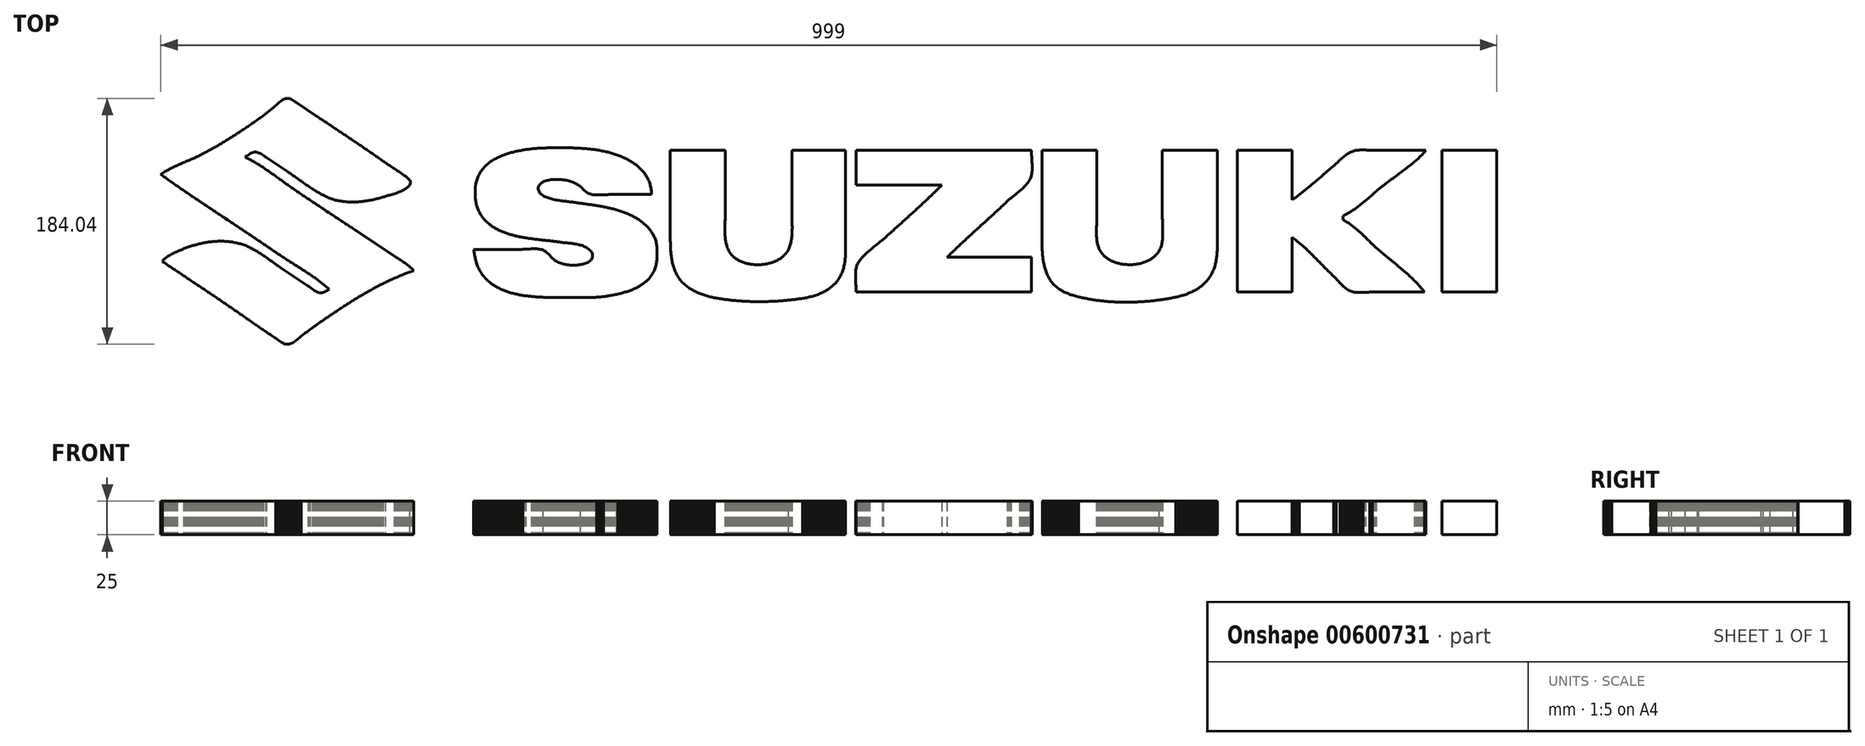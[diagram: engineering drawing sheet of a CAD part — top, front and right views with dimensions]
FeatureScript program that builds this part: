
annotation { "Feature Type Name" : "Feature", "Feature Type Description" : "" }
export const myFeature = defineFeature(function(context is Context, id is Id, definition is map)
    precondition{}
    {
        {
            var Q0;
            Q0=qCreatedBy(makeId("Top.planeOp"),FACE);
            var sketch = newSketch(context, id + "F0", { "sketchPlane" : qUnion([Q0])});
            skLineSegment(sketch, "E0", {"start": v(-499.5, 35.04) * mm, "end": v(-498.69, 34.46) * mm});
            skLineSegment(sketch, "E1", {"start": v(-498.69, 34.46) * mm, "end": v(-497.87, 33.88) * mm});
            skLineSegment(sketch, "E2", {"start": v(-497.87, 33.88) * mm, "end": v(-497.06, 33.3) * mm});
            skLineSegment(sketch, "E3", {"start": v(-497.06, 33.3) * mm, "end": v(-496.24, 32.72) * mm});
            skLineSegment(sketch, "E4", {"start": v(-496.24, 32.72) * mm, "end": v(-495.43, 32.14) * mm});
            skLineSegment(sketch, "E5", {"start": v(-495.43, 32.14) * mm, "end": v(-494.6, 31.56) * mm});
            skLineSegment(sketch, "E6", {"start": v(-494.6, 31.56) * mm, "end": v(-493.8, 30.99) * mm});
            skLineSegment(sketch, "E7", {"start": v(-493.8, 30.99) * mm, "end": v(-492.97, 30.41) * mm});
            skLineSegment(sketch, "E8", {"start": v(-492.97, 30.41) * mm, "end": v(-492.15, 29.84) * mm});
            skLineSegment(sketch, "E9", {"start": v(-492.15, 29.84) * mm, "end": v(-491.33, 29.26) * mm});
            skLineSegment(sketch, "E10", {"start": v(-491.33, 29.26) * mm, "end": v(-490.52, 28.69) * mm});
            skLineSegment(sketch, "E11", {"start": v(-490.52, 28.69) * mm, "end": v(-489.7, 28.11) * mm});
            skLineSegment(sketch, "E12", {"start": v(-489.7, 28.11) * mm, "end": v(-488.87, 27.54) * mm});
            skLineSegment(sketch, "E13", {"start": v(-488.87, 27.54) * mm, "end": v(-488.05, 26.97) * mm});
            skLineSegment(sketch, "E14", {"start": v(-488.05, 26.97) * mm, "end": v(-487.23, 26.4) * mm});
            skLineSegment(sketch, "E15", {"start": v(-487.23, 26.4) * mm, "end": v(-486.4, 25.83) * mm});
            skLineSegment(sketch, "E16", {"start": v(-486.4, 25.83) * mm, "end": v(-485.59, 25.26) * mm});
            skLineSegment(sketch, "E17", {"start": v(-485.59, 25.26) * mm, "end": v(-484.76, 24.7) * mm});
            skLineSegment(sketch, "E18", {"start": v(-484.76, 24.7) * mm, "end": v(-483.94, 24.12) * mm});
            skLineSegment(sketch, "E19", {"start": v(-483.94, 24.12) * mm, "end": v(-483.11, 23.56) * mm});
            skLineSegment(sketch, "E20", {"start": v(-483.11, 23.56) * mm, "end": v(-482.29, 22.99) * mm});
            skLineSegment(sketch, "E21", {"start": v(-482.29, 22.99) * mm, "end": v(-481.46, 22.42) * mm});
            skLineSegment(sketch, "E22", {"start": v(-481.46, 22.42) * mm, "end": v(-480.64, 21.86) * mm});
            skLineSegment(sketch, "E23", {"start": v(-480.64, 21.86) * mm, "end": v(-479.81, 21.3) * mm});
            skLineSegment(sketch, "E24", {"start": v(-479.81, 21.3) * mm, "end": v(-478.99, 20.73) * mm});
            skLineSegment(sketch, "E25", {"start": v(-478.99, 20.73) * mm, "end": v(-478.16, 20.16) * mm});
            skLineSegment(sketch, "E26", {"start": v(-478.16, 20.16) * mm, "end": v(-477.33, 19.6) * mm});
            skLineSegment(sketch, "E27", {"start": v(-477.33, 19.6) * mm, "end": v(-476.5, 19.04) * mm});
            skLineSegment(sketch, "E28", {"start": v(-476.5, 19.04) * mm, "end": v(-475.68, 18.47) * mm});
            skLineSegment(sketch, "E29", {"start": v(-475.68, 18.47) * mm, "end": v(-474.85, 17.91) * mm});
            skLineSegment(sketch, "E30", {"start": v(-474.85, 17.91) * mm, "end": v(-474.02, 17.35) * mm});
            skLineSegment(sketch, "E31", {"start": v(-474.02, 17.35) * mm, "end": v(-473.19, 16.79) * mm});
            skLineSegment(sketch, "E32", {"start": v(-473.19, 16.79) * mm, "end": v(-472.36, 16.23) * mm});
            skLineSegment(sketch, "E33", {"start": v(-472.36, 16.23) * mm, "end": v(-471.53, 15.67) * mm});
            skLineSegment(sketch, "E34", {"start": v(-471.53, 15.67) * mm, "end": v(-470.7, 15.1) * mm});
            skLineSegment(sketch, "E35", {"start": v(-470.7, 15.1) * mm, "end": v(-469.87, 14.55) * mm});
            skLineSegment(sketch, "E36", {"start": v(-469.87, 14.55) * mm, "end": v(-469.04, 13.99) * mm});
            skLineSegment(sketch, "E37", {"start": v(-469.04, 13.99) * mm, "end": v(-468.2, 13.43) * mm});
            skLineSegment(sketch, "E38", {"start": v(-468.2, 13.43) * mm, "end": v(-467.38, 12.87) * mm});
            skLineSegment(sketch, "E39", {"start": v(-467.38, 12.87) * mm, "end": v(-466.55, 12.31) * mm});
            skLineSegment(sketch, "E40", {"start": v(-466.55, 12.31) * mm, "end": v(-465.71, 11.76) * mm});
            skLineSegment(sketch, "E41", {"start": v(-465.71, 11.76) * mm, "end": v(-464.88, 11.2) * mm});
            skLineSegment(sketch, "E42", {"start": v(-464.88, 11.2) * mm, "end": v(-464.05, 10.64) * mm});
            skLineSegment(sketch, "E43", {"start": v(-464.05, 10.64) * mm, "end": v(-463.22, 10.09) * mm});
            skLineSegment(sketch, "E44", {"start": v(-463.22, 10.09) * mm, "end": v(-462.39, 9.53) * mm});
            skLineSegment(sketch, "E45", {"start": v(-462.39, 9.53) * mm, "end": v(-461.55, 8.97) * mm});
            skLineSegment(sketch, "E46", {"start": v(-461.55, 8.97) * mm, "end": v(-460.72, 8.42) * mm});
            skLineSegment(sketch, "E47", {"start": v(-460.72, 8.42) * mm, "end": v(-459.89, 7.86) * mm});
            skLineSegment(sketch, "E48", {"start": v(-459.89, 7.86) * mm, "end": v(-459.05, 7.3) * mm});
            skLineSegment(sketch, "E49", {"start": v(-459.05, 7.3) * mm, "end": v(-458.22, 6.75) * mm});
            skLineSegment(sketch, "E50", {"start": v(-458.22, 6.75) * mm, "end": v(-457.39, 6.2) * mm});
            skLineSegment(sketch, "E51", {"start": v(-457.39, 6.2) * mm, "end": v(-456.55, 5.64) * mm});
            skLineSegment(sketch, "E52", {"start": v(-456.55, 5.64) * mm, "end": v(-455.72, 5.08) * mm});
            skLineSegment(sketch, "E53", {"start": v(-455.72, 5.08) * mm, "end": v(-454.89, 4.53) * mm});
            skLineSegment(sketch, "E54", {"start": v(-454.89, 4.53) * mm, "end": v(-454.05, 3.98) * mm});
            skLineSegment(sketch, "E55", {"start": v(-454.05, 3.98) * mm, "end": v(-453.22, 3.42) * mm});
            skLineSegment(sketch, "E56", {"start": v(-453.22, 3.42) * mm, "end": v(-452.38, 2.87) * mm});
            skLineSegment(sketch, "E57", {"start": v(-452.38, 2.87) * mm, "end": v(-451.55, 2.31) * mm});
            skLineSegment(sketch, "E58", {"start": v(-451.55, 2.31) * mm, "end": v(-450.72, 1.76) * mm});
            skLineSegment(sketch, "E59", {"start": v(-450.72, 1.76) * mm, "end": v(-449.88, 1.2) * mm});
            skLineSegment(sketch, "E60", {"start": v(-449.88, 1.2) * mm, "end": v(-449.05, 0.65) * mm});
            skLineSegment(sketch, "E61", {"start": v(-449.05, 0.65) * mm, "end": v(-448.21, 0.1) * mm});
            skLineSegment(sketch, "E62", {"start": v(-448.21, 0.1) * mm, "end": v(-447.38, -0.46) * mm});
            skLineSegment(sketch, "E63", {"start": v(-447.38, -0.46) * mm, "end": v(-446.55, -1.01) * mm});
            skLineSegment(sketch, "E64", {"start": v(-446.55, -1.01) * mm, "end": v(-445.71, -1.57) * mm});
            skLineSegment(sketch, "E65", {"start": v(-445.71, -1.57) * mm, "end": v(-444.88, -2.12) * mm});
            skLineSegment(sketch, "E66", {"start": v(-444.88, -2.12) * mm, "end": v(-444.04, -2.68) * mm});
            skLineSegment(sketch, "E67", {"start": v(-444.04, -2.68) * mm, "end": v(-443.21, -3.23) * mm});
            skLineSegment(sketch, "E68", {"start": v(-443.21, -3.23) * mm, "end": v(-442.38, -3.79) * mm});
            skLineSegment(sketch, "E69", {"start": v(-442.38, -3.79) * mm, "end": v(-441.54, -4.34) * mm});
            skLineSegment(sketch, "E70", {"start": v(-441.54, -4.34) * mm, "end": v(-440.7, -4.9) * mm});
            skLineSegment(sketch, "E71", {"start": v(-440.7, -4.9) * mm, "end": v(-439.88, -5.45) * mm});
            skLineSegment(sketch, "E72", {"start": v(-439.88, -5.45) * mm, "end": v(-439.04, -6) * mm});
            skLineSegment(sketch, "E73", {"start": v(-439.04, -6) * mm, "end": v(-438.2, -6.56) * mm});
            skLineSegment(sketch, "E74", {"start": v(-438.2, -6.56) * mm, "end": v(-437.38, -7.12) * mm});
            skLineSegment(sketch, "E75", {"start": v(-437.38, -7.12) * mm, "end": v(-436.54, -7.67) * mm});
            skLineSegment(sketch, "E76", {"start": v(-436.54, -7.67) * mm, "end": v(-435.71, -8.23) * mm});
            skLineSegment(sketch, "E77", {"start": v(-435.71, -8.23) * mm, "end": v(-434.88, -8.78) * mm});
            skLineSegment(sketch, "E78", {"start": v(-434.88, -8.78) * mm, "end": v(-434.05, -9.34) * mm});
            skLineSegment(sketch, "E79", {"start": v(-434.05, -9.34) * mm, "end": v(-433.21, -9.9) * mm});
            skLineSegment(sketch, "E80", {"start": v(-433.21, -9.9) * mm, "end": v(-432.38, -10.45) * mm});
            skLineSegment(sketch, "E81", {"start": v(-432.38, -10.45) * mm, "end": v(-431.55, -11) * mm});
            skLineSegment(sketch, "E82", {"start": v(-431.55, -11) * mm, "end": v(-430.72, -11.57) * mm});
            skLineSegment(sketch, "E83", {"start": v(-430.72, -11.57) * mm, "end": v(-429.89, -12.12) * mm});
            skLineSegment(sketch, "E84", {"start": v(-429.89, -12.12) * mm, "end": v(-429.06, -12.68) * mm});
            skLineSegment(sketch, "E85", {"start": v(-429.06, -12.68) * mm, "end": v(-428.22, -13.24) * mm});
            skLineSegment(sketch, "E86", {"start": v(-428.22, -13.24) * mm, "end": v(-427.4, -13.8) * mm});
            skLineSegment(sketch, "E87", {"start": v(-427.4, -13.8) * mm, "end": v(-426.56, -14.36) * mm});
            skLineSegment(sketch, "E88", {"start": v(-426.56, -14.36) * mm, "end": v(-425.73, -14.92) * mm});
            skLineSegment(sketch, "E89", {"start": v(-425.73, -14.92) * mm, "end": v(-424.9, -15.48) * mm});
            skLineSegment(sketch, "E90", {"start": v(-424.9, -15.48) * mm, "end": v(-424.07, -16.04) * mm});
            skLineSegment(sketch, "E91", {"start": v(-424.07, -16.04) * mm, "end": v(-423.24, -16.6) * mm});
            skLineSegment(sketch, "E92", {"start": v(-423.24, -16.6) * mm, "end": v(-422.42, -17.16) * mm});
            skLineSegment(sketch, "E93", {"start": v(-422.42, -17.16) * mm, "end": v(-421.59, -17.72) * mm});
            skLineSegment(sketch, "E94", {"start": v(-421.59, -17.72) * mm, "end": v(-420.76, -18.28) * mm});
            skLineSegment(sketch, "E95", {"start": v(-420.76, -18.28) * mm, "end": v(-419.93, -18.84) * mm});
            skLineSegment(sketch, "E96", {"start": v(-419.93, -18.84) * mm, "end": v(-419.1, -19.4) * mm});
            skLineSegment(sketch, "E97", {"start": v(-419.1, -19.4) * mm, "end": v(-418.28, -19.97) * mm});
            skLineSegment(sketch, "E98", {"start": v(-418.28, -19.97) * mm, "end": v(-417.45, -20.54) * mm});
            skLineSegment(sketch, "E99", {"start": v(-417.45, -20.54) * mm, "end": v(-416.62, -21.1) * mm});
            skLineSegment(sketch, "E100", {"start": v(-416.62, -21.1) * mm, "end": v(-415.8, -21.66) * mm});
            skLineSegment(sketch, "E101", {"start": v(-415.8, -21.66) * mm, "end": v(-414.97, -22.23) * mm});
            skLineSegment(sketch, "E102", {"start": v(-414.97, -22.23) * mm, "end": v(-414.15, -22.8) * mm});
            skLineSegment(sketch, "E103", {"start": v(-414.15, -22.8) * mm, "end": v(-413.32, -23.36) * mm});
            skLineSegment(sketch, "E104", {"start": v(-413.32, -23.36) * mm, "end": v(-412.5, -23.93) * mm});
            skLineSegment(sketch, "E105", {"start": v(-412.5, -23.93) * mm, "end": v(-411.68, -24.5) * mm});
            skLineSegment(sketch, "E106", {"start": v(-411.68, -24.5) * mm, "end": v(-410.85, -25.06) * mm});
            skLineSegment(sketch, "E107", {"start": v(-410.85, -25.06) * mm, "end": v(-410.02, -25.61) * mm});
            skLineSegment(sketch, "E108", {"start": v(-410.02, -25.61) * mm, "end": v(-409.18, -26.17) * mm});
            skLineSegment(sketch, "E109", {"start": v(-409.18, -26.17) * mm, "end": v(-408.34, -26.72) * mm});
            skLineSegment(sketch, "E110", {"start": v(-408.34, -26.72) * mm, "end": v(-407.5, -27.27) * mm});
            skLineSegment(sketch, "E111", {"start": v(-407.5, -27.27) * mm, "end": v(-406.65, -27.82) * mm});
            skLineSegment(sketch, "E112", {"start": v(-406.65, -27.82) * mm, "end": v(-405.8, -28.37) * mm});
            skLineSegment(sketch, "E113", {"start": v(-405.8, -28.37) * mm, "end": v(-404.95, -28.92) * mm});
            skLineSegment(sketch, "E114", {"start": v(-404.95, -28.92) * mm, "end": v(-404.1, -29.46) * mm});
            skLineSegment(sketch, "E115", {"start": v(-404.1, -29.46) * mm, "end": v(-403.25, -30) * mm});
            skLineSegment(sketch, "E116", {"start": v(-403.25, -30) * mm, "end": v(-402.39, -30.55) * mm});
            skLineSegment(sketch, "E117", {"start": v(-402.39, -30.55) * mm, "end": v(-401.53, -31.09) * mm});
            skLineSegment(sketch, "E118", {"start": v(-401.53, -31.09) * mm, "end": v(-400.67, -31.63) * mm});
            skLineSegment(sketch, "E119", {"start": v(-400.67, -31.63) * mm, "end": v(-399.81, -32.17) * mm});
            skLineSegment(sketch, "E120", {"start": v(-399.81, -32.17) * mm, "end": v(-398.95, -32.72) * mm});
            skLineSegment(sketch, "E121", {"start": v(-398.95, -32.72) * mm, "end": v(-398.1, -33.26) * mm});
            skLineSegment(sketch, "E122", {"start": v(-398.1, -33.26) * mm, "end": v(-397.23, -33.8) * mm});
            skLineSegment(sketch, "E123", {"start": v(-397.23, -33.8) * mm, "end": v(-396.37, -34.35) * mm});
            skLineSegment(sketch, "E124", {"start": v(-396.37, -34.35) * mm, "end": v(-395.51, -34.9) * mm});
            skLineSegment(sketch, "E125", {"start": v(-395.51, -34.9) * mm, "end": v(-394.65, -35.44) * mm});
            skLineSegment(sketch, "E126", {"start": v(-394.65, -35.44) * mm, "end": v(-393.8, -35.99) * mm});
            skLineSegment(sketch, "E127", {"start": v(-393.8, -35.99) * mm, "end": v(-392.94, -36.54) * mm});
            skLineSegment(sketch, "E128", {"start": v(-392.94, -36.54) * mm, "end": v(-392.08, -37.09) * mm});
            skLineSegment(sketch, "E129", {"start": v(-392.08, -37.09) * mm, "end": v(-391.23, -37.64) * mm});
            skLineSegment(sketch, "E130", {"start": v(-391.23, -37.64) * mm, "end": v(-390.38, -38.2) * mm});
            skLineSegment(sketch, "E131", {"start": v(-390.38, -38.2) * mm, "end": v(-389.53, -38.76) * mm});
            skLineSegment(sketch, "E132", {"start": v(-389.53, -38.76) * mm, "end": v(-388.68, -39.33) * mm});
            skLineSegment(sketch, "E133", {"start": v(-388.68, -39.33) * mm, "end": v(-387.84, -39.9) * mm});
            skLineSegment(sketch, "E134", {"start": v(-387.84, -39.9) * mm, "end": v(-387, -40.46) * mm});
            skLineSegment(sketch, "E135", {"start": v(-387, -40.46) * mm, "end": v(-386.17, -41.04) * mm});
            skLineSegment(sketch, "E136", {"start": v(-386.17, -41.04) * mm, "end": v(-385.34, -41.62) * mm});
            skLineSegment(sketch, "E137", {"start": v(-385.34, -41.62) * mm, "end": v(-384.5, -42.2) * mm});
            skLineSegment(sketch, "E138", {"start": v(-384.5, -42.2) * mm, "end": v(-383.68, -42.79) * mm});
            skLineSegment(sketch, "E139", {"start": v(-383.68, -42.79) * mm, "end": v(-382.86, -43.38) * mm});
            skLineSegment(sketch, "E140", {"start": v(-382.86, -43.38) * mm, "end": v(-382.05, -43.98) * mm});
            skLineSegment(sketch, "E141", {"start": v(-382.05, -43.98) * mm, "end": v(-381.24, -44.58) * mm});
            skLineSegment(sketch, "E142", {"start": v(-381.24, -44.58) * mm, "end": v(-380.44, -45.2) * mm});
            skLineSegment(sketch, "E143", {"start": v(-380.44, -45.2) * mm, "end": v(-379.64, -45.8) * mm});
            skLineSegment(sketch, "E144", {"start": v(-379.64, -45.8) * mm, "end": v(-378.85, -46.42) * mm});
            skLineSegment(sketch, "E145", {"start": v(-378.85, -46.42) * mm, "end": v(-378.06, -47.05) * mm});
            skLineSegment(sketch, "E146", {"start": v(-378.06, -47.05) * mm, "end": v(-377.29, -47.68) * mm});
            skLineSegment(sketch, "E147", {"start": v(-377.29, -47.68) * mm, "end": v(-376.51, -48.32) * mm});
            skLineSegment(sketch, "E148", {"start": v(-376.51, -48.32) * mm, "end": v(-375.75, -48.97) * mm});
            skLineSegment(sketch, "E149", {"start": v(-375.75, -48.97) * mm, "end": v(-375, -49.63) * mm});
            skLineSegment(sketch, "E150", {"start": v(-375, -49.63) * mm, "end": v(-374.24, -50.29) * mm});
            skLineSegment(sketch, "E151", {"start": v(-374.24, -50.29) * mm, "end": v(-373.5, -50.96) * mm});
            skLineSegment(sketch, "E152", {"start": v(-373.5, -50.96) * mm, "end": v(-374.36, -51.38) * mm});
            skLineSegment(sketch, "E153", {"start": v(-374.36, -51.38) * mm, "end": v(-375.27, -51.87) * mm});
            skLineSegment(sketch, "E154", {"start": v(-375.27, -51.87) * mm, "end": v(-376.2, -52.36) * mm});
            skLineSegment(sketch, "E155", {"start": v(-376.2, -52.36) * mm, "end": v(-377.18, -52.83) * mm});
            skLineSegment(sketch, "E156", {"start": v(-377.18, -52.83) * mm, "end": v(-378.15, -53.21) * mm});
            skLineSegment(sketch, "E157", {"start": v(-378.15, -53.21) * mm, "end": v(-379.12, -53.47) * mm});
            skLineSegment(sketch, "E158", {"start": v(-379.12, -53.47) * mm, "end": v(-380.08, -53.56) * mm});
            skLineSegment(sketch, "E159", {"start": v(-380.08, -53.56) * mm, "end": v(-380.97, -53.46) * mm});
            skLineSegment(sketch, "E160", {"start": v(-380.97, -53.46) * mm, "end": v(-381.88, -53.22) * mm});
            skLineSegment(sketch, "E161", {"start": v(-381.88, -53.22) * mm, "end": v(-382.79, -52.85) * mm});
            skLineSegment(sketch, "E162", {"start": v(-382.79, -52.85) * mm, "end": v(-383.7, -52.38) * mm});
            skLineSegment(sketch, "E163", {"start": v(-383.7, -52.38) * mm, "end": v(-384.6, -51.84) * mm});
            skLineSegment(sketch, "E164", {"start": v(-384.6, -51.84) * mm, "end": v(-385.49, -51.24) * mm});
            skLineSegment(sketch, "E165", {"start": v(-385.49, -51.24) * mm, "end": v(-386.35, -50.62) * mm});
            skLineSegment(sketch, "E166", {"start": v(-386.35, -50.62) * mm, "end": v(-387.2, -49.98) * mm});
            skLineSegment(sketch, "E167", {"start": v(-387.2, -49.98) * mm, "end": v(-388, -49.37) * mm});
            skLineSegment(sketch, "E168", {"start": v(-388, -49.37) * mm, "end": v(-388.77, -48.8) * mm});
            skLineSegment(sketch, "E169", {"start": v(-388.77, -48.8) * mm, "end": v(-389.5, -48.29) * mm});
            skLineSegment(sketch, "E170", {"start": v(-389.5, -48.29) * mm, "end": v(-409.5, -34.96) * mm});
            skLineSegment(sketch, "E171", {"start": v(-409.5, -34.96) * mm, "end": v(-410.3, -34.42) * mm});
            skLineSegment(sketch, "E172", {"start": v(-410.3, -34.42) * mm, "end": v(-411.11, -33.86) * mm});
            skLineSegment(sketch, "E173", {"start": v(-411.11, -33.86) * mm, "end": v(-411.92, -33.3) * mm});
            skLineSegment(sketch, "E174", {"start": v(-411.92, -33.3) * mm, "end": v(-412.73, -32.74) * mm});
            skLineSegment(sketch, "E175", {"start": v(-412.73, -32.74) * mm, "end": v(-413.54, -32.17) * mm});
            skLineSegment(sketch, "E176", {"start": v(-413.54, -32.17) * mm, "end": v(-414.35, -31.59) * mm});
            skLineSegment(sketch, "E177", {"start": v(-414.35, -31.59) * mm, "end": v(-415.16, -31) * mm});
            skLineSegment(sketch, "E178", {"start": v(-415.16, -31) * mm, "end": v(-415.98, -30.42) * mm});
            skLineSegment(sketch, "E179", {"start": v(-415.98, -30.42) * mm, "end": v(-416.8, -29.84) * mm});
            skLineSegment(sketch, "E180", {"start": v(-416.8, -29.84) * mm, "end": v(-417.62, -29.25) * mm});
            skLineSegment(sketch, "E181", {"start": v(-417.62, -29.25) * mm, "end": v(-418.44, -28.66) * mm});
            skLineSegment(sketch, "E182", {"start": v(-418.44, -28.66) * mm, "end": v(-419.27, -28.07) * mm});
            skLineSegment(sketch, "E183", {"start": v(-419.27, -28.07) * mm, "end": v(-420.1, -27.48) * mm});
            skLineSegment(sketch, "E184", {"start": v(-420.1, -27.48) * mm, "end": v(-420.92, -26.9) * mm});
            skLineSegment(sketch, "E185", {"start": v(-420.92, -26.9) * mm, "end": v(-421.76, -26.32) * mm});
            skLineSegment(sketch, "E186", {"start": v(-421.76, -26.32) * mm, "end": v(-422.6, -25.75) * mm});
            skLineSegment(sketch, "E187", {"start": v(-422.6, -25.75) * mm, "end": v(-423.43, -25.18) * mm});
            skLineSegment(sketch, "E188", {"start": v(-423.43, -25.18) * mm, "end": v(-424.28, -24.62) * mm});
            skLineSegment(sketch, "E189", {"start": v(-424.28, -24.62) * mm, "end": v(-425.12, -24.06) * mm});
            skLineSegment(sketch, "E190", {"start": v(-425.12, -24.06) * mm, "end": v(-425.97, -23.52) * mm});
            skLineSegment(sketch, "E191", {"start": v(-425.97, -23.52) * mm, "end": v(-426.83, -22.98) * mm});
            skLineSegment(sketch, "E192", {"start": v(-426.83, -22.98) * mm, "end": v(-427.68, -22.46) * mm});
            skLineSegment(sketch, "E193", {"start": v(-427.68, -22.46) * mm, "end": v(-428.54, -21.94) * mm});
            skLineSegment(sketch, "E194", {"start": v(-428.54, -21.94) * mm, "end": v(-429.41, -21.44) * mm});
            skLineSegment(sketch, "E195", {"start": v(-429.41, -21.44) * mm, "end": v(-430.28, -20.96) * mm});
            skLineSegment(sketch, "E196", {"start": v(-430.28, -20.96) * mm, "end": v(-431.15, -20.49) * mm});
            skLineSegment(sketch, "E197", {"start": v(-431.15, -20.49) * mm, "end": v(-432.03, -20.03) * mm});
            skLineSegment(sketch, "E198", {"start": v(-432.03, -20.03) * mm, "end": v(-432.92, -19.6) * mm});
            skLineSegment(sketch, "E199", {"start": v(-432.92, -19.6) * mm, "end": v(-433.8, -19.17) * mm});
            skLineSegment(sketch, "E200", {"start": v(-433.8, -19.17) * mm, "end": v(-434.7, -18.77) * mm});
            skLineSegment(sketch, "E201", {"start": v(-434.7, -18.77) * mm, "end": v(-435.6, -18.39) * mm});
            skLineSegment(sketch, "E202", {"start": v(-435.6, -18.39) * mm, "end": v(-436.5, -18.03) * mm});
            skLineSegment(sketch, "E203", {"start": v(-436.5, -18.03) * mm, "end": v(-437.41, -17.69) * mm});
            skLineSegment(sketch, "E204", {"start": v(-437.41, -17.69) * mm, "end": v(-438.33, -17.37) * mm});
            skLineSegment(sketch, "E205", {"start": v(-438.33, -17.37) * mm, "end": v(-439.25, -17.07) * mm});
            skLineSegment(sketch, "E206", {"start": v(-439.25, -17.07) * mm, "end": v(-440.18, -16.79) * mm});
            skLineSegment(sketch, "E207", {"start": v(-440.18, -16.79) * mm, "end": v(-441.12, -16.53) * mm});
            skLineSegment(sketch, "E208", {"start": v(-441.12, -16.53) * mm, "end": v(-442.06, -16.3) * mm});
            skLineSegment(sketch, "E209", {"start": v(-442.06, -16.3) * mm, "end": v(-443.01, -16.07) * mm});
            skLineSegment(sketch, "E210", {"start": v(-443.01, -16.07) * mm, "end": v(-443.97, -15.88) * mm});
            skLineSegment(sketch, "E211", {"start": v(-443.97, -15.88) * mm, "end": v(-444.93, -15.7) * mm});
            skLineSegment(sketch, "E212", {"start": v(-444.93, -15.7) * mm, "end": v(-445.9, -15.53) * mm});
            skLineSegment(sketch, "E213", {"start": v(-445.9, -15.53) * mm, "end": v(-446.86, -15.39) * mm});
            skLineSegment(sketch, "E214", {"start": v(-446.86, -15.39) * mm, "end": v(-447.83, -15.26) * mm});
            skLineSegment(sketch, "E215", {"start": v(-447.83, -15.26) * mm, "end": v(-448.8, -15.16) * mm});
            skLineSegment(sketch, "E216", {"start": v(-448.8, -15.16) * mm, "end": v(-449.79, -15.07) * mm});
            skLineSegment(sketch, "E217", {"start": v(-449.79, -15.07) * mm, "end": v(-450.77, -15) * mm});
            skLineSegment(sketch, "E218", {"start": v(-450.77, -15) * mm, "end": v(-451.76, -14.94) * mm});
            skLineSegment(sketch, "E219", {"start": v(-451.76, -14.94) * mm, "end": v(-452.74, -14.9) * mm});
            skLineSegment(sketch, "E220", {"start": v(-452.74, -14.9) * mm, "end": v(-453.73, -14.88) * mm});
            skLineSegment(sketch, "E221", {"start": v(-453.73, -14.88) * mm, "end": v(-454.72, -14.88) * mm});
            skLineSegment(sketch, "E222", {"start": v(-454.72, -14.88) * mm, "end": v(-455.72, -14.89) * mm});
            skLineSegment(sketch, "E223", {"start": v(-455.72, -14.89) * mm, "end": v(-456.71, -14.91) * mm});
            skLineSegment(sketch, "E224", {"start": v(-456.71, -14.91) * mm, "end": v(-457.7, -14.96) * mm});
            skLineSegment(sketch, "E225", {"start": v(-457.7, -14.96) * mm, "end": v(-458.7, -15.01) * mm});
            skLineSegment(sketch, "E226", {"start": v(-458.7, -15.01) * mm, "end": v(-459.7, -15.09) * mm});
            skLineSegment(sketch, "E227", {"start": v(-459.7, -15.09) * mm, "end": v(-460.68, -15.17) * mm});
            skLineSegment(sketch, "E228", {"start": v(-460.68, -15.17) * mm, "end": v(-461.68, -15.27) * mm});
            skLineSegment(sketch, "E229", {"start": v(-461.68, -15.27) * mm, "end": v(-462.67, -15.39) * mm});
            skLineSegment(sketch, "E230", {"start": v(-462.67, -15.39) * mm, "end": v(-463.66, -15.52) * mm});
            skLineSegment(sketch, "E231", {"start": v(-463.66, -15.52) * mm, "end": v(-464.65, -15.66) * mm});
            skLineSegment(sketch, "E232", {"start": v(-464.65, -15.66) * mm, "end": v(-465.63, -15.82) * mm});
            skLineSegment(sketch, "E233", {"start": v(-465.63, -15.82) * mm, "end": v(-466.62, -15.99) * mm});
            skLineSegment(sketch, "E234", {"start": v(-466.62, -15.99) * mm, "end": v(-467.6, -16.17) * mm});
            skLineSegment(sketch, "E235", {"start": v(-467.6, -16.17) * mm, "end": v(-468.57, -16.36) * mm});
            skLineSegment(sketch, "E236", {"start": v(-468.57, -16.36) * mm, "end": v(-469.55, -16.57) * mm});
            skLineSegment(sketch, "E237", {"start": v(-469.55, -16.57) * mm, "end": v(-470.52, -16.8) * mm});
            skLineSegment(sketch, "E238", {"start": v(-470.52, -16.8) * mm, "end": v(-471.48, -17.02) * mm});
            skLineSegment(sketch, "E239", {"start": v(-471.48, -17.02) * mm, "end": v(-472.44, -17.26) * mm});
            skLineSegment(sketch, "E240", {"start": v(-472.44, -17.26) * mm, "end": v(-473.4, -17.52) * mm});
            skLineSegment(sketch, "E241", {"start": v(-473.4, -17.52) * mm, "end": v(-474.35, -17.78) * mm});
            skLineSegment(sketch, "E242", {"start": v(-474.35, -17.78) * mm, "end": v(-475.3, -18.06) * mm});
            skLineSegment(sketch, "E243", {"start": v(-475.3, -18.06) * mm, "end": v(-476.24, -18.34) * mm});
            skLineSegment(sketch, "E244", {"start": v(-476.24, -18.34) * mm, "end": v(-477.17, -18.64) * mm});
            skLineSegment(sketch, "E245", {"start": v(-477.17, -18.64) * mm, "end": v(-478.1, -18.94) * mm});
            skLineSegment(sketch, "E246", {"start": v(-478.1, -18.94) * mm, "end": v(-479.02, -19.26) * mm});
            skLineSegment(sketch, "E247", {"start": v(-479.02, -19.26) * mm, "end": v(-479.93, -19.58) * mm});
            skLineSegment(sketch, "E248", {"start": v(-479.93, -19.58) * mm, "end": v(-480.83, -19.92) * mm});
            skLineSegment(sketch, "E249", {"start": v(-480.83, -19.92) * mm, "end": v(-481.73, -20.26) * mm});
            skLineSegment(sketch, "E250", {"start": v(-481.73, -20.26) * mm, "end": v(-482.62, -20.6) * mm});
            skLineSegment(sketch, "E251", {"start": v(-482.62, -20.6) * mm, "end": v(-483.5, -20.97) * mm});
            skLineSegment(sketch, "E252", {"start": v(-483.5, -20.97) * mm, "end": v(-484.45, -21.36) * mm});
            skLineSegment(sketch, "E253", {"start": v(-484.45, -21.36) * mm, "end": v(-485.4, -21.76) * mm});
            skLineSegment(sketch, "E254", {"start": v(-485.4, -21.76) * mm, "end": v(-486.37, -22.16) * mm});
            skLineSegment(sketch, "E255", {"start": v(-486.37, -22.16) * mm, "end": v(-487.33, -22.58) * mm});
            skLineSegment(sketch, "E256", {"start": v(-487.33, -22.58) * mm, "end": v(-488.28, -23) * mm});
            skLineSegment(sketch, "E257", {"start": v(-488.28, -23) * mm, "end": v(-489.24, -23.45) * mm});
            skLineSegment(sketch, "E258", {"start": v(-489.24, -23.45) * mm, "end": v(-490.18, -23.9) * mm});
            skLineSegment(sketch, "E259", {"start": v(-490.18, -23.9) * mm, "end": v(-491.12, -24.38) * mm});
            skLineSegment(sketch, "E260", {"start": v(-491.12, -24.38) * mm, "end": v(-492.04, -24.88) * mm});
            skLineSegment(sketch, "E261", {"start": v(-492.04, -24.88) * mm, "end": v(-492.94, -25.4) * mm});
            skLineSegment(sketch, "E262", {"start": v(-492.94, -25.4) * mm, "end": v(-493.82, -25.95) * mm});
            skLineSegment(sketch, "E263", {"start": v(-493.82, -25.95) * mm, "end": v(-494.68, -26.53) * mm});
            skLineSegment(sketch, "E264", {"start": v(-494.68, -26.53) * mm, "end": v(-495.5, -27.15) * mm});
            skLineSegment(sketch, "E265", {"start": v(-495.5, -27.15) * mm, "end": v(-496.3, -27.8) * mm});
            skLineSegment(sketch, "E266", {"start": v(-496.3, -27.8) * mm, "end": v(-497.08, -28.47) * mm});
            skLineSegment(sketch, "E267", {"start": v(-497.08, -28.47) * mm, "end": v(-497.8, -29.2) * mm});
            skLineSegment(sketch, "E268", {"start": v(-497.8, -29.2) * mm, "end": v(-498.5, -29.96) * mm});
            skLineSegment(sketch, "E269", {"start": v(-498.5, -29.96) * mm, "end": v(-497.66, -30.52) * mm});
            skLineSegment(sketch, "E270", {"start": v(-497.66, -30.52) * mm, "end": v(-496.82, -31.09) * mm});
            skLineSegment(sketch, "E271", {"start": v(-496.82, -31.09) * mm, "end": v(-495.98, -31.65) * mm});
            skLineSegment(sketch, "E272", {"start": v(-495.98, -31.65) * mm, "end": v(-495.14, -32.22) * mm});
            skLineSegment(sketch, "E273", {"start": v(-495.14, -32.22) * mm, "end": v(-494.3, -32.78) * mm});
            skLineSegment(sketch, "E274", {"start": v(-494.3, -32.78) * mm, "end": v(-493.47, -33.34) * mm});
            skLineSegment(sketch, "E275", {"start": v(-493.47, -33.34) * mm, "end": v(-492.63, -33.9) * mm});
            skLineSegment(sketch, "E276", {"start": v(-492.63, -33.9) * mm, "end": v(-491.79, -34.47) * mm});
            skLineSegment(sketch, "E277", {"start": v(-491.79, -34.47) * mm, "end": v(-490.95, -35.04) * mm});
            skLineSegment(sketch, "E278", {"start": v(-490.95, -35.04) * mm, "end": v(-490.1, -35.6) * mm});
            skLineSegment(sketch, "E279", {"start": v(-490.1, -35.6) * mm, "end": v(-489.27, -36.16) * mm});
            skLineSegment(sketch, "E280", {"start": v(-489.27, -36.16) * mm, "end": v(-488.43, -36.73) * mm});
            skLineSegment(sketch, "E281", {"start": v(-488.43, -36.73) * mm, "end": v(-487.58, -37.29) * mm});
            skLineSegment(sketch, "E282", {"start": v(-487.58, -37.29) * mm, "end": v(-486.74, -37.85) * mm});
            skLineSegment(sketch, "E283", {"start": v(-486.74, -37.85) * mm, "end": v(-485.9, -38.41) * mm});
            skLineSegment(sketch, "E284", {"start": v(-485.9, -38.41) * mm, "end": v(-485.06, -38.98) * mm});
            skLineSegment(sketch, "E285", {"start": v(-485.06, -38.98) * mm, "end": v(-484.22, -39.54) * mm});
            skLineSegment(sketch, "E286", {"start": v(-484.22, -39.54) * mm, "end": v(-483.38, -40.1) * mm});
            skLineSegment(sketch, "E287", {"start": v(-483.38, -40.1) * mm, "end": v(-482.54, -40.66) * mm});
            skLineSegment(sketch, "E288", {"start": v(-482.54, -40.66) * mm, "end": v(-481.7, -41.23) * mm});
            skLineSegment(sketch, "E289", {"start": v(-481.7, -41.23) * mm, "end": v(-480.86, -41.79) * mm});
            skLineSegment(sketch, "E290", {"start": v(-480.86, -41.79) * mm, "end": v(-480.01, -42.35) * mm});
            skLineSegment(sketch, "E291", {"start": v(-480.01, -42.35) * mm, "end": v(-479.17, -42.91) * mm});
            skLineSegment(sketch, "E292", {"start": v(-479.17, -42.91) * mm, "end": v(-478.33, -43.48) * mm});
            skLineSegment(sketch, "E293", {"start": v(-478.33, -43.48) * mm, "end": v(-477.49, -44.04) * mm});
            skLineSegment(sketch, "E294", {"start": v(-477.49, -44.04) * mm, "end": v(-476.65, -44.6) * mm});
            skLineSegment(sketch, "E295", {"start": v(-476.65, -44.6) * mm, "end": v(-475.8, -45.16) * mm});
            skLineSegment(sketch, "E296", {"start": v(-475.8, -45.16) * mm, "end": v(-474.97, -45.73) * mm});
            skLineSegment(sketch, "E297", {"start": v(-474.97, -45.73) * mm, "end": v(-474.12, -46.29) * mm});
            skLineSegment(sketch, "E298", {"start": v(-474.12, -46.29) * mm, "end": v(-473.28, -46.85) * mm});
            skLineSegment(sketch, "E299", {"start": v(-473.28, -46.85) * mm, "end": v(-472.44, -47.41) * mm});
            skLineSegment(sketch, "E300", {"start": v(-472.44, -47.41) * mm, "end": v(-471.6, -47.98) * mm});
            skLineSegment(sketch, "E301", {"start": v(-471.6, -47.98) * mm, "end": v(-470.76, -48.54) * mm});
            skLineSegment(sketch, "E302", {"start": v(-470.76, -48.54) * mm, "end": v(-469.92, -49.1) * mm});
            skLineSegment(sketch, "E303", {"start": v(-469.92, -49.1) * mm, "end": v(-469.08, -49.67) * mm});
            skLineSegment(sketch, "E304", {"start": v(-469.08, -49.67) * mm, "end": v(-468.24, -50.23) * mm});
            skLineSegment(sketch, "E305", {"start": v(-468.24, -50.23) * mm, "end": v(-467.4, -50.8) * mm});
            skLineSegment(sketch, "E306", {"start": v(-467.4, -50.8) * mm, "end": v(-466.55, -51.36) * mm});
            skLineSegment(sketch, "E307", {"start": v(-466.55, -51.36) * mm, "end": v(-465.71, -51.92) * mm});
            skLineSegment(sketch, "E308", {"start": v(-465.71, -51.92) * mm, "end": v(-464.87, -52.49) * mm});
            skLineSegment(sketch, "E309", {"start": v(-464.87, -52.49) * mm, "end": v(-464.03, -53.05) * mm});
            skLineSegment(sketch, "E310", {"start": v(-464.03, -53.05) * mm, "end": v(-463.2, -53.61) * mm});
            skLineSegment(sketch, "E311", {"start": v(-463.2, -53.61) * mm, "end": v(-462.35, -54.18) * mm});
            skLineSegment(sketch, "E312", {"start": v(-462.35, -54.18) * mm, "end": v(-461.51, -54.74) * mm});
            skLineSegment(sketch, "E313", {"start": v(-461.51, -54.74) * mm, "end": v(-460.67, -55.31) * mm});
            skLineSegment(sketch, "E314", {"start": v(-460.67, -55.31) * mm, "end": v(-459.83, -55.88) * mm});
            skLineSegment(sketch, "E315", {"start": v(-459.83, -55.88) * mm, "end": v(-459, -56.44) * mm});
            skLineSegment(sketch, "E316", {"start": v(-459, -56.44) * mm, "end": v(-458.16, -57) * mm});
            skLineSegment(sketch, "E317", {"start": v(-458.16, -57) * mm, "end": v(-457.32, -57.58) * mm});
            skLineSegment(sketch, "E318", {"start": v(-457.32, -57.58) * mm, "end": v(-456.48, -58.14) * mm});
            skLineSegment(sketch, "E319", {"start": v(-456.48, -58.14) * mm, "end": v(-455.64, -58.7) * mm});
            skLineSegment(sketch, "E320", {"start": v(-455.64, -58.7) * mm, "end": v(-454.8, -59.28) * mm});
            skLineSegment(sketch, "E321", {"start": v(-454.8, -59.28) * mm, "end": v(-453.97, -59.85) * mm});
            skLineSegment(sketch, "E322", {"start": v(-453.97, -59.85) * mm, "end": v(-453.13, -60.41) * mm});
            skLineSegment(sketch, "E323", {"start": v(-453.13, -60.41) * mm, "end": v(-452.3, -60.98) * mm});
            skLineSegment(sketch, "E324", {"start": v(-452.3, -60.98) * mm, "end": v(-451.46, -61.55) * mm});
            skLineSegment(sketch, "E325", {"start": v(-451.46, -61.55) * mm, "end": v(-450.62, -62.12) * mm});
            skLineSegment(sketch, "E326", {"start": v(-450.62, -62.12) * mm, "end": v(-449.78, -62.7) * mm});
            skLineSegment(sketch, "E327", {"start": v(-449.78, -62.7) * mm, "end": v(-448.95, -63.26) * mm});
            skLineSegment(sketch, "E328", {"start": v(-448.95, -63.26) * mm, "end": v(-448.11, -63.84) * mm});
            skLineSegment(sketch, "E329", {"start": v(-448.11, -63.84) * mm, "end": v(-447.28, -64.4) * mm});
            skLineSegment(sketch, "E330", {"start": v(-447.28, -64.4) * mm, "end": v(-446.44, -64.98) * mm});
            skLineSegment(sketch, "E331", {"start": v(-446.44, -64.98) * mm, "end": v(-445.6, -65.55) * mm});
            skLineSegment(sketch, "E332", {"start": v(-445.6, -65.55) * mm, "end": v(-444.78, -66.13) * mm});
            skLineSegment(sketch, "E333", {"start": v(-444.78, -66.13) * mm, "end": v(-443.94, -66.7) * mm});
            skLineSegment(sketch, "E334", {"start": v(-443.94, -66.7) * mm, "end": v(-443.11, -67.27) * mm});
            skLineSegment(sketch, "E335", {"start": v(-443.11, -67.27) * mm, "end": v(-442.28, -67.85) * mm});
            skLineSegment(sketch, "E336", {"start": v(-442.28, -67.85) * mm, "end": v(-441.45, -68.42) * mm});
            skLineSegment(sketch, "E337", {"start": v(-441.45, -68.42) * mm, "end": v(-440.61, -69) * mm});
            skLineSegment(sketch, "E338", {"start": v(-440.61, -69) * mm, "end": v(-439.78, -69.58) * mm});
            skLineSegment(sketch, "E339", {"start": v(-439.78, -69.58) * mm, "end": v(-438.95, -70.15) * mm});
            skLineSegment(sketch, "E340", {"start": v(-438.95, -70.15) * mm, "end": v(-438.12, -70.73) * mm});
            skLineSegment(sketch, "E341", {"start": v(-438.12, -70.73) * mm, "end": v(-437.3, -71.31) * mm});
            skLineSegment(sketch, "E342", {"start": v(-437.3, -71.31) * mm, "end": v(-436.46, -71.9) * mm});
            skLineSegment(sketch, "E343", {"start": v(-436.46, -71.9) * mm, "end": v(-435.64, -72.47) * mm});
            skLineSegment(sketch, "E344", {"start": v(-435.64, -72.47) * mm, "end": v(-434.8, -73.05) * mm});
            skLineSegment(sketch, "E345", {"start": v(-434.8, -73.05) * mm, "end": v(-433.98, -73.63) * mm});
            skLineSegment(sketch, "E346", {"start": v(-433.98, -73.63) * mm, "end": v(-433.15, -74.21) * mm});
            skLineSegment(sketch, "E347", {"start": v(-433.15, -74.21) * mm, "end": v(-432.33, -74.8) * mm});
            skLineSegment(sketch, "E348", {"start": v(-432.33, -74.8) * mm, "end": v(-431.5, -75.38) * mm});
            skLineSegment(sketch, "E349", {"start": v(-431.5, -75.38) * mm, "end": v(-430.65, -75.98) * mm});
            skLineSegment(sketch, "E350", {"start": v(-430.65, -75.98) * mm, "end": v(-429.8, -76.57) * mm});
            skLineSegment(sketch, "E351", {"start": v(-429.8, -76.57) * mm, "end": v(-428.95, -77.17) * mm});
            skLineSegment(sketch, "E352", {"start": v(-428.95, -77.17) * mm, "end": v(-428.1, -77.76) * mm});
            skLineSegment(sketch, "E353", {"start": v(-428.1, -77.76) * mm, "end": v(-427.25, -78.35) * mm});
            skLineSegment(sketch, "E354", {"start": v(-427.25, -78.35) * mm, "end": v(-426.4, -78.94) * mm});
            skLineSegment(sketch, "E355", {"start": v(-426.4, -78.94) * mm, "end": v(-425.54, -79.52) * mm});
            skLineSegment(sketch, "E356", {"start": v(-425.54, -79.52) * mm, "end": v(-424.69, -80.1) * mm});
            skLineSegment(sketch, "E357", {"start": v(-424.69, -80.1) * mm, "end": v(-423.83, -80.7) * mm});
            skLineSegment(sketch, "E358", {"start": v(-423.83, -80.7) * mm, "end": v(-422.97, -81.28) * mm});
            skLineSegment(sketch, "E359", {"start": v(-422.97, -81.28) * mm, "end": v(-422.12, -81.86) * mm});
            skLineSegment(sketch, "E360", {"start": v(-422.12, -81.86) * mm, "end": v(-421.26, -82.44) * mm});
            skLineSegment(sketch, "E361", {"start": v(-421.26, -82.44) * mm, "end": v(-420.4, -83.02) * mm});
            skLineSegment(sketch, "E362", {"start": v(-420.4, -83.02) * mm, "end": v(-419.54, -83.6) * mm});
            skLineSegment(sketch, "E363", {"start": v(-419.54, -83.6) * mm, "end": v(-418.68, -84.17) * mm});
            skLineSegment(sketch, "E364", {"start": v(-418.68, -84.17) * mm, "end": v(-417.81, -84.75) * mm});
            skLineSegment(sketch, "E365", {"start": v(-417.81, -84.75) * mm, "end": v(-416.95, -85.32) * mm});
            skLineSegment(sketch, "E366", {"start": v(-416.95, -85.32) * mm, "end": v(-416.09, -85.9) * mm});
            skLineSegment(sketch, "E367", {"start": v(-416.09, -85.9) * mm, "end": v(-415.23, -86.47) * mm});
            skLineSegment(sketch, "E368", {"start": v(-415.23, -86.47) * mm, "end": v(-414.36, -87.05) * mm});
            skLineSegment(sketch, "E369", {"start": v(-414.36, -87.05) * mm, "end": v(-413.5, -87.62) * mm});
            skLineSegment(sketch, "E370", {"start": v(-413.5, -87.62) * mm, "end": v(-412.72, -88.16) * mm});
            skLineSegment(sketch, "E371", {"start": v(-412.72, -88.16) * mm, "end": v(-411.9, -88.75) * mm});
            skLineSegment(sketch, "E372", {"start": v(-411.9, -88.75) * mm, "end": v(-411.05, -89.35) * mm});
            skLineSegment(sketch, "E373", {"start": v(-411.05, -89.35) * mm, "end": v(-410.17, -89.95) * mm});
            skLineSegment(sketch, "E374", {"start": v(-410.17, -89.95) * mm, "end": v(-409.27, -90.52) * mm});
            skLineSegment(sketch, "E375", {"start": v(-409.27, -90.52) * mm, "end": v(-408.34, -91.03) * mm});
            skLineSegment(sketch, "E376", {"start": v(-408.34, -91.03) * mm, "end": v(-407.4, -91.46) * mm});
            skLineSegment(sketch, "E377", {"start": v(-407.4, -91.46) * mm, "end": v(-406.45, -91.79) * mm});
            skLineSegment(sketch, "E378", {"start": v(-406.45, -91.79) * mm, "end": v(-405.48, -91.98) * mm});
            skLineSegment(sketch, "E379", {"start": v(-405.48, -91.98) * mm, "end": v(-404.5, -92.02) * mm});
            skLineSegment(sketch, "E380", {"start": v(-404.5, -92.02) * mm, "end": v(-403.58, -91.9) * mm});
            skLineSegment(sketch, "E381", {"start": v(-403.58, -91.9) * mm, "end": v(-402.66, -91.66) * mm});
            skLineSegment(sketch, "E382", {"start": v(-402.66, -91.66) * mm, "end": v(-401.76, -91.3) * mm});
            skLineSegment(sketch, "E383", {"start": v(-401.76, -91.3) * mm, "end": v(-400.87, -90.85) * mm});
            skLineSegment(sketch, "E384", {"start": v(-400.87, -90.85) * mm, "end": v(-400, -90.32) * mm});
            skLineSegment(sketch, "E385", {"start": v(-400, -90.32) * mm, "end": v(-399.14, -89.73) * mm});
            skLineSegment(sketch, "E386", {"start": v(-399.14, -89.73) * mm, "end": v(-398.3, -89.1) * mm});
            skLineSegment(sketch, "E387", {"start": v(-398.3, -89.1) * mm, "end": v(-397.49, -88.45) * mm});
            skLineSegment(sketch, "E388", {"start": v(-397.49, -88.45) * mm, "end": v(-396.7, -87.8) * mm});
            skLineSegment(sketch, "E389", {"start": v(-396.7, -87.8) * mm, "end": v(-395.94, -87.14) * mm});
            skLineSegment(sketch, "E390", {"start": v(-395.94, -87.14) * mm, "end": v(-395.2, -86.53) * mm});
            skLineSegment(sketch, "E391", {"start": v(-395.2, -86.53) * mm, "end": v(-394.5, -85.96) * mm});
            skLineSegment(sketch, "E392", {"start": v(-394.5, -85.96) * mm, "end": v(-393.7, -85.33) * mm});
            skLineSegment(sketch, "E393", {"start": v(-393.7, -85.33) * mm, "end": v(-392.9, -84.72) * mm});
            skLineSegment(sketch, "E394", {"start": v(-392.9, -84.72) * mm, "end": v(-392.1, -84.1) * mm});
            skLineSegment(sketch, "E395", {"start": v(-392.1, -84.1) * mm, "end": v(-391.3, -83.5) * mm});
            skLineSegment(sketch, "E396", {"start": v(-391.3, -83.5) * mm, "end": v(-390.5, -82.88) * mm});
            skLineSegment(sketch, "E397", {"start": v(-390.5, -82.88) * mm, "end": v(-389.68, -82.28) * mm});
            skLineSegment(sketch, "E398", {"start": v(-389.68, -82.28) * mm, "end": v(-388.87, -81.68) * mm});
            skLineSegment(sketch, "E399", {"start": v(-388.87, -81.68) * mm, "end": v(-388.06, -81.08) * mm});
            skLineSegment(sketch, "E400", {"start": v(-388.06, -81.08) * mm, "end": v(-387.24, -80.49) * mm});
            skLineSegment(sketch, "E401", {"start": v(-387.24, -80.49) * mm, "end": v(-386.42, -79.9) * mm});
            skLineSegment(sketch, "E402", {"start": v(-386.42, -79.9) * mm, "end": v(-385.6, -79.3) * mm});
            skLineSegment(sketch, "E403", {"start": v(-385.6, -79.3) * mm, "end": v(-384.78, -78.72) * mm});
            skLineSegment(sketch, "E404", {"start": v(-384.78, -78.72) * mm, "end": v(-383.96, -78.13) * mm});
            skLineSegment(sketch, "E405", {"start": v(-383.96, -78.13) * mm, "end": v(-383.13, -77.55) * mm});
            skLineSegment(sketch, "E406", {"start": v(-383.13, -77.55) * mm, "end": v(-382.3, -76.97) * mm});
            skLineSegment(sketch, "E407", {"start": v(-382.3, -76.97) * mm, "end": v(-381.48, -76.39) * mm});
            skLineSegment(sketch, "E408", {"start": v(-381.48, -76.39) * mm, "end": v(-380.65, -75.8) * mm});
            skLineSegment(sketch, "E409", {"start": v(-380.65, -75.8) * mm, "end": v(-379.82, -75.23) * mm});
            skLineSegment(sketch, "E410", {"start": v(-379.82, -75.23) * mm, "end": v(-379, -74.66) * mm});
            skLineSegment(sketch, "E411", {"start": v(-379, -74.66) * mm, "end": v(-378.16, -74.08) * mm});
            skLineSegment(sketch, "E412", {"start": v(-378.16, -74.08) * mm, "end": v(-377.33, -73.5) * mm});
            skLineSegment(sketch, "E413", {"start": v(-377.33, -73.5) * mm, "end": v(-376.5, -72.93) * mm});
            skLineSegment(sketch, "E414", {"start": v(-376.5, -72.93) * mm, "end": v(-375.69, -72.37) * mm});
            skLineSegment(sketch, "E415", {"start": v(-375.69, -72.37) * mm, "end": v(-374.87, -71.81) * mm});
            skLineSegment(sketch, "E416", {"start": v(-374.87, -71.81) * mm, "end": v(-374.05, -71.25) * mm});
            skLineSegment(sketch, "E417", {"start": v(-374.05, -71.25) * mm, "end": v(-373.24, -70.7) * mm});
            skLineSegment(sketch, "E418", {"start": v(-373.24, -70.7) * mm, "end": v(-372.41, -70.13) * mm});
            skLineSegment(sketch, "E419", {"start": v(-372.41, -70.13) * mm, "end": v(-371.6, -69.58) * mm});
            skLineSegment(sketch, "E420", {"start": v(-371.6, -69.58) * mm, "end": v(-370.77, -69.02) * mm});
            skLineSegment(sketch, "E421", {"start": v(-370.77, -69.02) * mm, "end": v(-369.94, -68.46) * mm});
            skLineSegment(sketch, "E422", {"start": v(-369.94, -68.46) * mm, "end": v(-369.1, -67.9) * mm});
            skLineSegment(sketch, "E423", {"start": v(-369.1, -67.9) * mm, "end": v(-368.28, -67.35) * mm});
            skLineSegment(sketch, "E424", {"start": v(-368.28, -67.35) * mm, "end": v(-367.45, -66.8) * mm});
            skLineSegment(sketch, "E425", {"start": v(-367.45, -66.8) * mm, "end": v(-366.61, -66.24) * mm});
            skLineSegment(sketch, "E426", {"start": v(-366.61, -66.24) * mm, "end": v(-365.77, -65.68) * mm});
            skLineSegment(sketch, "E427", {"start": v(-365.77, -65.68) * mm, "end": v(-364.94, -65.13) * mm});
            skLineSegment(sketch, "E428", {"start": v(-364.94, -65.13) * mm, "end": v(-364.1, -64.58) * mm});
            skLineSegment(sketch, "E429", {"start": v(-364.1, -64.58) * mm, "end": v(-363.25, -64.03) * mm});
            skLineSegment(sketch, "E430", {"start": v(-363.25, -64.03) * mm, "end": v(-362.4, -63.48) * mm});
            skLineSegment(sketch, "E431", {"start": v(-362.4, -63.48) * mm, "end": v(-361.56, -62.93) * mm});
            skLineSegment(sketch, "E432", {"start": v(-361.56, -62.93) * mm, "end": v(-360.71, -62.39) * mm});
            skLineSegment(sketch, "E433", {"start": v(-360.71, -62.39) * mm, "end": v(-359.86, -61.84) * mm});
            skLineSegment(sketch, "E434", {"start": v(-359.86, -61.84) * mm, "end": v(-359.01, -61.3) * mm});
            skLineSegment(sketch, "E435", {"start": v(-359.01, -61.3) * mm, "end": v(-358.16, -60.76) * mm});
            skLineSegment(sketch, "E436", {"start": v(-358.16, -60.76) * mm, "end": v(-357.3, -60.22) * mm});
            skLineSegment(sketch, "E437", {"start": v(-357.3, -60.22) * mm, "end": v(-356.44, -59.69) * mm});
            skLineSegment(sketch, "E438", {"start": v(-356.44, -59.69) * mm, "end": v(-355.59, -59.15) * mm});
            skLineSegment(sketch, "E439", {"start": v(-355.59, -59.15) * mm, "end": v(-354.72, -58.62) * mm});
            skLineSegment(sketch, "E440", {"start": v(-354.72, -58.62) * mm, "end": v(-353.86, -58.09) * mm});
            skLineSegment(sketch, "E441", {"start": v(-353.86, -58.09) * mm, "end": v(-353, -57.56) * mm});
            skLineSegment(sketch, "E442", {"start": v(-353, -57.56) * mm, "end": v(-352.13, -57.04) * mm});
            skLineSegment(sketch, "E443", {"start": v(-352.13, -57.04) * mm, "end": v(-351.26, -56.51) * mm});
            skLineSegment(sketch, "E444", {"start": v(-351.26, -56.51) * mm, "end": v(-350.4, -56) * mm});
            skLineSegment(sketch, "E445", {"start": v(-350.4, -56) * mm, "end": v(-349.52, -55.47) * mm});
            skLineSegment(sketch, "E446", {"start": v(-349.52, -55.47) * mm, "end": v(-348.65, -54.96) * mm});
            skLineSegment(sketch, "E447", {"start": v(-348.65, -54.96) * mm, "end": v(-347.77, -54.45) * mm});
            skLineSegment(sketch, "E448", {"start": v(-347.77, -54.45) * mm, "end": v(-346.9, -53.94) * mm});
            skLineSegment(sketch, "E449", {"start": v(-346.9, -53.94) * mm, "end": v(-346.02, -53.43) * mm});
            skLineSegment(sketch, "E450", {"start": v(-346.02, -53.43) * mm, "end": v(-345.14, -52.93) * mm});
            skLineSegment(sketch, "E451", {"start": v(-345.14, -52.93) * mm, "end": v(-344.25, -52.43) * mm});
            skLineSegment(sketch, "E452", {"start": v(-344.25, -52.43) * mm, "end": v(-343.37, -51.93) * mm});
            skLineSegment(sketch, "E453", {"start": v(-343.37, -51.93) * mm, "end": v(-342.48, -51.44) * mm});
            skLineSegment(sketch, "E454", {"start": v(-342.48, -51.44) * mm, "end": v(-341.6, -50.95) * mm});
            skLineSegment(sketch, "E455", {"start": v(-341.6, -50.95) * mm, "end": v(-340.7, -50.46) * mm});
            skLineSegment(sketch, "E456", {"start": v(-340.7, -50.46) * mm, "end": v(-339.82, -49.98) * mm});
            skLineSegment(sketch, "E457", {"start": v(-339.82, -49.98) * mm, "end": v(-338.93, -49.5) * mm});
            skLineSegment(sketch, "E458", {"start": v(-338.93, -49.5) * mm, "end": v(-338.03, -49.02) * mm});
            skLineSegment(sketch, "E459", {"start": v(-338.03, -49.02) * mm, "end": v(-337.14, -48.55) * mm});
            skLineSegment(sketch, "E460", {"start": v(-337.14, -48.55) * mm, "end": v(-336.24, -48.08) * mm});
            skLineSegment(sketch, "E461", {"start": v(-336.24, -48.08) * mm, "end": v(-335.34, -47.62) * mm});
            skLineSegment(sketch, "E462", {"start": v(-335.34, -47.62) * mm, "end": v(-334.44, -47.16) * mm});
            skLineSegment(sketch, "E463", {"start": v(-334.44, -47.16) * mm, "end": v(-333.54, -46.7) * mm});
            skLineSegment(sketch, "E464", {"start": v(-333.54, -46.7) * mm, "end": v(-332.64, -46.25) * mm});
            skLineSegment(sketch, "E465", {"start": v(-332.64, -46.25) * mm, "end": v(-331.73, -45.8) * mm});
            skLineSegment(sketch, "E466", {"start": v(-331.73, -45.8) * mm, "end": v(-330.82, -45.37) * mm});
            skLineSegment(sketch, "E467", {"start": v(-330.82, -45.37) * mm, "end": v(-329.92, -44.93) * mm});
            skLineSegment(sketch, "E468", {"start": v(-329.92, -44.93) * mm, "end": v(-329, -44.5) * mm});
            skLineSegment(sketch, "E469", {"start": v(-329, -44.5) * mm, "end": v(-328.1, -44.07) * mm});
            skLineSegment(sketch, "E470", {"start": v(-328.1, -44.07) * mm, "end": v(-327.18, -43.65) * mm});
            skLineSegment(sketch, "E471", {"start": v(-327.18, -43.65) * mm, "end": v(-326.27, -43.23) * mm});
            skLineSegment(sketch, "E472", {"start": v(-326.27, -43.23) * mm, "end": v(-325.35, -42.81) * mm});
            skLineSegment(sketch, "E473", {"start": v(-325.35, -42.81) * mm, "end": v(-324.44, -42.4) * mm});
            skLineSegment(sketch, "E474", {"start": v(-324.44, -42.4) * mm, "end": v(-323.52, -42) * mm});
            skLineSegment(sketch, "E475", {"start": v(-323.52, -42) * mm, "end": v(-322.6, -41.6) * mm});
            skLineSegment(sketch, "E476", {"start": v(-322.6, -41.6) * mm, "end": v(-321.67, -41.21) * mm});
            skLineSegment(sketch, "E477", {"start": v(-321.67, -41.21) * mm, "end": v(-320.75, -40.83) * mm});
            skLineSegment(sketch, "E478", {"start": v(-320.75, -40.83) * mm, "end": v(-319.83, -40.45) * mm});
            skLineSegment(sketch, "E479", {"start": v(-319.83, -40.45) * mm, "end": v(-318.9, -40.07) * mm});
            skLineSegment(sketch, "E480", {"start": v(-318.9, -40.07) * mm, "end": v(-317.97, -39.7) * mm});
            skLineSegment(sketch, "E481", {"start": v(-317.97, -39.7) * mm, "end": v(-317.04, -39.34) * mm});
            skLineSegment(sketch, "E482", {"start": v(-317.04, -39.34) * mm, "end": v(-316.11, -38.98) * mm});
            skLineSegment(sketch, "E483", {"start": v(-316.11, -38.98) * mm, "end": v(-315.18, -38.63) * mm});
            skLineSegment(sketch, "E484", {"start": v(-315.18, -38.63) * mm, "end": v(-314.25, -38.28) * mm});
            skLineSegment(sketch, "E485", {"start": v(-314.25, -38.28) * mm, "end": v(-313.31, -37.94) * mm});
            skLineSegment(sketch, "E486", {"start": v(-313.31, -37.94) * mm, "end": v(-312.38, -37.6) * mm});
            skLineSegment(sketch, "E487", {"start": v(-312.38, -37.6) * mm, "end": v(-311.44, -37.28) * mm});
            skLineSegment(sketch, "E488", {"start": v(-311.44, -37.28) * mm, "end": v(-310.5, -36.96) * mm});
            skLineSegment(sketch, "E489", {"start": v(-310.5, -36.96) * mm, "end": v(-311.14, -36.21) * mm});
            skLineSegment(sketch, "E490", {"start": v(-311.14, -36.21) * mm, "end": v(-311.82, -35.5) * mm});
            skLineSegment(sketch, "E491", {"start": v(-311.82, -35.5) * mm, "end": v(-312.52, -34.8) * mm});
            skLineSegment(sketch, "E492", {"start": v(-312.52, -34.8) * mm, "end": v(-313.24, -34.13) * mm});
            skLineSegment(sketch, "E493", {"start": v(-313.24, -34.13) * mm, "end": v(-313.98, -33.48) * mm});
            skLineSegment(sketch, "E494", {"start": v(-313.98, -33.48) * mm, "end": v(-314.75, -32.85) * mm});
            skLineSegment(sketch, "E495", {"start": v(-314.75, -32.85) * mm, "end": v(-315.53, -32.24) * mm});
            skLineSegment(sketch, "E496", {"start": v(-315.53, -32.24) * mm, "end": v(-316.33, -31.64) * mm});
            skLineSegment(sketch, "E497", {"start": v(-316.33, -31.64) * mm, "end": v(-317.14, -31.06) * mm});
            skLineSegment(sketch, "E498", {"start": v(-317.14, -31.06) * mm, "end": v(-317.97, -30.5) * mm});
            skLineSegment(sketch, "E499", {"start": v(-317.97, -30.5) * mm, "end": v(-318.8, -29.94) * mm});
            skLineSegment(sketch, "E500", {"start": v(-318.8, -29.94) * mm, "end": v(-319.64, -29.39) * mm});
            skLineSegment(sketch, "E501", {"start": v(-319.64, -29.39) * mm, "end": v(-320.48, -28.84) * mm});
            skLineSegment(sketch, "E502", {"start": v(-320.48, -28.84) * mm, "end": v(-321.32, -28.3) * mm});
            skLineSegment(sketch, "E503", {"start": v(-321.32, -28.3) * mm, "end": v(-322.17, -27.77) * mm});
            skLineSegment(sketch, "E504", {"start": v(-322.17, -27.77) * mm, "end": v(-323.01, -27.24) * mm});
            skLineSegment(sketch, "E505", {"start": v(-323.01, -27.24) * mm, "end": v(-323.85, -26.7) * mm});
            skLineSegment(sketch, "E506", {"start": v(-323.85, -26.7) * mm, "end": v(-324.68, -26.16) * mm});
            skLineSegment(sketch, "E507", {"start": v(-324.68, -26.16) * mm, "end": v(-325.5, -25.62) * mm});
            skLineSegment(sketch, "E508", {"start": v(-325.5, -25.62) * mm, "end": v(-353.5, -6.96) * mm});
            skLineSegment(sketch, "E509", {"start": v(-353.5, -6.96) * mm, "end": v(-354.34, -6.4) * mm});
            skLineSegment(sketch, "E510", {"start": v(-354.34, -6.4) * mm, "end": v(-355.18, -5.83) * mm});
            skLineSegment(sketch, "E511", {"start": v(-355.18, -5.83) * mm, "end": v(-356.03, -5.27) * mm});
            skLineSegment(sketch, "E512", {"start": v(-356.03, -5.27) * mm, "end": v(-356.87, -4.71) * mm});
            skLineSegment(sketch, "E513", {"start": v(-356.87, -4.71) * mm, "end": v(-357.71, -4.15) * mm});
            skLineSegment(sketch, "E514", {"start": v(-357.71, -4.15) * mm, "end": v(-358.56, -3.6) * mm});
            skLineSegment(sketch, "E515", {"start": v(-358.56, -3.6) * mm, "end": v(-359.4, -3.04) * mm});
            skLineSegment(sketch, "E516", {"start": v(-359.4, -3.04) * mm, "end": v(-360.24, -2.48) * mm});
            skLineSegment(sketch, "E517", {"start": v(-360.24, -2.48) * mm, "end": v(-361.09, -1.92) * mm});
            skLineSegment(sketch, "E518", {"start": v(-361.09, -1.92) * mm, "end": v(-361.93, -1.36) * mm});
            skLineSegment(sketch, "E519", {"start": v(-361.93, -1.36) * mm, "end": v(-362.78, -0.8) * mm});
            skLineSegment(sketch, "E520", {"start": v(-362.78, -0.8) * mm, "end": v(-363.62, -0.24) * mm});
            skLineSegment(sketch, "E521", {"start": v(-363.62, -0.24) * mm, "end": v(-364.47, 0.32) * mm});
            skLineSegment(sketch, "E522", {"start": v(-364.47, 0.32) * mm, "end": v(-365.31, 0.87) * mm});
            skLineSegment(sketch, "E523", {"start": v(-365.31, 0.87) * mm, "end": v(-366.16, 1.43) * mm});
            skLineSegment(sketch, "E524", {"start": v(-366.16, 1.43) * mm, "end": v(-367, 1.99) * mm});
            skLineSegment(sketch, "E525", {"start": v(-367, 1.99) * mm, "end": v(-367.85, 2.55) * mm});
            skLineSegment(sketch, "E526", {"start": v(-367.85, 2.55) * mm, "end": v(-368.7, 3.1) * mm});
            skLineSegment(sketch, "E527", {"start": v(-368.7, 3.1) * mm, "end": v(-369.54, 3.66) * mm});
            skLineSegment(sketch, "E528", {"start": v(-369.54, 3.66) * mm, "end": v(-370.38, 4.22) * mm});
            skLineSegment(sketch, "E529", {"start": v(-370.38, 4.22) * mm, "end": v(-371.23, 4.78) * mm});
            skLineSegment(sketch, "E530", {"start": v(-371.23, 4.78) * mm, "end": v(-372.07, 5.34) * mm});
            skLineSegment(sketch, "E531", {"start": v(-372.07, 5.34) * mm, "end": v(-372.92, 5.9) * mm});
            skLineSegment(sketch, "E532", {"start": v(-372.92, 5.9) * mm, "end": v(-373.76, 6.45) * mm});
            skLineSegment(sketch, "E533", {"start": v(-373.76, 6.45) * mm, "end": v(-374.6, 7) * mm});
            skLineSegment(sketch, "E534", {"start": v(-374.6, 7) * mm, "end": v(-375.45, 7.57) * mm});
            skLineSegment(sketch, "E535", {"start": v(-375.45, 7.57) * mm, "end": v(-376.3, 8.13) * mm});
            skLineSegment(sketch, "E536", {"start": v(-376.3, 8.13) * mm, "end": v(-377.14, 8.68) * mm});
            skLineSegment(sketch, "E537", {"start": v(-377.14, 8.68) * mm, "end": v(-377.98, 9.24) * mm});
            skLineSegment(sketch, "E538", {"start": v(-377.98, 9.24) * mm, "end": v(-378.83, 9.8) * mm});
            skLineSegment(sketch, "E539", {"start": v(-378.83, 9.8) * mm, "end": v(-379.67, 10.36) * mm});
            skLineSegment(sketch, "E540", {"start": v(-379.67, 10.36) * mm, "end": v(-380.52, 10.92) * mm});
            skLineSegment(sketch, "E541", {"start": v(-380.52, 10.92) * mm, "end": v(-381.36, 11.48) * mm});
            skLineSegment(sketch, "E542", {"start": v(-381.36, 11.48) * mm, "end": v(-382.2, 12.04) * mm});
            skLineSegment(sketch, "E543", {"start": v(-382.2, 12.04) * mm, "end": v(-383.05, 12.6) * mm});
            skLineSegment(sketch, "E544", {"start": v(-383.05, 12.6) * mm, "end": v(-383.89, 13.16) * mm});
            skLineSegment(sketch, "E545", {"start": v(-383.89, 13.16) * mm, "end": v(-384.73, 13.72) * mm});
            skLineSegment(sketch, "E546", {"start": v(-384.73, 13.72) * mm, "end": v(-385.57, 14.29) * mm});
            skLineSegment(sketch, "E547", {"start": v(-385.57, 14.29) * mm, "end": v(-386.42, 14.85) * mm});
            skLineSegment(sketch, "E548", {"start": v(-386.42, 14.85) * mm, "end": v(-387.26, 15.41) * mm});
            skLineSegment(sketch, "E549", {"start": v(-387.26, 15.41) * mm, "end": v(-388.1, 15.97) * mm});
            skLineSegment(sketch, "E550", {"start": v(-388.1, 15.97) * mm, "end": v(-388.94, 16.54) * mm});
            skLineSegment(sketch, "E551", {"start": v(-388.94, 16.54) * mm, "end": v(-389.78, 17.1) * mm});
            skLineSegment(sketch, "E552", {"start": v(-389.78, 17.1) * mm, "end": v(-390.62, 17.67) * mm});
            skLineSegment(sketch, "E553", {"start": v(-390.62, 17.67) * mm, "end": v(-391.46, 18.23) * mm});
            skLineSegment(sketch, "E554", {"start": v(-391.46, 18.23) * mm, "end": v(-392.3, 18.8) * mm});
            skLineSegment(sketch, "E555", {"start": v(-392.3, 18.8) * mm, "end": v(-393.14, 19.37) * mm});
            skLineSegment(sketch, "E556", {"start": v(-393.14, 19.37) * mm, "end": v(-393.98, 19.93) * mm});
            skLineSegment(sketch, "E557", {"start": v(-393.98, 19.93) * mm, "end": v(-394.82, 20.5) * mm});
            skLineSegment(sketch, "E558", {"start": v(-394.82, 20.5) * mm, "end": v(-395.65, 21.07) * mm});
            skLineSegment(sketch, "E559", {"start": v(-395.65, 21.07) * mm, "end": v(-396.5, 21.64) * mm});
            skLineSegment(sketch, "E560", {"start": v(-396.5, 21.64) * mm, "end": v(-397.33, 22.2) * mm});
            skLineSegment(sketch, "E561", {"start": v(-397.33, 22.2) * mm, "end": v(-398.16, 22.78) * mm});
            skLineSegment(sketch, "E562", {"start": v(-398.16, 22.78) * mm, "end": v(-399, 23.35) * mm});
            skLineSegment(sketch, "E563", {"start": v(-399, 23.35) * mm, "end": v(-399.83, 23.92) * mm});
            skLineSegment(sketch, "E564", {"start": v(-399.83, 23.92) * mm, "end": v(-400.67, 24.5) * mm});
            skLineSegment(sketch, "E565", {"start": v(-400.67, 24.5) * mm, "end": v(-401.5, 25.07) * mm});
            skLineSegment(sketch, "E566", {"start": v(-401.5, 25.07) * mm, "end": v(-402.3, 25.63) * mm});
            skLineSegment(sketch, "E567", {"start": v(-402.3, 25.63) * mm, "end": v(-403.11, 26.19) * mm});
            skLineSegment(sketch, "E568", {"start": v(-403.11, 26.19) * mm, "end": v(-403.92, 26.76) * mm});
            skLineSegment(sketch, "E569", {"start": v(-403.92, 26.76) * mm, "end": v(-404.72, 27.33) * mm});
            skLineSegment(sketch, "E570", {"start": v(-404.72, 27.33) * mm, "end": v(-405.53, 27.9) * mm});
            skLineSegment(sketch, "E571", {"start": v(-405.53, 27.9) * mm, "end": v(-406.34, 28.48) * mm});
            skLineSegment(sketch, "E572", {"start": v(-406.34, 28.48) * mm, "end": v(-407.15, 29.06) * mm});
            skLineSegment(sketch, "E573", {"start": v(-407.15, 29.06) * mm, "end": v(-407.95, 29.64) * mm});
            skLineSegment(sketch, "E574", {"start": v(-407.95, 29.64) * mm, "end": v(-408.76, 30.23) * mm});
            skLineSegment(sketch, "E575", {"start": v(-408.76, 30.23) * mm, "end": v(-409.58, 30.82) * mm});
            skLineSegment(sketch, "E576", {"start": v(-409.58, 30.82) * mm, "end": v(-410.39, 31.4) * mm});
            skLineSegment(sketch, "E577", {"start": v(-410.39, 31.4) * mm, "end": v(-411.2, 32) * mm});
            skLineSegment(sketch, "E578", {"start": v(-411.2, 32) * mm, "end": v(-412.01, 32.59) * mm});
            skLineSegment(sketch, "E579", {"start": v(-412.01, 32.59) * mm, "end": v(-412.83, 33.18) * mm});
            skLineSegment(sketch, "E580", {"start": v(-412.83, 33.18) * mm, "end": v(-413.65, 33.76) * mm});
            skLineSegment(sketch, "E581", {"start": v(-413.65, 33.76) * mm, "end": v(-414.46, 34.35) * mm});
            skLineSegment(sketch, "E582", {"start": v(-414.46, 34.35) * mm, "end": v(-415.28, 34.94) * mm});
            skLineSegment(sketch, "E583", {"start": v(-415.28, 34.94) * mm, "end": v(-416.1, 35.53) * mm});
            skLineSegment(sketch, "E584", {"start": v(-416.1, 35.53) * mm, "end": v(-416.93, 36.11) * mm});
            skLineSegment(sketch, "E585", {"start": v(-416.93, 36.11) * mm, "end": v(-417.75, 36.7) * mm});
            skLineSegment(sketch, "E586", {"start": v(-417.75, 36.7) * mm, "end": v(-418.58, 37.27) * mm});
            skLineSegment(sketch, "E587", {"start": v(-418.58, 37.27) * mm, "end": v(-419.4, 37.85) * mm});
            skLineSegment(sketch, "E588", {"start": v(-419.4, 37.85) * mm, "end": v(-420.24, 38.42) * mm});
            skLineSegment(sketch, "E589", {"start": v(-420.24, 38.42) * mm, "end": v(-421.07, 38.99) * mm});
            skLineSegment(sketch, "E590", {"start": v(-421.07, 38.99) * mm, "end": v(-421.9, 39.55) * mm});
            skLineSegment(sketch, "E591", {"start": v(-421.9, 39.55) * mm, "end": v(-422.74, 40.1) * mm});
            skLineSegment(sketch, "E592", {"start": v(-422.74, 40.1) * mm, "end": v(-423.58, 40.66) * mm});
            skLineSegment(sketch, "E593", {"start": v(-423.58, 40.66) * mm, "end": v(-424.42, 41.2) * mm});
            skLineSegment(sketch, "E594", {"start": v(-424.42, 41.2) * mm, "end": v(-425.27, 41.75) * mm});
            skLineSegment(sketch, "E595", {"start": v(-425.27, 41.75) * mm, "end": v(-426.11, 42.28) * mm});
            skLineSegment(sketch, "E596", {"start": v(-426.11, 42.28) * mm, "end": v(-426.96, 42.81) * mm});
            skLineSegment(sketch, "E597", {"start": v(-426.96, 42.81) * mm, "end": v(-427.81, 43.33) * mm});
            skLineSegment(sketch, "E598", {"start": v(-427.81, 43.33) * mm, "end": v(-428.67, 43.84) * mm});
            skLineSegment(sketch, "E599", {"start": v(-428.67, 43.84) * mm, "end": v(-429.53, 44.35) * mm});
            skLineSegment(sketch, "E600", {"start": v(-429.53, 44.35) * mm, "end": v(-430.39, 44.85) * mm});
            skLineSegment(sketch, "E601", {"start": v(-430.39, 44.85) * mm, "end": v(-431.25, 45.33) * mm});
            skLineSegment(sketch, "E602", {"start": v(-431.25, 45.33) * mm, "end": v(-432.12, 45.8) * mm});
            skLineSegment(sketch, "E603", {"start": v(-432.12, 45.8) * mm, "end": v(-432.99, 46.28) * mm});
            skLineSegment(sketch, "E604", {"start": v(-432.99, 46.28) * mm, "end": v(-433.86, 46.74) * mm});
            skLineSegment(sketch, "E605", {"start": v(-433.86, 46.74) * mm, "end": v(-434.74, 47.18) * mm});
            skLineSegment(sketch, "E606", {"start": v(-434.74, 47.18) * mm, "end": v(-435.62, 47.62) * mm});
            skLineSegment(sketch, "E607", {"start": v(-435.62, 47.62) * mm, "end": v(-436.5, 48.04) * mm});
            skLineSegment(sketch, "E608", {"start": v(-436.5, 48.04) * mm, "end": v(-435.72, 48.58) * mm});
            skLineSegment(sketch, "E609", {"start": v(-435.72, 48.58) * mm, "end": v(-434.9, 49.16) * mm});
            skLineSegment(sketch, "E610", {"start": v(-434.9, 49.16) * mm, "end": v(-434.06, 49.74) * mm});
            skLineSegment(sketch, "E611", {"start": v(-434.06, 49.74) * mm, "end": v(-433.19, 50.3) * mm});
            skLineSegment(sketch, "E612", {"start": v(-433.19, 50.3) * mm, "end": v(-432.3, 50.82) * mm});
            skLineSegment(sketch, "E613", {"start": v(-432.3, 50.82) * mm, "end": v(-431.37, 51.25) * mm});
            skLineSegment(sketch, "E614", {"start": v(-431.37, 51.25) * mm, "end": v(-430.43, 51.59) * mm});
            skLineSegment(sketch, "E615", {"start": v(-430.43, 51.59) * mm, "end": v(-429.48, 51.79) * mm});
            skLineSegment(sketch, "E616", {"start": v(-429.48, 51.79) * mm, "end": v(-428.5, 51.83) * mm});
            skLineSegment(sketch, "E617", {"start": v(-428.5, 51.83) * mm, "end": v(-427.53, 51.7) * mm});
            skLineSegment(sketch, "E618", {"start": v(-427.53, 51.7) * mm, "end": v(-426.58, 51.43) * mm});
            skLineSegment(sketch, "E619", {"start": v(-426.58, 51.43) * mm, "end": v(-425.64, 51.04) * mm});
            skLineSegment(sketch, "E620", {"start": v(-425.64, 51.04) * mm, "end": v(-424.73, 50.56) * mm});
            skLineSegment(sketch, "E621", {"start": v(-424.73, 50.56) * mm, "end": v(-423.83, 50.02) * mm});
            skLineSegment(sketch, "E622", {"start": v(-423.83, 50.02) * mm, "end": v(-422.96, 49.43) * mm});
            skLineSegment(sketch, "E623", {"start": v(-422.96, 49.43) * mm, "end": v(-422.11, 48.84) * mm});
            skLineSegment(sketch, "E624", {"start": v(-422.11, 48.84) * mm, "end": v(-421.3, 48.25) * mm});
            skLineSegment(sketch, "E625", {"start": v(-421.3, 48.25) * mm, "end": v(-420.5, 47.71) * mm});
            skLineSegment(sketch, "E626", {"start": v(-420.5, 47.71) * mm, "end": v(-404.5, 37.04) * mm});
            skLineSegment(sketch, "E627", {"start": v(-404.5, 37.04) * mm, "end": v(-403.7, 36.5) * mm});
            skLineSegment(sketch, "E628", {"start": v(-403.7, 36.5) * mm, "end": v(-402.9, 35.96) * mm});
            skLineSegment(sketch, "E629", {"start": v(-402.9, 35.96) * mm, "end": v(-402.1, 35.4) * mm});
            skLineSegment(sketch, "E630", {"start": v(-402.1, 35.4) * mm, "end": v(-401.28, 34.84) * mm});
            skLineSegment(sketch, "E631", {"start": v(-401.28, 34.84) * mm, "end": v(-400.48, 34.28) * mm});
            skLineSegment(sketch, "E632", {"start": v(-400.48, 34.28) * mm, "end": v(-399.67, 33.7) * mm});
            skLineSegment(sketch, "E633", {"start": v(-399.67, 33.7) * mm, "end": v(-398.86, 33.13) * mm});
            skLineSegment(sketch, "E634", {"start": v(-398.86, 33.13) * mm, "end": v(-398.04, 32.55) * mm});
            skLineSegment(sketch, "E635", {"start": v(-398.04, 32.55) * mm, "end": v(-397.23, 31.96) * mm});
            skLineSegment(sketch, "E636", {"start": v(-397.23, 31.96) * mm, "end": v(-396.41, 31.38) * mm});
            skLineSegment(sketch, "E637", {"start": v(-396.41, 31.38) * mm, "end": v(-395.6, 30.79) * mm});
            skLineSegment(sketch, "E638", {"start": v(-395.6, 30.79) * mm, "end": v(-394.77, 30.2) * mm});
            skLineSegment(sketch, "E639", {"start": v(-394.77, 30.2) * mm, "end": v(-393.95, 29.61) * mm});
            skLineSegment(sketch, "E640", {"start": v(-393.95, 29.61) * mm, "end": v(-393.13, 29.02) * mm});
            skLineSegment(sketch, "E641", {"start": v(-393.13, 29.02) * mm, "end": v(-392.3, 28.44) * mm});
            skLineSegment(sketch, "E642", {"start": v(-392.3, 28.44) * mm, "end": v(-391.47, 27.85) * mm});
            skLineSegment(sketch, "E643", {"start": v(-391.47, 27.85) * mm, "end": v(-390.63, 27.27) * mm});
            skLineSegment(sketch, "E644", {"start": v(-390.63, 27.27) * mm, "end": v(-389.8, 26.7) * mm});
            skLineSegment(sketch, "E645", {"start": v(-389.8, 26.7) * mm, "end": v(-388.96, 26.12) * mm});
            skLineSegment(sketch, "E646", {"start": v(-388.96, 26.12) * mm, "end": v(-388.12, 25.55) * mm});
            skLineSegment(sketch, "E647", {"start": v(-388.12, 25.55) * mm, "end": v(-387.27, 25) * mm});
            skLineSegment(sketch, "E648", {"start": v(-387.27, 25) * mm, "end": v(-386.42, 24.44) * mm});
            skLineSegment(sketch, "E649", {"start": v(-386.42, 24.44) * mm, "end": v(-385.57, 23.89) * mm});
            skLineSegment(sketch, "E650", {"start": v(-385.57, 23.89) * mm, "end": v(-384.72, 23.35) * mm});
            skLineSegment(sketch, "E651", {"start": v(-384.72, 23.35) * mm, "end": v(-383.86, 22.81) * mm});
            skLineSegment(sketch, "E652", {"start": v(-383.86, 22.81) * mm, "end": v(-383, 22.3) * mm});
            skLineSegment(sketch, "E653", {"start": v(-383, 22.3) * mm, "end": v(-382.13, 21.78) * mm});
            skLineSegment(sketch, "E654", {"start": v(-382.13, 21.78) * mm, "end": v(-381.26, 21.28) * mm});
            skLineSegment(sketch, "E655", {"start": v(-381.26, 21.28) * mm, "end": v(-380.39, 20.8) * mm});
            skLineSegment(sketch, "E656", {"start": v(-380.39, 20.8) * mm, "end": v(-379.51, 20.32) * mm});
            skLineSegment(sketch, "E657", {"start": v(-379.51, 20.32) * mm, "end": v(-378.63, 19.85) * mm});
            skLineSegment(sketch, "E658", {"start": v(-378.63, 19.85) * mm, "end": v(-377.74, 19.4) * mm});
            skLineSegment(sketch, "E659", {"start": v(-377.74, 19.4) * mm, "end": v(-376.86, 18.97) * mm});
            skLineSegment(sketch, "E660", {"start": v(-376.86, 18.97) * mm, "end": v(-375.96, 18.55) * mm});
            skLineSegment(sketch, "E661", {"start": v(-375.96, 18.55) * mm, "end": v(-375.06, 18.15) * mm});
            skLineSegment(sketch, "E662", {"start": v(-375.06, 18.15) * mm, "end": v(-374.16, 17.76) * mm});
            skLineSegment(sketch, "E663", {"start": v(-374.16, 17.76) * mm, "end": v(-373.25, 17.4) * mm});
            skLineSegment(sketch, "E664", {"start": v(-373.25, 17.4) * mm, "end": v(-372.34, 17.04) * mm});
            skLineSegment(sketch, "E665", {"start": v(-372.34, 17.04) * mm, "end": v(-371.42, 16.71) * mm});
            skLineSegment(sketch, "E666", {"start": v(-371.42, 16.71) * mm, "end": v(-370.5, 16.4) * mm});
            skLineSegment(sketch, "E667", {"start": v(-370.5, 16.4) * mm, "end": v(-369.6, 16.13) * mm});
            skLineSegment(sketch, "E668", {"start": v(-369.6, 16.13) * mm, "end": v(-368.7, 15.87) * mm});
            skLineSegment(sketch, "E669", {"start": v(-368.7, 15.87) * mm, "end": v(-367.78, 15.64) * mm});
            skLineSegment(sketch, "E670", {"start": v(-367.78, 15.64) * mm, "end": v(-366.85, 15.43) * mm});
            skLineSegment(sketch, "E671", {"start": v(-366.85, 15.43) * mm, "end": v(-365.9, 15.24) * mm});
            skLineSegment(sketch, "E672", {"start": v(-365.9, 15.24) * mm, "end": v(-364.95, 15.08) * mm});
            skLineSegment(sketch, "E673", {"start": v(-364.95, 15.08) * mm, "end": v(-363.99, 14.93) * mm});
            skLineSegment(sketch, "E674", {"start": v(-363.99, 14.93) * mm, "end": v(-363.01, 14.8) * mm});
            skLineSegment(sketch, "E675", {"start": v(-363.01, 14.8) * mm, "end": v(-362.03, 14.7) * mm});
            skLineSegment(sketch, "E676", {"start": v(-362.03, 14.7) * mm, "end": v(-361.04, 14.6) * mm});
            skLineSegment(sketch, "E677", {"start": v(-361.04, 14.6) * mm, "end": v(-360.05, 14.54) * mm});
            skLineSegment(sketch, "E678", {"start": v(-360.05, 14.54) * mm, "end": v(-359.04, 14.49) * mm});
            skLineSegment(sketch, "E679", {"start": v(-359.04, 14.49) * mm, "end": v(-358.04, 14.45) * mm});
            skLineSegment(sketch, "E680", {"start": v(-358.04, 14.45) * mm, "end": v(-357.03, 14.44) * mm});
            skLineSegment(sketch, "E681", {"start": v(-357.03, 14.44) * mm, "end": v(-356.01, 14.44) * mm});
            skLineSegment(sketch, "E682", {"start": v(-356.01, 14.44) * mm, "end": v(-355, 14.46) * mm});
            skLineSegment(sketch, "E683", {"start": v(-355, 14.46) * mm, "end": v(-353.97, 14.49) * mm});
            skLineSegment(sketch, "E684", {"start": v(-353.97, 14.49) * mm, "end": v(-352.95, 14.54) * mm});
            skLineSegment(sketch, "E685", {"start": v(-352.95, 14.54) * mm, "end": v(-351.93, 14.6) * mm});
            skLineSegment(sketch, "E686", {"start": v(-351.93, 14.6) * mm, "end": v(-350.9, 14.68) * mm});
            skLineSegment(sketch, "E687", {"start": v(-350.9, 14.68) * mm, "end": v(-349.88, 14.78) * mm});
            skLineSegment(sketch, "E688", {"start": v(-349.88, 14.78) * mm, "end": v(-348.86, 14.88) * mm});
            skLineSegment(sketch, "E689", {"start": v(-348.86, 14.88) * mm, "end": v(-347.84, 15) * mm});
            skLineSegment(sketch, "E690", {"start": v(-347.84, 15) * mm, "end": v(-346.83, 15.14) * mm});
            skLineSegment(sketch, "E691", {"start": v(-346.83, 15.14) * mm, "end": v(-345.82, 15.28) * mm});
            skLineSegment(sketch, "E692", {"start": v(-345.82, 15.28) * mm, "end": v(-344.81, 15.44) * mm});
            skLineSegment(sketch, "E693", {"start": v(-344.81, 15.44) * mm, "end": v(-343.81, 15.6) * mm});
            skLineSegment(sketch, "E694", {"start": v(-343.81, 15.6) * mm, "end": v(-342.82, 15.8) * mm});
            skLineSegment(sketch, "E695", {"start": v(-342.82, 15.8) * mm, "end": v(-341.83, 15.98) * mm});
            skLineSegment(sketch, "E696", {"start": v(-341.83, 15.98) * mm, "end": v(-340.85, 16.18) * mm});
            skLineSegment(sketch, "E697", {"start": v(-340.85, 16.18) * mm, "end": v(-339.88, 16.4) * mm});
            skLineSegment(sketch, "E698", {"start": v(-339.88, 16.4) * mm, "end": v(-338.91, 16.62) * mm});
            skLineSegment(sketch, "E699", {"start": v(-338.91, 16.62) * mm, "end": v(-337.96, 16.85) * mm});
            skLineSegment(sketch, "E700", {"start": v(-337.96, 16.85) * mm, "end": v(-337.02, 17.08) * mm});
            skLineSegment(sketch, "E701", {"start": v(-337.02, 17.08) * mm, "end": v(-336.09, 17.33) * mm});
            skLineSegment(sketch, "E702", {"start": v(-336.09, 17.33) * mm, "end": v(-335.17, 17.58) * mm});
            skLineSegment(sketch, "E703", {"start": v(-335.17, 17.58) * mm, "end": v(-334.27, 17.85) * mm});
            skLineSegment(sketch, "E704", {"start": v(-334.27, 17.85) * mm, "end": v(-333.38, 18.11) * mm});
            skLineSegment(sketch, "E705", {"start": v(-333.38, 18.11) * mm, "end": v(-332.5, 18.39) * mm});
            skLineSegment(sketch, "E706", {"start": v(-332.5, 18.39) * mm, "end": v(-331.74, 18.62) * mm});
            skLineSegment(sketch, "E707", {"start": v(-331.74, 18.62) * mm, "end": v(-330.91, 18.87) * mm});
            skLineSegment(sketch, "E708", {"start": v(-330.91, 18.87) * mm, "end": v(-330.04, 19.12) * mm});
            skLineSegment(sketch, "E709", {"start": v(-330.04, 19.12) * mm, "end": v(-329.12, 19.39) * mm});
            skLineSegment(sketch, "E710", {"start": v(-329.12, 19.39) * mm, "end": v(-328.17, 19.66) * mm});
            skLineSegment(sketch, "E711", {"start": v(-328.17, 19.66) * mm, "end": v(-327.18, 19.95) * mm});
            skLineSegment(sketch, "E712", {"start": v(-327.18, 19.95) * mm, "end": v(-326.17, 20.25) * mm});
            skLineSegment(sketch, "E713", {"start": v(-326.17, 20.25) * mm, "end": v(-325.15, 20.57) * mm});
            skLineSegment(sketch, "E714", {"start": v(-325.15, 20.57) * mm, "end": v(-324.12, 20.9) * mm});
            skLineSegment(sketch, "E715", {"start": v(-324.12, 20.9) * mm, "end": v(-323.09, 21.26) * mm});
            skLineSegment(sketch, "E716", {"start": v(-323.09, 21.26) * mm, "end": v(-322.06, 21.63) * mm});
            skLineSegment(sketch, "E717", {"start": v(-322.06, 21.63) * mm, "end": v(-321.05, 22.03) * mm});
            skLineSegment(sketch, "E718", {"start": v(-321.05, 22.03) * mm, "end": v(-320.06, 22.44) * mm});
            skLineSegment(sketch, "E719", {"start": v(-320.06, 22.44) * mm, "end": v(-319.1, 22.88) * mm});
            skLineSegment(sketch, "E720", {"start": v(-319.1, 22.88) * mm, "end": v(-318.17, 23.35) * mm});
            skLineSegment(sketch, "E721", {"start": v(-318.17, 23.35) * mm, "end": v(-317.28, 23.84) * mm});
            skLineSegment(sketch, "E722", {"start": v(-317.28, 23.84) * mm, "end": v(-316.44, 24.36) * mm});
            skLineSegment(sketch, "E723", {"start": v(-316.44, 24.36) * mm, "end": v(-315.66, 24.9) * mm});
            skLineSegment(sketch, "E724", {"start": v(-315.66, 24.9) * mm, "end": v(-314.95, 25.49) * mm});
            skLineSegment(sketch, "E725", {"start": v(-314.95, 25.49) * mm, "end": v(-314.3, 26.1) * mm});
            skLineSegment(sketch, "E726", {"start": v(-314.3, 26.1) * mm, "end": v(-313.73, 26.74) * mm});
            skLineSegment(sketch, "E727", {"start": v(-313.73, 26.74) * mm, "end": v(-313.25, 27.42) * mm});
            skLineSegment(sketch, "E728", {"start": v(-313.25, 27.42) * mm, "end": v(-312.85, 28.3) * mm});
            skLineSegment(sketch, "E729", {"start": v(-312.85, 28.3) * mm, "end": v(-312.74, 29.15) * mm});
            skLineSegment(sketch, "E730", {"start": v(-312.74, 29.15) * mm, "end": v(-312.9, 29.95) * mm});
            skLineSegment(sketch, "E731", {"start": v(-312.9, 29.95) * mm, "end": v(-313.26, 30.7) * mm});
            skLineSegment(sketch, "E732", {"start": v(-313.26, 30.7) * mm, "end": v(-313.78, 31.4) * mm});
            skLineSegment(sketch, "E733", {"start": v(-313.78, 31.4) * mm, "end": v(-314.42, 32.04) * mm});
            skLineSegment(sketch, "E734", {"start": v(-314.42, 32.04) * mm, "end": v(-315.12, 32.64) * mm});
            skLineSegment(sketch, "E735", {"start": v(-315.12, 32.64) * mm, "end": v(-315.84, 33.2) * mm});
            skLineSegment(sketch, "E736", {"start": v(-315.84, 33.2) * mm, "end": v(-316.52, 33.7) * mm});
            skLineSegment(sketch, "E737", {"start": v(-316.52, 33.7) * mm, "end": v(-317.34, 34.29) * mm});
            skLineSegment(sketch, "E738", {"start": v(-317.34, 34.29) * mm, "end": v(-318.17, 34.87) * mm});
            skLineSegment(sketch, "E739", {"start": v(-318.17, 34.87) * mm, "end": v(-319, 35.45) * mm});
            skLineSegment(sketch, "E740", {"start": v(-319, 35.45) * mm, "end": v(-319.84, 36.03) * mm});
            skLineSegment(sketch, "E741", {"start": v(-319.84, 36.03) * mm, "end": v(-320.68, 36.6) * mm});
            skLineSegment(sketch, "E742", {"start": v(-320.68, 36.6) * mm, "end": v(-321.52, 37.16) * mm});
            skLineSegment(sketch, "E743", {"start": v(-321.52, 37.16) * mm, "end": v(-322.37, 37.72) * mm});
            skLineSegment(sketch, "E744", {"start": v(-322.37, 37.72) * mm, "end": v(-323.22, 38.28) * mm});
            skLineSegment(sketch, "E745", {"start": v(-323.22, 38.28) * mm, "end": v(-324.06, 38.83) * mm});
            skLineSegment(sketch, "E746", {"start": v(-324.06, 38.83) * mm, "end": v(-324.91, 39.39) * mm});
            skLineSegment(sketch, "E747", {"start": v(-324.91, 39.39) * mm, "end": v(-325.76, 39.94) * mm});
            skLineSegment(sketch, "E748", {"start": v(-325.76, 39.94) * mm, "end": v(-326.61, 40.5) * mm});
            skLineSegment(sketch, "E749", {"start": v(-326.61, 40.5) * mm, "end": v(-327.46, 41.05) * mm});
            skLineSegment(sketch, "E750", {"start": v(-327.46, 41.05) * mm, "end": v(-328.3, 41.61) * mm});
            skLineSegment(sketch, "E751", {"start": v(-328.3, 41.61) * mm, "end": v(-329.15, 42.17) * mm});
            skLineSegment(sketch, "E752", {"start": v(-329.15, 42.17) * mm, "end": v(-330, 42.74) * mm});
            skLineSegment(sketch, "E753", {"start": v(-330, 42.74) * mm, "end": v(-330.84, 43.31) * mm});
            skLineSegment(sketch, "E754", {"start": v(-330.84, 43.31) * mm, "end": v(-331.67, 43.89) * mm});
            skLineSegment(sketch, "E755", {"start": v(-331.67, 43.89) * mm, "end": v(-332.5, 44.47) * mm});
            skLineSegment(sketch, "E756", {"start": v(-332.5, 44.47) * mm, "end": v(-333.32, 45.05) * mm});
            skLineSegment(sketch, "E757", {"start": v(-333.32, 45.05) * mm, "end": v(-334.15, 45.63) * mm});
            skLineSegment(sketch, "E758", {"start": v(-334.15, 45.63) * mm, "end": v(-334.97, 46.21) * mm});
            skLineSegment(sketch, "E759", {"start": v(-334.97, 46.21) * mm, "end": v(-335.8, 46.8) * mm});
            skLineSegment(sketch, "E760", {"start": v(-335.8, 46.8) * mm, "end": v(-336.63, 47.37) * mm});
            skLineSegment(sketch, "E761", {"start": v(-336.63, 47.37) * mm, "end": v(-337.45, 47.95) * mm});
            skLineSegment(sketch, "E762", {"start": v(-337.45, 47.95) * mm, "end": v(-338.28, 48.53) * mm});
            skLineSegment(sketch, "E763", {"start": v(-338.28, 48.53) * mm, "end": v(-339.11, 49.1) * mm});
            skLineSegment(sketch, "E764", {"start": v(-339.11, 49.1) * mm, "end": v(-339.94, 49.68) * mm});
            skLineSegment(sketch, "E765", {"start": v(-339.94, 49.68) * mm, "end": v(-340.77, 50.26) * mm});
            skLineSegment(sketch, "E766", {"start": v(-340.77, 50.26) * mm, "end": v(-341.6, 50.83) * mm});
            skLineSegment(sketch, "E767", {"start": v(-341.6, 50.83) * mm, "end": v(-342.43, 51.4) * mm});
            skLineSegment(sketch, "E768", {"start": v(-342.43, 51.4) * mm, "end": v(-343.26, 51.98) * mm});
            skLineSegment(sketch, "E769", {"start": v(-343.26, 51.98) * mm, "end": v(-344.1, 52.55) * mm});
            skLineSegment(sketch, "E770", {"start": v(-344.1, 52.55) * mm, "end": v(-344.93, 53.12) * mm});
            skLineSegment(sketch, "E771", {"start": v(-344.93, 53.12) * mm, "end": v(-345.76, 53.7) * mm});
            skLineSegment(sketch, "E772", {"start": v(-345.76, 53.7) * mm, "end": v(-346.6, 54.27) * mm});
            skLineSegment(sketch, "E773", {"start": v(-346.6, 54.27) * mm, "end": v(-347.43, 54.84) * mm});
            skLineSegment(sketch, "E774", {"start": v(-347.43, 54.84) * mm, "end": v(-348.26, 55.4) * mm});
            skLineSegment(sketch, "E775", {"start": v(-348.26, 55.4) * mm, "end": v(-349.1, 55.98) * mm});
            skLineSegment(sketch, "E776", {"start": v(-349.1, 55.98) * mm, "end": v(-349.93, 56.55) * mm});
            skLineSegment(sketch, "E777", {"start": v(-349.93, 56.55) * mm, "end": v(-350.77, 57.11) * mm});
            skLineSegment(sketch, "E778", {"start": v(-350.77, 57.11) * mm, "end": v(-351.6, 57.68) * mm});
            skLineSegment(sketch, "E779", {"start": v(-351.6, 57.68) * mm, "end": v(-352.44, 58.25) * mm});
            skLineSegment(sketch, "E780", {"start": v(-352.44, 58.25) * mm, "end": v(-353.27, 58.82) * mm});
            skLineSegment(sketch, "E781", {"start": v(-353.27, 58.82) * mm, "end": v(-354.11, 59.38) * mm});
            skLineSegment(sketch, "E782", {"start": v(-354.11, 59.38) * mm, "end": v(-354.95, 59.95) * mm});
            skLineSegment(sketch, "E783", {"start": v(-354.95, 59.95) * mm, "end": v(-355.79, 60.52) * mm});
            skLineSegment(sketch, "E784", {"start": v(-355.79, 60.52) * mm, "end": v(-356.62, 61.08) * mm});
            skLineSegment(sketch, "E785", {"start": v(-356.62, 61.08) * mm, "end": v(-357.46, 61.65) * mm});
            skLineSegment(sketch, "E786", {"start": v(-357.46, 61.65) * mm, "end": v(-358.3, 62.21) * mm});
            skLineSegment(sketch, "E787", {"start": v(-358.3, 62.21) * mm, "end": v(-359.14, 62.78) * mm});
            skLineSegment(sketch, "E788", {"start": v(-359.14, 62.78) * mm, "end": v(-359.98, 63.34) * mm});
            skLineSegment(sketch, "E789", {"start": v(-359.98, 63.34) * mm, "end": v(-360.82, 63.9) * mm});
            skLineSegment(sketch, "E790", {"start": v(-360.82, 63.9) * mm, "end": v(-361.66, 64.47) * mm});
            skLineSegment(sketch, "E791", {"start": v(-361.66, 64.47) * mm, "end": v(-362.5, 65.03) * mm});
            skLineSegment(sketch, "E792", {"start": v(-362.5, 65.03) * mm, "end": v(-363.33, 65.6) * mm});
            skLineSegment(sketch, "E793", {"start": v(-363.33, 65.6) * mm, "end": v(-364.17, 66.16) * mm});
            skLineSegment(sketch, "E794", {"start": v(-364.17, 66.16) * mm, "end": v(-365.01, 66.72) * mm});
            skLineSegment(sketch, "E795", {"start": v(-365.01, 66.72) * mm, "end": v(-365.85, 67.28) * mm});
            skLineSegment(sketch, "E796", {"start": v(-365.85, 67.28) * mm, "end": v(-366.7, 67.84) * mm});
            skLineSegment(sketch, "E797", {"start": v(-366.7, 67.84) * mm, "end": v(-367.54, 68.4) * mm});
            skLineSegment(sketch, "E798", {"start": v(-367.54, 68.4) * mm, "end": v(-368.38, 68.96) * mm});
            skLineSegment(sketch, "E799", {"start": v(-368.38, 68.96) * mm, "end": v(-369.22, 69.53) * mm});
            skLineSegment(sketch, "E800", {"start": v(-369.22, 69.53) * mm, "end": v(-370.06, 70.09) * mm});
            skLineSegment(sketch, "E801", {"start": v(-370.06, 70.09) * mm, "end": v(-370.9, 70.65) * mm});
            skLineSegment(sketch, "E802", {"start": v(-370.9, 70.65) * mm, "end": v(-371.74, 71.2) * mm});
            skLineSegment(sketch, "E803", {"start": v(-371.74, 71.2) * mm, "end": v(-372.58, 71.77) * mm});
            skLineSegment(sketch, "E804", {"start": v(-372.58, 71.77) * mm, "end": v(-373.42, 72.33) * mm});
            skLineSegment(sketch, "E805", {"start": v(-373.42, 72.33) * mm, "end": v(-374.26, 72.89) * mm});
            skLineSegment(sketch, "E806", {"start": v(-374.26, 72.89) * mm, "end": v(-375.1, 73.45) * mm});
            skLineSegment(sketch, "E807", {"start": v(-375.1, 73.45) * mm, "end": v(-375.94, 74) * mm});
            skLineSegment(sketch, "E808", {"start": v(-375.94, 74) * mm, "end": v(-376.78, 74.57) * mm});
            skLineSegment(sketch, "E809", {"start": v(-376.78, 74.57) * mm, "end": v(-377.62, 75.13) * mm});
            skLineSegment(sketch, "E810", {"start": v(-377.62, 75.13) * mm, "end": v(-378.46, 75.69) * mm});
            skLineSegment(sketch, "E811", {"start": v(-378.46, 75.69) * mm, "end": v(-379.3, 76.25) * mm});
            skLineSegment(sketch, "E812", {"start": v(-379.3, 76.25) * mm, "end": v(-380.14, 76.8) * mm});
            skLineSegment(sketch, "E813", {"start": v(-380.14, 76.8) * mm, "end": v(-380.98, 77.36) * mm});
            skLineSegment(sketch, "E814", {"start": v(-380.98, 77.36) * mm, "end": v(-381.82, 77.92) * mm});
            skLineSegment(sketch, "E815", {"start": v(-381.82, 77.92) * mm, "end": v(-382.66, 78.48) * mm});
            skLineSegment(sketch, "E816", {"start": v(-382.66, 78.48) * mm, "end": v(-383.5, 79.04) * mm});
            skLineSegment(sketch, "E817", {"start": v(-383.5, 79.04) * mm, "end": v(-397.5, 88.38) * mm});
            skLineSegment(sketch, "E818", {"start": v(-397.5, 88.38) * mm, "end": v(-398.28, 88.91) * mm});
            skLineSegment(sketch, "E819", {"start": v(-398.28, 88.91) * mm, "end": v(-399.1, 89.48) * mm});
            skLineSegment(sketch, "E820", {"start": v(-399.1, 89.48) * mm, "end": v(-399.94, 90.07) * mm});
            skLineSegment(sketch, "E821", {"start": v(-399.94, 90.07) * mm, "end": v(-400.81, 90.62) * mm});
            skLineSegment(sketch, "E822", {"start": v(-400.81, 90.62) * mm, "end": v(-401.7, 91.13) * mm});
            skLineSegment(sketch, "E823", {"start": v(-401.7, 91.13) * mm, "end": v(-402.62, 91.55) * mm});
            skLineSegment(sketch, "E824", {"start": v(-402.62, 91.55) * mm, "end": v(-403.55, 91.86) * mm});
            skLineSegment(sketch, "E825", {"start": v(-403.55, 91.86) * mm, "end": v(-404.5, 92.02) * mm});
            skLineSegment(sketch, "E826", {"start": v(-404.5, 92.02) * mm, "end": v(-405.53, 92) * mm});
            skLineSegment(sketch, "E827", {"start": v(-405.53, 92) * mm, "end": v(-406.52, 91.8) * mm});
            skLineSegment(sketch, "E828", {"start": v(-406.52, 91.8) * mm, "end": v(-407.48, 91.41) * mm});
            skLineSegment(sketch, "E829", {"start": v(-407.48, 91.41) * mm, "end": v(-408.4, 90.9) * mm});
            skLineSegment(sketch, "E830", {"start": v(-408.4, 90.9) * mm, "end": v(-409.28, 90.3) * mm});
            skLineSegment(sketch, "E831", {"start": v(-409.28, 90.3) * mm, "end": v(-410.14, 89.64) * mm});
            skLineSegment(sketch, "E832", {"start": v(-410.14, 89.64) * mm, "end": v(-410.96, 88.95) * mm});
            skLineSegment(sketch, "E833", {"start": v(-410.96, 88.95) * mm, "end": v(-411.75, 88.27) * mm});
            skLineSegment(sketch, "E834", {"start": v(-411.75, 88.27) * mm, "end": v(-412.5, 87.63) * mm});
            skLineSegment(sketch, "E835", {"start": v(-412.5, 87.63) * mm, "end": v(-413.29, 86.98) * mm});
            skLineSegment(sketch, "E836", {"start": v(-413.29, 86.98) * mm, "end": v(-414.07, 86.33) * mm});
            skLineSegment(sketch, "E837", {"start": v(-414.07, 86.33) * mm, "end": v(-414.85, 85.68) * mm});
            skLineSegment(sketch, "E838", {"start": v(-414.85, 85.68) * mm, "end": v(-415.64, 85.04) * mm});
            skLineSegment(sketch, "E839", {"start": v(-415.64, 85.04) * mm, "end": v(-416.42, 84.39) * mm});
            skLineSegment(sketch, "E840", {"start": v(-416.42, 84.39) * mm, "end": v(-417.2, 83.74) * mm});
            skLineSegment(sketch, "E841", {"start": v(-417.2, 83.74) * mm, "end": v(-418, 83.1) * mm});
            skLineSegment(sketch, "E842", {"start": v(-418, 83.1) * mm, "end": v(-418.79, 82.46) * mm});
            skLineSegment(sketch, "E843", {"start": v(-418.79, 82.46) * mm, "end": v(-419.58, 81.82) * mm});
            skLineSegment(sketch, "E844", {"start": v(-419.58, 81.82) * mm, "end": v(-420.37, 81.18) * mm});
            skLineSegment(sketch, "E845", {"start": v(-420.37, 81.18) * mm, "end": v(-421.16, 80.55) * mm});
            skLineSegment(sketch, "E846", {"start": v(-421.16, 80.55) * mm, "end": v(-421.96, 79.92) * mm});
            skLineSegment(sketch, "E847", {"start": v(-421.96, 79.92) * mm, "end": v(-422.76, 79.3) * mm});
            skLineSegment(sketch, "E848", {"start": v(-422.76, 79.3) * mm, "end": v(-423.57, 78.67) * mm});
            skLineSegment(sketch, "E849", {"start": v(-423.57, 78.67) * mm, "end": v(-424.38, 78.05) * mm});
            skLineSegment(sketch, "E850", {"start": v(-424.38, 78.05) * mm, "end": v(-425.2, 77.44) * mm});
            skLineSegment(sketch, "E851", {"start": v(-425.2, 77.44) * mm, "end": v(-426.01, 76.84) * mm});
            skLineSegment(sketch, "E852", {"start": v(-426.01, 76.84) * mm, "end": v(-426.83, 76.24) * mm});
            skLineSegment(sketch, "E853", {"start": v(-426.83, 76.24) * mm, "end": v(-427.66, 75.65) * mm});
            skLineSegment(sketch, "E854", {"start": v(-427.66, 75.65) * mm, "end": v(-428.5, 75.07) * mm});
            skLineSegment(sketch, "E855", {"start": v(-428.5, 75.07) * mm, "end": v(-429.33, 74.5) * mm});
            skLineSegment(sketch, "E856", {"start": v(-429.33, 74.5) * mm, "end": v(-430.15, 73.93) * mm});
            skLineSegment(sketch, "E857", {"start": v(-430.15, 73.93) * mm, "end": v(-430.98, 73.36) * mm});
            skLineSegment(sketch, "E858", {"start": v(-430.98, 73.36) * mm, "end": v(-431.8, 72.8) * mm});
            skLineSegment(sketch, "E859", {"start": v(-431.8, 72.8) * mm, "end": v(-432.64, 72.23) * mm});
            skLineSegment(sketch, "E860", {"start": v(-432.64, 72.23) * mm, "end": v(-433.47, 71.66) * mm});
            skLineSegment(sketch, "E861", {"start": v(-433.47, 71.66) * mm, "end": v(-434.3, 71.1) * mm});
            skLineSegment(sketch, "E862", {"start": v(-434.3, 71.1) * mm, "end": v(-435.14, 70.53) * mm});
            skLineSegment(sketch, "E863", {"start": v(-435.14, 70.53) * mm, "end": v(-435.97, 69.97) * mm});
            skLineSegment(sketch, "E864", {"start": v(-435.97, 69.97) * mm, "end": v(-436.8, 69.4) * mm});
            skLineSegment(sketch, "E865", {"start": v(-436.8, 69.4) * mm, "end": v(-437.64, 68.85) * mm});
            skLineSegment(sketch, "E866", {"start": v(-437.64, 68.85) * mm, "end": v(-438.48, 68.29) * mm});
            skLineSegment(sketch, "E867", {"start": v(-438.48, 68.29) * mm, "end": v(-439.32, 67.73) * mm});
            skLineSegment(sketch, "E868", {"start": v(-439.32, 67.73) * mm, "end": v(-440.16, 67.18) * mm});
            skLineSegment(sketch, "E869", {"start": v(-440.16, 67.18) * mm, "end": v(-441, 66.62) * mm});
            skLineSegment(sketch, "E870", {"start": v(-441, 66.62) * mm, "end": v(-441.84, 66.07) * mm});
            skLineSegment(sketch, "E871", {"start": v(-441.84, 66.07) * mm, "end": v(-442.69, 65.52) * mm});
            skLineSegment(sketch, "E872", {"start": v(-442.69, 65.52) * mm, "end": v(-443.53, 64.97) * mm});
            skLineSegment(sketch, "E873", {"start": v(-443.53, 64.97) * mm, "end": v(-444.38, 64.42) * mm});
            skLineSegment(sketch, "E874", {"start": v(-444.38, 64.42) * mm, "end": v(-445.23, 63.88) * mm});
            skLineSegment(sketch, "E875", {"start": v(-445.23, 63.88) * mm, "end": v(-446.08, 63.34) * mm});
            skLineSegment(sketch, "E876", {"start": v(-446.08, 63.34) * mm, "end": v(-446.93, 62.8) * mm});
            skLineSegment(sketch, "E877", {"start": v(-446.93, 62.8) * mm, "end": v(-447.78, 62.26) * mm});
            skLineSegment(sketch, "E878", {"start": v(-447.78, 62.26) * mm, "end": v(-448.63, 61.72) * mm});
            skLineSegment(sketch, "E879", {"start": v(-448.63, 61.72) * mm, "end": v(-449.49, 61.19) * mm});
            skLineSegment(sketch, "E880", {"start": v(-449.49, 61.19) * mm, "end": v(-450.35, 60.66) * mm});
            skLineSegment(sketch, "E881", {"start": v(-450.35, 60.66) * mm, "end": v(-451.2, 60.13) * mm});
            skLineSegment(sketch, "E882", {"start": v(-451.2, 60.13) * mm, "end": v(-452.06, 59.6) * mm});
            skLineSegment(sketch, "E883", {"start": v(-452.06, 59.6) * mm, "end": v(-452.92, 59.08) * mm});
            skLineSegment(sketch, "E884", {"start": v(-452.92, 59.08) * mm, "end": v(-453.79, 58.56) * mm});
            skLineSegment(sketch, "E885", {"start": v(-453.79, 58.56) * mm, "end": v(-454.65, 58.04) * mm});
            skLineSegment(sketch, "E886", {"start": v(-454.65, 58.04) * mm, "end": v(-455.52, 57.53) * mm});
            skLineSegment(sketch, "E887", {"start": v(-455.52, 57.53) * mm, "end": v(-456.38, 57.01) * mm});
            skLineSegment(sketch, "E888", {"start": v(-456.38, 57.01) * mm, "end": v(-457.25, 56.5) * mm});
            skLineSegment(sketch, "E889", {"start": v(-457.25, 56.5) * mm, "end": v(-458.12, 56) * mm});
            skLineSegment(sketch, "E890", {"start": v(-458.12, 56) * mm, "end": v(-459, 55.5) * mm});
            skLineSegment(sketch, "E891", {"start": v(-459, 55.5) * mm, "end": v(-459.87, 55) * mm});
            skLineSegment(sketch, "E892", {"start": v(-459.87, 55) * mm, "end": v(-460.75, 54.5) * mm});
            skLineSegment(sketch, "E893", {"start": v(-460.75, 54.5) * mm, "end": v(-461.62, 54) * mm});
            skLineSegment(sketch, "E894", {"start": v(-461.62, 54) * mm, "end": v(-462.5, 53.52) * mm});
            skLineSegment(sketch, "E895", {"start": v(-462.5, 53.52) * mm, "end": v(-463.38, 53.03) * mm});
            skLineSegment(sketch, "E896", {"start": v(-463.38, 53.03) * mm, "end": v(-464.27, 52.55) * mm});
            skLineSegment(sketch, "E897", {"start": v(-464.27, 52.55) * mm, "end": v(-465.15, 52.08) * mm});
            skLineSegment(sketch, "E898", {"start": v(-465.15, 52.08) * mm, "end": v(-466.04, 51.6) * mm});
            skLineSegment(sketch, "E899", {"start": v(-466.04, 51.6) * mm, "end": v(-466.93, 51.13) * mm});
            skLineSegment(sketch, "E900", {"start": v(-466.93, 51.13) * mm, "end": v(-467.82, 50.67) * mm});
            skLineSegment(sketch, "E901", {"start": v(-467.82, 50.67) * mm, "end": v(-468.7, 50.2) * mm});
            skLineSegment(sketch, "E902", {"start": v(-468.7, 50.2) * mm, "end": v(-469.6, 49.75) * mm});
            skLineSegment(sketch, "E903", {"start": v(-469.6, 49.75) * mm, "end": v(-470.5, 49.3) * mm});
            skLineSegment(sketch, "E904", {"start": v(-470.5, 49.3) * mm, "end": v(-471.36, 48.86) * mm});
            skLineSegment(sketch, "E905", {"start": v(-471.36, 48.86) * mm, "end": v(-472.24, 48.44) * mm});
            skLineSegment(sketch, "E906", {"start": v(-472.24, 48.44) * mm, "end": v(-473.14, 48.02) * mm});
            skLineSegment(sketch, "E907", {"start": v(-473.14, 48.02) * mm, "end": v(-474.04, 47.6) * mm});
            skLineSegment(sketch, "E908", {"start": v(-474.04, 47.6) * mm, "end": v(-474.95, 47.2) * mm});
            skLineSegment(sketch, "E909", {"start": v(-474.95, 47.2) * mm, "end": v(-475.88, 46.8) * mm});
            skLineSegment(sketch, "E910", {"start": v(-475.88, 46.8) * mm, "end": v(-476.81, 46.39) * mm});
            skLineSegment(sketch, "E911", {"start": v(-476.81, 46.39) * mm, "end": v(-477.75, 45.98) * mm});
            skLineSegment(sketch, "E912", {"start": v(-477.75, 45.98) * mm, "end": v(-478.7, 45.58) * mm});
            skLineSegment(sketch, "E913", {"start": v(-478.7, 45.58) * mm, "end": v(-479.65, 45.18) * mm});
            skLineSegment(sketch, "E914", {"start": v(-479.65, 45.18) * mm, "end": v(-480.6, 44.77) * mm});
            skLineSegment(sketch, "E915", {"start": v(-480.6, 44.77) * mm, "end": v(-481.56, 44.37) * mm});
            skLineSegment(sketch, "E916", {"start": v(-481.56, 44.37) * mm, "end": v(-482.52, 43.96) * mm});
            skLineSegment(sketch, "E917", {"start": v(-482.52, 43.96) * mm, "end": v(-483.48, 43.56) * mm});
            skLineSegment(sketch, "E918", {"start": v(-483.48, 43.56) * mm, "end": v(-484.44, 43.15) * mm});
            skLineSegment(sketch, "E919", {"start": v(-484.44, 43.15) * mm, "end": v(-485.4, 42.73) * mm});
            skLineSegment(sketch, "E920", {"start": v(-485.4, 42.73) * mm, "end": v(-486.35, 42.31) * mm});
            skLineSegment(sketch, "E921", {"start": v(-486.35, 42.31) * mm, "end": v(-487.3, 41.89) * mm});
            skLineSegment(sketch, "E922", {"start": v(-487.3, 41.89) * mm, "end": v(-488.25, 41.46) * mm});
            skLineSegment(sketch, "E923", {"start": v(-488.25, 41.46) * mm, "end": v(-489.19, 41.02) * mm});
            skLineSegment(sketch, "E924", {"start": v(-489.19, 41.02) * mm, "end": v(-490.12, 40.58) * mm});
            skLineSegment(sketch, "E925", {"start": v(-490.12, 40.58) * mm, "end": v(-491.04, 40.13) * mm});
            skLineSegment(sketch, "E926", {"start": v(-491.04, 40.13) * mm, "end": v(-491.95, 39.67) * mm});
            skLineSegment(sketch, "E927", {"start": v(-491.95, 39.67) * mm, "end": v(-492.85, 39.2) * mm});
            skLineSegment(sketch, "E928", {"start": v(-492.85, 39.2) * mm, "end": v(-493.73, 38.72) * mm});
            skLineSegment(sketch, "E929", {"start": v(-493.73, 38.72) * mm, "end": v(-494.6, 38.23) * mm});
            skLineSegment(sketch, "E930", {"start": v(-494.6, 38.23) * mm, "end": v(-495.47, 37.73) * mm});
            skLineSegment(sketch, "E931", {"start": v(-495.47, 37.73) * mm, "end": v(-496.31, 37.22) * mm});
            skLineSegment(sketch, "E932", {"start": v(-496.31, 37.22) * mm, "end": v(-497.14, 36.7) * mm});
            skLineSegment(sketch, "E933", {"start": v(-497.14, 36.7) * mm, "end": v(-497.94, 36.16) * mm});
            skLineSegment(sketch, "E934", {"start": v(-497.94, 36.16) * mm, "end": v(-498.73, 35.6) * mm});
            skLineSegment(sketch, "E935", {"start": v(-498.73, 35.6) * mm, "end": v(-499.5, 35.04) * mm});
            skLineSegment(sketch, "E936", {"start": v(-265.5, -20.96) * mm, "end": v(-265.36, -21.98) * mm});
            skLineSegment(sketch, "E937", {"start": v(-265.36, -21.98) * mm, "end": v(-265.22, -23) * mm});
            skLineSegment(sketch, "E938", {"start": v(-265.22, -23) * mm, "end": v(-265.06, -24.04) * mm});
            skLineSegment(sketch, "E939", {"start": v(-265.06, -24.04) * mm, "end": v(-264.88, -25.07) * mm});
            skLineSegment(sketch, "E940", {"start": v(-264.88, -25.07) * mm, "end": v(-264.7, -26.1) * mm});
            skLineSegment(sketch, "E941", {"start": v(-264.7, -26.1) * mm, "end": v(-264.48, -27.14) * mm});
            skLineSegment(sketch, "E942", {"start": v(-264.48, -27.14) * mm, "end": v(-264.26, -28.17) * mm});
            skLineSegment(sketch, "E943", {"start": v(-264.26, -28.17) * mm, "end": v(-264, -29.19) * mm});
            skLineSegment(sketch, "E944", {"start": v(-264, -29.19) * mm, "end": v(-263.73, -30.2) * mm});
            skLineSegment(sketch, "E945", {"start": v(-263.73, -30.2) * mm, "end": v(-263.43, -31.21) * mm});
            skLineSegment(sketch, "E946", {"start": v(-263.43, -31.21) * mm, "end": v(-263.1, -32.2) * mm});
            skLineSegment(sketch, "E947", {"start": v(-263.1, -32.2) * mm, "end": v(-262.74, -33.19) * mm});
            skLineSegment(sketch, "E948", {"start": v(-262.74, -33.19) * mm, "end": v(-262.35, -34.16) * mm});
            skLineSegment(sketch, "E949", {"start": v(-262.35, -34.16) * mm, "end": v(-261.93, -35.1) * mm});
            skLineSegment(sketch, "E950", {"start": v(-261.93, -35.1) * mm, "end": v(-261.47, -36.04) * mm});
            skLineSegment(sketch, "E951", {"start": v(-261.47, -36.04) * mm, "end": v(-260.97, -36.96) * mm});
            skLineSegment(sketch, "E952", {"start": v(-260.97, -36.96) * mm, "end": v(-260.5, -37.76) * mm});
            skLineSegment(sketch, "E953", {"start": v(-260.5, -37.76) * mm, "end": v(-260, -38.55) * mm});
            skLineSegment(sketch, "E954", {"start": v(-260, -38.55) * mm, "end": v(-259.48, -39.31) * mm});
            skLineSegment(sketch, "E955", {"start": v(-259.48, -39.31) * mm, "end": v(-258.94, -40.05) * mm});
            skLineSegment(sketch, "E956", {"start": v(-258.94, -40.05) * mm, "end": v(-258.39, -40.77) * mm});
            skLineSegment(sketch, "E957", {"start": v(-258.39, -40.77) * mm, "end": v(-257.82, -41.47) * mm});
            skLineSegment(sketch, "E958", {"start": v(-257.82, -41.47) * mm, "end": v(-257.23, -42.15) * mm});
            skLineSegment(sketch, "E959", {"start": v(-257.23, -42.15) * mm, "end": v(-256.62, -42.81) * mm});
            skLineSegment(sketch, "E960", {"start": v(-256.62, -42.81) * mm, "end": v(-256, -43.45) * mm});
            skLineSegment(sketch, "E961", {"start": v(-256, -43.45) * mm, "end": v(-255.36, -44.07) * mm});
            skLineSegment(sketch, "E962", {"start": v(-255.36, -44.07) * mm, "end": v(-254.7, -44.68) * mm});
            skLineSegment(sketch, "E963", {"start": v(-254.7, -44.68) * mm, "end": v(-254.04, -45.26) * mm});
            skLineSegment(sketch, "E964", {"start": v(-254.04, -45.26) * mm, "end": v(-253.35, -45.82) * mm});
            skLineSegment(sketch, "E965", {"start": v(-253.35, -45.82) * mm, "end": v(-252.65, -46.37) * mm});
            skLineSegment(sketch, "E966", {"start": v(-252.65, -46.37) * mm, "end": v(-251.94, -46.9) * mm});
            skLineSegment(sketch, "E967", {"start": v(-251.94, -46.9) * mm, "end": v(-251.21, -47.4) * mm});
            skLineSegment(sketch, "E968", {"start": v(-251.21, -47.4) * mm, "end": v(-250.47, -47.9) * mm});
            skLineSegment(sketch, "E969", {"start": v(-250.47, -47.9) * mm, "end": v(-249.72, -48.38) * mm});
            skLineSegment(sketch, "E970", {"start": v(-249.72, -48.38) * mm, "end": v(-248.95, -48.83) * mm});
            skLineSegment(sketch, "E971", {"start": v(-248.95, -48.83) * mm, "end": v(-248.17, -49.28) * mm});
            skLineSegment(sketch, "E972", {"start": v(-248.17, -49.28) * mm, "end": v(-247.38, -49.7) * mm});
            skLineSegment(sketch, "E973", {"start": v(-247.38, -49.7) * mm, "end": v(-246.57, -50.11) * mm});
            skLineSegment(sketch, "E974", {"start": v(-246.57, -50.11) * mm, "end": v(-245.76, -50.5) * mm});
            skLineSegment(sketch, "E975", {"start": v(-245.76, -50.5) * mm, "end": v(-244.93, -50.89) * mm});
            skLineSegment(sketch, "E976", {"start": v(-244.93, -50.89) * mm, "end": v(-244.1, -51.25) * mm});
            skLineSegment(sketch, "E977", {"start": v(-244.1, -51.25) * mm, "end": v(-243.25, -51.6) * mm});
            skLineSegment(sketch, "E978", {"start": v(-243.25, -51.6) * mm, "end": v(-242.4, -51.94) * mm});
            skLineSegment(sketch, "E979", {"start": v(-242.4, -51.94) * mm, "end": v(-241.53, -52.26) * mm});
            skLineSegment(sketch, "E980", {"start": v(-241.53, -52.26) * mm, "end": v(-240.66, -52.57) * mm});
            skLineSegment(sketch, "E981", {"start": v(-240.66, -52.57) * mm, "end": v(-239.77, -52.86) * mm});
            skLineSegment(sketch, "E982", {"start": v(-239.77, -52.86) * mm, "end": v(-238.88, -53.14) * mm});
            skLineSegment(sketch, "E983", {"start": v(-238.88, -53.14) * mm, "end": v(-237.98, -53.41) * mm});
            skLineSegment(sketch, "E984", {"start": v(-237.98, -53.41) * mm, "end": v(-237.08, -53.67) * mm});
            skLineSegment(sketch, "E985", {"start": v(-237.08, -53.67) * mm, "end": v(-236.17, -53.91) * mm});
            skLineSegment(sketch, "E986", {"start": v(-236.17, -53.91) * mm, "end": v(-235.25, -54.14) * mm});
            skLineSegment(sketch, "E987", {"start": v(-235.25, -54.14) * mm, "end": v(-234.32, -54.36) * mm});
            skLineSegment(sketch, "E988", {"start": v(-234.32, -54.36) * mm, "end": v(-233.4, -54.57) * mm});
            skLineSegment(sketch, "E989", {"start": v(-233.4, -54.57) * mm, "end": v(-232.46, -54.77) * mm});
            skLineSegment(sketch, "E990", {"start": v(-232.46, -54.77) * mm, "end": v(-231.51, -54.95) * mm});
            skLineSegment(sketch, "E991", {"start": v(-231.51, -54.95) * mm, "end": v(-230.57, -55.13) * mm});
            skLineSegment(sketch, "E992", {"start": v(-230.57, -55.13) * mm, "end": v(-229.62, -55.3) * mm});
            skLineSegment(sketch, "E993", {"start": v(-229.62, -55.3) * mm, "end": v(-228.67, -55.45) * mm});
            skLineSegment(sketch, "E994", {"start": v(-228.67, -55.45) * mm, "end": v(-227.7, -55.6) * mm});
            skLineSegment(sketch, "E995", {"start": v(-227.7, -55.6) * mm, "end": v(-226.75, -55.73) * mm});
            skLineSegment(sketch, "E996", {"start": v(-226.75, -55.73) * mm, "end": v(-225.79, -55.86) * mm});
            skLineSegment(sketch, "E997", {"start": v(-225.79, -55.86) * mm, "end": v(-224.82, -55.98) * mm});
            skLineSegment(sketch, "E998", {"start": v(-224.82, -55.98) * mm, "end": v(-223.86, -56.1) * mm});
            skLineSegment(sketch, "E999", {"start": v(-223.86, -56.1) * mm, "end": v(-222.89, -56.2) * mm});
            skLineSegment(sketch, "E1000", {"start": v(-222.89, -56.2) * mm, "end": v(-221.92, -56.29) * mm});
            skLineSegment(sketch, "E1001", {"start": v(-221.92, -56.29) * mm, "end": v(-220.95, -56.38) * mm});
            skLineSegment(sketch, "E1002", {"start": v(-220.95, -56.38) * mm, "end": v(-219.98, -56.46) * mm});
            skLineSegment(sketch, "E1003", {"start": v(-219.98, -56.46) * mm, "end": v(-219, -56.53) * mm});
            skLineSegment(sketch, "E1004", {"start": v(-219, -56.53) * mm, "end": v(-218.04, -56.6) * mm});
            skLineSegment(sketch, "E1005", {"start": v(-218.04, -56.6) * mm, "end": v(-217.07, -56.65) * mm});
            skLineSegment(sketch, "E1006", {"start": v(-217.07, -56.65) * mm, "end": v(-216.1, -56.7) * mm});
            skLineSegment(sketch, "E1007", {"start": v(-216.1, -56.7) * mm, "end": v(-215.14, -56.76) * mm});
            skLineSegment(sketch, "E1008", {"start": v(-215.14, -56.76) * mm, "end": v(-214.18, -56.8) * mm});
            skLineSegment(sketch, "E1009", {"start": v(-214.18, -56.8) * mm, "end": v(-213.22, -56.84) * mm});
            skLineSegment(sketch, "E1010", {"start": v(-213.22, -56.84) * mm, "end": v(-212.26, -56.87) * mm});
            skLineSegment(sketch, "E1011", {"start": v(-212.26, -56.87) * mm, "end": v(-211.3, -56.9) * mm});
            skLineSegment(sketch, "E1012", {"start": v(-211.3, -56.9) * mm, "end": v(-210.35, -56.92) * mm});
            skLineSegment(sketch, "E1013", {"start": v(-210.35, -56.92) * mm, "end": v(-209.4, -56.94) * mm});
            skLineSegment(sketch, "E1014", {"start": v(-209.4, -56.94) * mm, "end": v(-208.46, -56.96) * mm});
            skLineSegment(sketch, "E1015", {"start": v(-208.46, -56.96) * mm, "end": v(-207.53, -56.97) * mm});
            skLineSegment(sketch, "E1016", {"start": v(-207.53, -56.97) * mm, "end": v(-206.6, -56.98) * mm});
            skLineSegment(sketch, "E1017", {"start": v(-206.6, -56.98) * mm, "end": v(-205.67, -56.99) * mm});
            skLineSegment(sketch, "E1018", {"start": v(-205.67, -56.99) * mm, "end": v(-204.75, -56.99) * mm});
            skLineSegment(sketch, "E1019", {"start": v(-204.75, -56.99) * mm, "end": v(-203.83, -57) * mm});
            skLineSegment(sketch, "E1020", {"start": v(-203.83, -57) * mm, "end": v(-202.92, -57) * mm});
            skLineSegment(sketch, "E1021", {"start": v(-202.92, -57) * mm, "end": v(-202.02, -57) * mm});
            skLineSegment(sketch, "E1022", {"start": v(-202.02, -57) * mm, "end": v(-201.13, -56.99) * mm});
            skLineSegment(sketch, "E1023", {"start": v(-201.13, -56.99) * mm, "end": v(-200.25, -56.98) * mm});
            skLineSegment(sketch, "E1024", {"start": v(-200.25, -56.98) * mm, "end": v(-199.37, -56.98) * mm});
            skLineSegment(sketch, "E1025", {"start": v(-199.37, -56.98) * mm, "end": v(-198.5, -56.98) * mm});
            skLineSegment(sketch, "E1026", {"start": v(-198.5, -56.98) * mm, "end": v(-197.64, -56.97) * mm});
            skLineSegment(sketch, "E1027", {"start": v(-197.64, -56.97) * mm, "end": v(-196.8, -56.97) * mm});
            skLineSegment(sketch, "E1028", {"start": v(-196.8, -56.97) * mm, "end": v(-195.95, -56.96) * mm});
            skLineSegment(sketch, "E1029", {"start": v(-195.95, -56.96) * mm, "end": v(-195.13, -56.96) * mm});
            skLineSegment(sketch, "E1030", {"start": v(-195.13, -56.96) * mm, "end": v(-194.3, -56.96) * mm});
            skLineSegment(sketch, "E1031", {"start": v(-194.3, -56.96) * mm, "end": v(-193.5, -56.96) * mm});
            skLineSegment(sketch, "E1032", {"start": v(-193.5, -56.96) * mm, "end": v(-192.5, -56.96) * mm});
            skLineSegment(sketch, "E1033", {"start": v(-192.5, -56.96) * mm, "end": v(-191.5, -56.96) * mm});
            skLineSegment(sketch, "E1034", {"start": v(-191.5, -56.96) * mm, "end": v(-190.5, -56.97) * mm});
            skLineSegment(sketch, "E1035", {"start": v(-190.5, -56.97) * mm, "end": v(-189.5, -56.98) * mm});
            skLineSegment(sketch, "E1036", {"start": v(-189.5, -56.98) * mm, "end": v(-188.5, -57) * mm});
            skLineSegment(sketch, "E1037", {"start": v(-188.5, -57) * mm, "end": v(-187.5, -57) * mm});
            skLineSegment(sketch, "E1038", {"start": v(-187.5, -57) * mm, "end": v(-186.5, -57.02) * mm});
            skLineSegment(sketch, "E1039", {"start": v(-186.5, -57.02) * mm, "end": v(-185.49, -57.03) * mm});
            skLineSegment(sketch, "E1040", {"start": v(-185.49, -57.03) * mm, "end": v(-184.49, -57.04) * mm});
            skLineSegment(sketch, "E1041", {"start": v(-184.49, -57.04) * mm, "end": v(-183.48, -57.05) * mm});
            skLineSegment(sketch, "E1042", {"start": v(-183.48, -57.05) * mm, "end": v(-182.48, -57.05) * mm});
            skLineSegment(sketch, "E1043", {"start": v(-182.48, -57.05) * mm, "end": v(-181.48, -57.05) * mm});
            skLineSegment(sketch, "E1044", {"start": v(-181.48, -57.05) * mm, "end": v(-180.47, -57.05) * mm});
            skLineSegment(sketch, "E1045", {"start": v(-180.47, -57.05) * mm, "end": v(-179.47, -57.04) * mm});
            skLineSegment(sketch, "E1046", {"start": v(-179.47, -57.04) * mm, "end": v(-178.47, -57.02) * mm});
            skLineSegment(sketch, "E1047", {"start": v(-178.47, -57.02) * mm, "end": v(-177.47, -57) * mm});
            skLineSegment(sketch, "E1048", {"start": v(-177.47, -57) * mm, "end": v(-176.46, -56.97) * mm});
            skLineSegment(sketch, "E1049", {"start": v(-176.46, -56.97) * mm, "end": v(-175.46, -56.93) * mm});
            skLineSegment(sketch, "E1050", {"start": v(-175.46, -56.93) * mm, "end": v(-174.46, -56.88) * mm});
            skLineSegment(sketch, "E1051", {"start": v(-174.46, -56.88) * mm, "end": v(-173.47, -56.83) * mm});
            skLineSegment(sketch, "E1052", {"start": v(-173.47, -56.83) * mm, "end": v(-172.47, -56.76) * mm});
            skLineSegment(sketch, "E1053", {"start": v(-172.47, -56.76) * mm, "end": v(-171.47, -56.68) * mm});
            skLineSegment(sketch, "E1054", {"start": v(-171.47, -56.68) * mm, "end": v(-170.48, -56.59) * mm});
            skLineSegment(sketch, "E1055", {"start": v(-170.48, -56.59) * mm, "end": v(-169.48, -56.48) * mm});
            skLineSegment(sketch, "E1056", {"start": v(-169.48, -56.48) * mm, "end": v(-168.5, -56.36) * mm});
            skLineSegment(sketch, "E1057", {"start": v(-168.5, -56.36) * mm, "end": v(-167.5, -56.23) * mm});
            skLineSegment(sketch, "E1058", {"start": v(-167.5, -56.23) * mm, "end": v(-166.64, -56.1) * mm});
            skLineSegment(sketch, "E1059", {"start": v(-166.64, -56.1) * mm, "end": v(-165.77, -55.97) * mm});
            skLineSegment(sketch, "E1060", {"start": v(-165.77, -55.97) * mm, "end": v(-164.9, -55.83) * mm});
            skLineSegment(sketch, "E1061", {"start": v(-164.9, -55.83) * mm, "end": v(-164.01, -55.7) * mm});
            skLineSegment(sketch, "E1062", {"start": v(-164.01, -55.7) * mm, "end": v(-163.12, -55.54) * mm});
            skLineSegment(sketch, "E1063", {"start": v(-163.12, -55.54) * mm, "end": v(-162.22, -55.38) * mm});
            skLineSegment(sketch, "E1064", {"start": v(-162.22, -55.38) * mm, "end": v(-161.32, -55.21) * mm});
            skLineSegment(sketch, "E1065", {"start": v(-161.32, -55.21) * mm, "end": v(-160.42, -55.04) * mm});
            skLineSegment(sketch, "E1066", {"start": v(-160.42, -55.04) * mm, "end": v(-159.5, -54.85) * mm});
            skLineSegment(sketch, "E1067", {"start": v(-159.5, -54.85) * mm, "end": v(-158.6, -54.66) * mm});
            skLineSegment(sketch, "E1068", {"start": v(-158.6, -54.66) * mm, "end": v(-157.68, -54.46) * mm});
            skLineSegment(sketch, "E1069", {"start": v(-157.68, -54.46) * mm, "end": v(-156.77, -54.24) * mm});
            skLineSegment(sketch, "E1070", {"start": v(-156.77, -54.24) * mm, "end": v(-155.86, -54.02) * mm});
            skLineSegment(sketch, "E1071", {"start": v(-155.86, -54.02) * mm, "end": v(-154.94, -53.79) * mm});
            skLineSegment(sketch, "E1072", {"start": v(-154.94, -53.79) * mm, "end": v(-154.03, -53.54) * mm});
            skLineSegment(sketch, "E1073", {"start": v(-154.03, -53.54) * mm, "end": v(-153.12, -53.28) * mm});
            skLineSegment(sketch, "E1074", {"start": v(-153.12, -53.28) * mm, "end": v(-152.22, -53.01) * mm});
            skLineSegment(sketch, "E1075", {"start": v(-152.22, -53.01) * mm, "end": v(-151.32, -52.73) * mm});
            skLineSegment(sketch, "E1076", {"start": v(-151.32, -52.73) * mm, "end": v(-150.42, -52.44) * mm});
            skLineSegment(sketch, "E1077", {"start": v(-150.42, -52.44) * mm, "end": v(-149.53, -52.13) * mm});
            skLineSegment(sketch, "E1078", {"start": v(-149.53, -52.13) * mm, "end": v(-148.65, -51.8) * mm});
            skLineSegment(sketch, "E1079", {"start": v(-148.65, -51.8) * mm, "end": v(-147.77, -51.47) * mm});
            skLineSegment(sketch, "E1080", {"start": v(-147.77, -51.47) * mm, "end": v(-146.9, -51.12) * mm});
            skLineSegment(sketch, "E1081", {"start": v(-146.9, -51.12) * mm, "end": v(-146.05, -50.76) * mm});
            skLineSegment(sketch, "E1082", {"start": v(-146.05, -50.76) * mm, "end": v(-145.2, -50.38) * mm});
            skLineSegment(sketch, "E1083", {"start": v(-145.2, -50.38) * mm, "end": v(-144.37, -49.98) * mm});
            skLineSegment(sketch, "E1084", {"start": v(-144.37, -49.98) * mm, "end": v(-143.54, -49.57) * mm});
            skLineSegment(sketch, "E1085", {"start": v(-143.54, -49.57) * mm, "end": v(-142.73, -49.14) * mm});
            skLineSegment(sketch, "E1086", {"start": v(-142.73, -49.14) * mm, "end": v(-141.93, -48.7) * mm});
            skLineSegment(sketch, "E1087", {"start": v(-141.93, -48.7) * mm, "end": v(-141.15, -48.24) * mm});
            skLineSegment(sketch, "E1088", {"start": v(-141.15, -48.24) * mm, "end": v(-140.38, -47.76) * mm});
            skLineSegment(sketch, "E1089", {"start": v(-140.38, -47.76) * mm, "end": v(-139.63, -47.26) * mm});
            skLineSegment(sketch, "E1090", {"start": v(-139.63, -47.26) * mm, "end": v(-138.89, -46.74) * mm});
            skLineSegment(sketch, "E1091", {"start": v(-138.89, -46.74) * mm, "end": v(-138.17, -46.2) * mm});
            skLineSegment(sketch, "E1092", {"start": v(-138.17, -46.2) * mm, "end": v(-137.47, -45.65) * mm});
            skLineSegment(sketch, "E1093", {"start": v(-137.47, -45.65) * mm, "end": v(-136.8, -45.08) * mm});
            skLineSegment(sketch, "E1094", {"start": v(-136.8, -45.08) * mm, "end": v(-136.13, -44.49) * mm});
            skLineSegment(sketch, "E1095", {"start": v(-136.13, -44.49) * mm, "end": v(-135.5, -43.87) * mm});
            skLineSegment(sketch, "E1096", {"start": v(-135.5, -43.87) * mm, "end": v(-134.88, -43.24) * mm});
            skLineSegment(sketch, "E1097", {"start": v(-134.88, -43.24) * mm, "end": v(-134.28, -42.58) * mm});
            skLineSegment(sketch, "E1098", {"start": v(-134.28, -42.58) * mm, "end": v(-133.71, -41.9) * mm});
            skLineSegment(sketch, "E1099", {"start": v(-133.71, -41.9) * mm, "end": v(-133.17, -41.2) * mm});
            skLineSegment(sketch, "E1100", {"start": v(-133.17, -41.2) * mm, "end": v(-132.64, -40.48) * mm});
            skLineSegment(sketch, "E1101", {"start": v(-132.64, -40.48) * mm, "end": v(-132.15, -39.74) * mm});
            skLineSegment(sketch, "E1102", {"start": v(-132.15, -39.74) * mm, "end": v(-131.68, -38.97) * mm});
            skLineSegment(sketch, "E1103", {"start": v(-131.68, -38.97) * mm, "end": v(-131.24, -38.18) * mm});
            skLineSegment(sketch, "E1104", {"start": v(-131.24, -38.18) * mm, "end": v(-130.83, -37.37) * mm});
            skLineSegment(sketch, "E1105", {"start": v(-130.83, -37.37) * mm, "end": v(-130.45, -36.53) * mm});
            skLineSegment(sketch, "E1106", {"start": v(-130.45, -36.53) * mm, "end": v(-130.1, -35.66) * mm});
            skLineSegment(sketch, "E1107", {"start": v(-130.1, -35.66) * mm, "end": v(-129.78, -34.77) * mm});
            skLineSegment(sketch, "E1108", {"start": v(-129.78, -34.77) * mm, "end": v(-129.49, -33.86) * mm});
            skLineSegment(sketch, "E1109", {"start": v(-129.49, -33.86) * mm, "end": v(-129.23, -32.92) * mm});
            skLineSegment(sketch, "E1110", {"start": v(-129.23, -32.92) * mm, "end": v(-129.01, -31.95) * mm});
            skLineSegment(sketch, "E1111", {"start": v(-129.01, -31.95) * mm, "end": v(-128.83, -30.96) * mm});
            skLineSegment(sketch, "E1112", {"start": v(-128.83, -30.96) * mm, "end": v(-128.68, -30) * mm});
            skLineSegment(sketch, "E1113", {"start": v(-128.68, -30) * mm, "end": v(-128.56, -29) * mm});
            skLineSegment(sketch, "E1114", {"start": v(-128.56, -29) * mm, "end": v(-128.47, -28.01) * mm});
            skLineSegment(sketch, "E1115", {"start": v(-128.47, -28.01) * mm, "end": v(-128.4, -27) * mm});
            skLineSegment(sketch, "E1116", {"start": v(-128.4, -27) * mm, "end": v(-128.37, -25.99) * mm});
            skLineSegment(sketch, "E1117", {"start": v(-128.37, -25.99) * mm, "end": v(-128.35, -24.97) * mm});
            skLineSegment(sketch, "E1118", {"start": v(-128.35, -24.97) * mm, "end": v(-128.35, -23.95) * mm});
            skLineSegment(sketch, "E1119", {"start": v(-128.35, -23.95) * mm, "end": v(-128.37, -22.93) * mm});
            skLineSegment(sketch, "E1120", {"start": v(-128.37, -22.93) * mm, "end": v(-128.4, -21.92) * mm});
            skLineSegment(sketch, "E1121", {"start": v(-128.4, -21.92) * mm, "end": v(-128.46, -20.92) * mm});
            skLineSegment(sketch, "E1122", {"start": v(-128.46, -20.92) * mm, "end": v(-128.52, -19.93) * mm});
            skLineSegment(sketch, "E1123", {"start": v(-128.52, -19.93) * mm, "end": v(-128.6, -18.96) * mm});
            skLineSegment(sketch, "E1124", {"start": v(-128.6, -18.96) * mm, "end": v(-128.7, -17.96) * mm});
            skLineSegment(sketch, "E1125", {"start": v(-128.7, -17.96) * mm, "end": v(-128.85, -16.99) * mm});
            skLineSegment(sketch, "E1126", {"start": v(-128.85, -16.99) * mm, "end": v(-129.04, -16.03) * mm});
            skLineSegment(sketch, "E1127", {"start": v(-129.04, -16.03) * mm, "end": v(-129.27, -15.08) * mm});
            skLineSegment(sketch, "E1128", {"start": v(-129.27, -15.08) * mm, "end": v(-129.54, -14.15) * mm});
            skLineSegment(sketch, "E1129", {"start": v(-129.54, -14.15) * mm, "end": v(-129.86, -13.24) * mm});
            skLineSegment(sketch, "E1130", {"start": v(-129.86, -13.24) * mm, "end": v(-130.2, -12.34) * mm});
            skLineSegment(sketch, "E1131", {"start": v(-130.2, -12.34) * mm, "end": v(-130.6, -11.46) * mm});
            skLineSegment(sketch, "E1132", {"start": v(-130.6, -11.46) * mm, "end": v(-131.01, -10.6) * mm});
            skLineSegment(sketch, "E1133", {"start": v(-131.01, -10.6) * mm, "end": v(-131.46, -9.75) * mm});
            skLineSegment(sketch, "E1134", {"start": v(-131.46, -9.75) * mm, "end": v(-131.95, -8.92) * mm});
            skLineSegment(sketch, "E1135", {"start": v(-131.95, -8.92) * mm, "end": v(-132.47, -8.1) * mm});
            skLineSegment(sketch, "E1136", {"start": v(-132.47, -8.1) * mm, "end": v(-133.01, -7.31) * mm});
            skLineSegment(sketch, "E1137", {"start": v(-133.01, -7.31) * mm, "end": v(-133.59, -6.54) * mm});
            skLineSegment(sketch, "E1138", {"start": v(-133.59, -6.54) * mm, "end": v(-134.19, -5.78) * mm});
            skLineSegment(sketch, "E1139", {"start": v(-134.19, -5.78) * mm, "end": v(-134.81, -5.04) * mm});
            skLineSegment(sketch, "E1140", {"start": v(-134.81, -5.04) * mm, "end": v(-135.46, -4.32) * mm});
            skLineSegment(sketch, "E1141", {"start": v(-135.46, -4.32) * mm, "end": v(-136.14, -3.62) * mm});
            skLineSegment(sketch, "E1142", {"start": v(-136.14, -3.62) * mm, "end": v(-136.83, -2.94) * mm});
            skLineSegment(sketch, "E1143", {"start": v(-136.83, -2.94) * mm, "end": v(-137.55, -2.27) * mm});
            skLineSegment(sketch, "E1144", {"start": v(-137.55, -2.27) * mm, "end": v(-138.28, -1.63) * mm});
            skLineSegment(sketch, "E1145", {"start": v(-138.28, -1.63) * mm, "end": v(-139.03, -1) * mm});
            skLineSegment(sketch, "E1146", {"start": v(-139.03, -1) * mm, "end": v(-139.8, -0.4) * mm});
            skLineSegment(sketch, "E1147", {"start": v(-139.8, -0.4) * mm, "end": v(-140.58, 0.19) * mm});
            skLineSegment(sketch, "E1148", {"start": v(-140.58, 0.19) * mm, "end": v(-141.37, 0.75) * mm});
            skLineSegment(sketch, "E1149", {"start": v(-141.37, 0.75) * mm, "end": v(-142.18, 1.3) * mm});
            skLineSegment(sketch, "E1150", {"start": v(-142.18, 1.3) * mm, "end": v(-143, 1.82) * mm});
            skLineSegment(sketch, "E1151", {"start": v(-143, 1.82) * mm, "end": v(-143.82, 2.32) * mm});
            skLineSegment(sketch, "E1152", {"start": v(-143.82, 2.32) * mm, "end": v(-144.66, 2.8) * mm});
            skLineSegment(sketch, "E1153", {"start": v(-144.66, 2.8) * mm, "end": v(-145.5, 3.26) * mm});
            skLineSegment(sketch, "E1154", {"start": v(-145.5, 3.26) * mm, "end": v(-146.4, 3.73) * mm});
            skLineSegment(sketch, "E1155", {"start": v(-146.4, 3.73) * mm, "end": v(-147.3, 4.18) * mm});
            skLineSegment(sketch, "E1156", {"start": v(-147.3, 4.18) * mm, "end": v(-148.2, 4.61) * mm});
            skLineSegment(sketch, "E1157", {"start": v(-148.2, 4.61) * mm, "end": v(-149.1, 5.03) * mm});
            skLineSegment(sketch, "E1158", {"start": v(-149.1, 5.03) * mm, "end": v(-150.01, 5.43) * mm});
            skLineSegment(sketch, "E1159", {"start": v(-150.01, 5.43) * mm, "end": v(-150.93, 5.82) * mm});
            skLineSegment(sketch, "E1160", {"start": v(-150.93, 5.82) * mm, "end": v(-151.85, 6.2) * mm});
            skLineSegment(sketch, "E1161", {"start": v(-151.85, 6.2) * mm, "end": v(-152.77, 6.55) * mm});
            skLineSegment(sketch, "E1162", {"start": v(-152.77, 6.55) * mm, "end": v(-153.7, 6.9) * mm});
            skLineSegment(sketch, "E1163", {"start": v(-153.7, 6.9) * mm, "end": v(-154.63, 7.23) * mm});
            skLineSegment(sketch, "E1164", {"start": v(-154.63, 7.23) * mm, "end": v(-155.56, 7.55) * mm});
            skLineSegment(sketch, "E1165", {"start": v(-155.56, 7.55) * mm, "end": v(-156.5, 7.86) * mm});
            skLineSegment(sketch, "E1166", {"start": v(-156.5, 7.86) * mm, "end": v(-157.44, 8.16) * mm});
            skLineSegment(sketch, "E1167", {"start": v(-157.44, 8.16) * mm, "end": v(-158.38, 8.45) * mm});
            skLineSegment(sketch, "E1168", {"start": v(-158.38, 8.45) * mm, "end": v(-159.33, 8.72) * mm});
            skLineSegment(sketch, "E1169", {"start": v(-159.33, 8.72) * mm, "end": v(-160.28, 8.98) * mm});
            skLineSegment(sketch, "E1170", {"start": v(-160.28, 8.98) * mm, "end": v(-161.23, 9.24) * mm});
            skLineSegment(sketch, "E1171", {"start": v(-161.23, 9.24) * mm, "end": v(-162.18, 9.48) * mm});
            skLineSegment(sketch, "E1172", {"start": v(-162.18, 9.48) * mm, "end": v(-163.14, 9.72) * mm});
            skLineSegment(sketch, "E1173", {"start": v(-163.14, 9.72) * mm, "end": v(-164.1, 9.94) * mm});
            skLineSegment(sketch, "E1174", {"start": v(-164.1, 9.94) * mm, "end": v(-165.06, 10.16) * mm});
            skLineSegment(sketch, "E1175", {"start": v(-165.06, 10.16) * mm, "end": v(-166.03, 10.37) * mm});
            skLineSegment(sketch, "E1176", {"start": v(-166.03, 10.37) * mm, "end": v(-167, 10.57) * mm});
            skLineSegment(sketch, "E1177", {"start": v(-167, 10.57) * mm, "end": v(-167.96, 10.77) * mm});
            skLineSegment(sketch, "E1178", {"start": v(-167.96, 10.77) * mm, "end": v(-168.93, 10.95) * mm});
            skLineSegment(sketch, "E1179", {"start": v(-168.93, 10.95) * mm, "end": v(-169.9, 11.13) * mm});
            skLineSegment(sketch, "E1180", {"start": v(-169.9, 11.13) * mm, "end": v(-170.88, 11.3) * mm});
            skLineSegment(sketch, "E1181", {"start": v(-170.88, 11.3) * mm, "end": v(-171.85, 11.48) * mm});
            skLineSegment(sketch, "E1182", {"start": v(-171.85, 11.48) * mm, "end": v(-172.83, 11.64) * mm});
            skLineSegment(sketch, "E1183", {"start": v(-172.83, 11.64) * mm, "end": v(-173.8, 11.8) * mm});
            skLineSegment(sketch, "E1184", {"start": v(-173.8, 11.8) * mm, "end": v(-174.78, 11.96) * mm});
            skLineSegment(sketch, "E1185", {"start": v(-174.78, 11.96) * mm, "end": v(-175.76, 12.1) * mm});
            skLineSegment(sketch, "E1186", {"start": v(-175.76, 12.1) * mm, "end": v(-176.74, 12.25) * mm});
            skLineSegment(sketch, "E1187", {"start": v(-176.74, 12.25) * mm, "end": v(-177.73, 12.4) * mm});
            skLineSegment(sketch, "E1188", {"start": v(-177.73, 12.4) * mm, "end": v(-178.7, 12.54) * mm});
            skLineSegment(sketch, "E1189", {"start": v(-178.7, 12.54) * mm, "end": v(-179.7, 12.68) * mm});
            skLineSegment(sketch, "E1190", {"start": v(-179.7, 12.68) * mm, "end": v(-180.68, 12.82) * mm});
            skLineSegment(sketch, "E1191", {"start": v(-180.68, 12.82) * mm, "end": v(-181.66, 12.95) * mm});
            skLineSegment(sketch, "E1192", {"start": v(-181.66, 12.95) * mm, "end": v(-182.64, 13.09) * mm});
            skLineSegment(sketch, "E1193", {"start": v(-182.64, 13.09) * mm, "end": v(-183.63, 13.22) * mm});
            skLineSegment(sketch, "E1194", {"start": v(-183.63, 13.22) * mm, "end": v(-184.61, 13.35) * mm});
            skLineSegment(sketch, "E1195", {"start": v(-184.61, 13.35) * mm, "end": v(-185.6, 13.49) * mm});
            skLineSegment(sketch, "E1196", {"start": v(-185.6, 13.49) * mm, "end": v(-186.58, 13.62) * mm});
            skLineSegment(sketch, "E1197", {"start": v(-186.58, 13.62) * mm, "end": v(-187.57, 13.76) * mm});
            skLineSegment(sketch, "E1198", {"start": v(-187.57, 13.76) * mm, "end": v(-188.55, 13.9) * mm});
            skLineSegment(sketch, "E1199", {"start": v(-188.55, 13.9) * mm, "end": v(-189.53, 14.03) * mm});
            skLineSegment(sketch, "E1200", {"start": v(-189.53, 14.03) * mm, "end": v(-190.52, 14.17) * mm});
            skLineSegment(sketch, "E1201", {"start": v(-190.52, 14.17) * mm, "end": v(-191.5, 14.32) * mm});
            skLineSegment(sketch, "E1202", {"start": v(-191.5, 14.32) * mm, "end": v(-192.46, 14.45) * mm});
            skLineSegment(sketch, "E1203", {"start": v(-192.46, 14.45) * mm, "end": v(-193.43, 14.58) * mm});
            skLineSegment(sketch, "E1204", {"start": v(-193.43, 14.58) * mm, "end": v(-194.43, 14.7) * mm});
            skLineSegment(sketch, "E1205", {"start": v(-194.43, 14.7) * mm, "end": v(-195.44, 14.82) * mm});
            skLineSegment(sketch, "E1206", {"start": v(-195.44, 14.82) * mm, "end": v(-196.46, 14.94) * mm});
            skLineSegment(sketch, "E1207", {"start": v(-196.46, 14.94) * mm, "end": v(-197.5, 15.07) * mm});
            skLineSegment(sketch, "E1208", {"start": v(-197.5, 15.07) * mm, "end": v(-198.54, 15.2) * mm});
            skLineSegment(sketch, "E1209", {"start": v(-198.54, 15.2) * mm, "end": v(-199.58, 15.33) * mm});
            skLineSegment(sketch, "E1210", {"start": v(-199.58, 15.33) * mm, "end": v(-200.63, 15.47) * mm});
            skLineSegment(sketch, "E1211", {"start": v(-200.63, 15.47) * mm, "end": v(-201.68, 15.62) * mm});
            skLineSegment(sketch, "E1212", {"start": v(-201.68, 15.62) * mm, "end": v(-202.73, 15.79) * mm});
            skLineSegment(sketch, "E1213", {"start": v(-202.73, 15.79) * mm, "end": v(-203.77, 15.97) * mm});
            skLineSegment(sketch, "E1214", {"start": v(-203.77, 15.97) * mm, "end": v(-204.8, 16.16) * mm});
            skLineSegment(sketch, "E1215", {"start": v(-204.8, 16.16) * mm, "end": v(-205.83, 16.38) * mm});
            skLineSegment(sketch, "E1216", {"start": v(-205.83, 16.38) * mm, "end": v(-206.84, 16.62) * mm});
            skLineSegment(sketch, "E1217", {"start": v(-206.84, 16.62) * mm, "end": v(-207.83, 16.88) * mm});
            skLineSegment(sketch, "E1218", {"start": v(-207.83, 16.88) * mm, "end": v(-208.81, 17.17) * mm});
            skLineSegment(sketch, "E1219", {"start": v(-208.81, 17.17) * mm, "end": v(-209.77, 17.48) * mm});
            skLineSegment(sketch, "E1220", {"start": v(-209.77, 17.48) * mm, "end": v(-210.7, 17.83) * mm});
            skLineSegment(sketch, "E1221", {"start": v(-210.7, 17.83) * mm, "end": v(-211.6, 18.2) * mm});
            skLineSegment(sketch, "E1222", {"start": v(-211.6, 18.2) * mm, "end": v(-212.48, 18.62) * mm});
            skLineSegment(sketch, "E1223", {"start": v(-212.48, 18.62) * mm, "end": v(-213.23, 19.02) * mm});
            skLineSegment(sketch, "E1224", {"start": v(-213.23, 19.02) * mm, "end": v(-213.97, 19.5) * mm});
            skLineSegment(sketch, "E1225", {"start": v(-213.97, 19.5) * mm, "end": v(-214.69, 20.03) * mm});
            skLineSegment(sketch, "E1226", {"start": v(-214.69, 20.03) * mm, "end": v(-215.36, 20.62) * mm});
            skLineSegment(sketch, "E1227", {"start": v(-215.36, 20.62) * mm, "end": v(-215.96, 21.26) * mm});
            skLineSegment(sketch, "E1228", {"start": v(-215.96, 21.26) * mm, "end": v(-216.48, 21.96) * mm});
            skLineSegment(sketch, "E1229", {"start": v(-216.48, 21.96) * mm, "end": v(-216.9, 22.7) * mm});
            skLineSegment(sketch, "E1230", {"start": v(-216.9, 22.7) * mm, "end": v(-217.18, 23.46) * mm});
            skLineSegment(sketch, "E1231", {"start": v(-217.18, 23.46) * mm, "end": v(-217.32, 24.27) * mm});
            skLineSegment(sketch, "E1232", {"start": v(-217.32, 24.27) * mm, "end": v(-217.3, 25.1) * mm});
            skLineSegment(sketch, "E1233", {"start": v(-217.3, 25.1) * mm, "end": v(-217.08, 25.95) * mm});
            skLineSegment(sketch, "E1234", {"start": v(-217.08, 25.95) * mm, "end": v(-216.65, 26.82) * mm});
            skLineSegment(sketch, "E1235", {"start": v(-216.65, 26.82) * mm, "end": v(-216.17, 27.49) * mm});
            skLineSegment(sketch, "E1236", {"start": v(-216.17, 27.49) * mm, "end": v(-215.6, 28.1) * mm});
            skLineSegment(sketch, "E1237", {"start": v(-215.6, 28.1) * mm, "end": v(-214.97, 28.64) * mm});
            skLineSegment(sketch, "E1238", {"start": v(-214.97, 28.64) * mm, "end": v(-214.26, 29.13) * mm});
            skLineSegment(sketch, "E1239", {"start": v(-214.26, 29.13) * mm, "end": v(-213.48, 29.56) * mm});
            skLineSegment(sketch, "E1240", {"start": v(-213.48, 29.56) * mm, "end": v(-212.65, 29.94) * mm});
            skLineSegment(sketch, "E1241", {"start": v(-212.65, 29.94) * mm, "end": v(-211.77, 30.27) * mm});
            skLineSegment(sketch, "E1242", {"start": v(-211.77, 30.27) * mm, "end": v(-210.84, 30.55) * mm});
            skLineSegment(sketch, "E1243", {"start": v(-210.84, 30.55) * mm, "end": v(-209.88, 30.78) * mm});
            skLineSegment(sketch, "E1244", {"start": v(-209.88, 30.78) * mm, "end": v(-208.89, 30.97) * mm});
            skLineSegment(sketch, "E1245", {"start": v(-208.89, 30.97) * mm, "end": v(-207.87, 31.12) * mm});
            skLineSegment(sketch, "E1246", {"start": v(-207.87, 31.12) * mm, "end": v(-206.84, 31.23) * mm});
            skLineSegment(sketch, "E1247", {"start": v(-206.84, 31.23) * mm, "end": v(-205.8, 31.3) * mm});
            skLineSegment(sketch, "E1248", {"start": v(-205.8, 31.3) * mm, "end": v(-204.74, 31.35) * mm});
            skLineSegment(sketch, "E1249", {"start": v(-204.74, 31.35) * mm, "end": v(-203.7, 31.36) * mm});
            skLineSegment(sketch, "E1250", {"start": v(-203.7, 31.36) * mm, "end": v(-202.66, 31.34) * mm});
            skLineSegment(sketch, "E1251", {"start": v(-202.66, 31.34) * mm, "end": v(-201.64, 31.3) * mm});
            skLineSegment(sketch, "E1252", {"start": v(-201.64, 31.3) * mm, "end": v(-200.64, 31.24) * mm});
            skLineSegment(sketch, "E1253", {"start": v(-200.64, 31.24) * mm, "end": v(-199.67, 31.15) * mm});
            skLineSegment(sketch, "E1254", {"start": v(-199.67, 31.15) * mm, "end": v(-198.74, 31.05) * mm});
            skLineSegment(sketch, "E1255", {"start": v(-198.74, 31.05) * mm, "end": v(-197.85, 30.94) * mm});
            skLineSegment(sketch, "E1256", {"start": v(-197.85, 30.94) * mm, "end": v(-197, 30.8) * mm});
            skLineSegment(sketch, "E1257", {"start": v(-197, 30.8) * mm, "end": v(-196.22, 30.67) * mm});
            skLineSegment(sketch, "E1258", {"start": v(-196.22, 30.67) * mm, "end": v(-195.5, 30.53) * mm});
            skLineSegment(sketch, "E1259", {"start": v(-195.5, 30.53) * mm, "end": v(-194.5, 30.3) * mm});
            skLineSegment(sketch, "E1260", {"start": v(-194.5, 30.3) * mm, "end": v(-193.53, 30.03) * mm});
            skLineSegment(sketch, "E1261", {"start": v(-193.53, 30.03) * mm, "end": v(-192.56, 29.72) * mm});
            skLineSegment(sketch, "E1262", {"start": v(-192.56, 29.72) * mm, "end": v(-191.61, 29.38) * mm});
            skLineSegment(sketch, "E1263", {"start": v(-191.61, 29.38) * mm, "end": v(-190.68, 29) * mm});
            skLineSegment(sketch, "E1264", {"start": v(-190.68, 29) * mm, "end": v(-189.77, 28.58) * mm});
            skLineSegment(sketch, "E1265", {"start": v(-189.77, 28.58) * mm, "end": v(-188.87, 28.11) * mm});
            skLineSegment(sketch, "E1266", {"start": v(-188.87, 28.11) * mm, "end": v(-188, 27.6) * mm});
            skLineSegment(sketch, "E1267", {"start": v(-188, 27.6) * mm, "end": v(-187.16, 27.06) * mm});
            skLineSegment(sketch, "E1268", {"start": v(-187.16, 27.06) * mm, "end": v(-186.33, 26.46) * mm});
            skLineSegment(sketch, "E1269", {"start": v(-186.33, 26.46) * mm, "end": v(-185.54, 25.82) * mm});
            skLineSegment(sketch, "E1270", {"start": v(-185.54, 25.82) * mm, "end": v(-184.79, 25.15) * mm});
            skLineSegment(sketch, "E1271", {"start": v(-184.79, 25.15) * mm, "end": v(-184.06, 24.44) * mm});
            skLineSegment(sketch, "E1272", {"start": v(-184.06, 24.44) * mm, "end": v(-183.35, 23.72) * mm});
            skLineSegment(sketch, "E1273", {"start": v(-183.35, 23.72) * mm, "end": v(-182.62, 23.01) * mm});
            skLineSegment(sketch, "E1274", {"start": v(-182.62, 23.01) * mm, "end": v(-181.88, 22.33) * mm});
            skLineSegment(sketch, "E1275", {"start": v(-181.88, 22.33) * mm, "end": v(-181.1, 21.7) * mm});
            skLineSegment(sketch, "E1276", {"start": v(-181.1, 21.7) * mm, "end": v(-180.28, 21.16) * mm});
            skLineSegment(sketch, "E1277", {"start": v(-180.28, 21.16) * mm, "end": v(-179.38, 20.7) * mm});
            skLineSegment(sketch, "E1278", {"start": v(-179.38, 20.7) * mm, "end": v(-178.41, 20.36) * mm});
            skLineSegment(sketch, "E1279", {"start": v(-178.41, 20.36) * mm, "end": v(-177.5, 20.15) * mm});
            skLineSegment(sketch, "E1280", {"start": v(-177.5, 20.15) * mm, "end": v(-176.54, 19.98) * mm});
            skLineSegment(sketch, "E1281", {"start": v(-176.54, 19.98) * mm, "end": v(-175.57, 19.86) * mm});
            skLineSegment(sketch, "E1282", {"start": v(-175.57, 19.86) * mm, "end": v(-174.58, 19.78) * mm});
            skLineSegment(sketch, "E1283", {"start": v(-174.58, 19.78) * mm, "end": v(-173.57, 19.74) * mm});
            skLineSegment(sketch, "E1284", {"start": v(-173.57, 19.74) * mm, "end": v(-172.55, 19.72) * mm});
            skLineSegment(sketch, "E1285", {"start": v(-172.55, 19.72) * mm, "end": v(-171.52, 19.73) * mm});
            skLineSegment(sketch, "E1286", {"start": v(-171.52, 19.73) * mm, "end": v(-170.5, 19.76) * mm});
            skLineSegment(sketch, "E1287", {"start": v(-170.5, 19.76) * mm, "end": v(-169.46, 19.8) * mm});
            skLineSegment(sketch, "E1288", {"start": v(-169.46, 19.8) * mm, "end": v(-168.43, 19.86) * mm});
            skLineSegment(sketch, "E1289", {"start": v(-168.43, 19.86) * mm, "end": v(-167.41, 19.9) * mm});
            skLineSegment(sketch, "E1290", {"start": v(-167.41, 19.9) * mm, "end": v(-166.4, 19.96) * mm});
            skLineSegment(sketch, "E1291", {"start": v(-166.4, 19.96) * mm, "end": v(-165.41, 20) * mm});
            skLineSegment(sketch, "E1292", {"start": v(-165.41, 20) * mm, "end": v(-164.44, 20.03) * mm});
            skLineSegment(sketch, "E1293", {"start": v(-164.44, 20.03) * mm, "end": v(-163.5, 20.04) * mm});
            skLineSegment(sketch, "E1294", {"start": v(-163.5, 20.04) * mm, "end": v(-132.5, 20.04) * mm});
            skLineSegment(sketch, "E1295", {"start": v(-132.5, 20.04) * mm, "end": v(-132.54, 21.08) * mm});
            skLineSegment(sketch, "E1296", {"start": v(-132.54, 21.08) * mm, "end": v(-132.61, 22.1) * mm});
            skLineSegment(sketch, "E1297", {"start": v(-132.61, 22.1) * mm, "end": v(-132.72, 23.1) * mm});
            skLineSegment(sketch, "E1298", {"start": v(-132.72, 23.1) * mm, "end": v(-132.85, 24.09) * mm});
            skLineSegment(sketch, "E1299", {"start": v(-132.85, 24.09) * mm, "end": v(-133.02, 25.05) * mm});
            skLineSegment(sketch, "E1300", {"start": v(-133.02, 25.05) * mm, "end": v(-133.22, 26) * mm});
            skLineSegment(sketch, "E1301", {"start": v(-133.22, 26) * mm, "end": v(-133.45, 26.92) * mm});
            skLineSegment(sketch, "E1302", {"start": v(-133.45, 26.92) * mm, "end": v(-133.71, 27.82) * mm});
            skLineSegment(sketch, "E1303", {"start": v(-133.71, 27.82) * mm, "end": v(-134, 28.7) * mm});
            skLineSegment(sketch, "E1304", {"start": v(-134, 28.7) * mm, "end": v(-134.32, 29.58) * mm});
            skLineSegment(sketch, "E1305", {"start": v(-134.32, 29.58) * mm, "end": v(-134.66, 30.43) * mm});
            skLineSegment(sketch, "E1306", {"start": v(-134.66, 30.43) * mm, "end": v(-135.03, 31.26) * mm});
            skLineSegment(sketch, "E1307", {"start": v(-135.03, 31.26) * mm, "end": v(-135.43, 32.08) * mm});
            skLineSegment(sketch, "E1308", {"start": v(-135.43, 32.08) * mm, "end": v(-135.85, 32.87) * mm});
            skLineSegment(sketch, "E1309", {"start": v(-135.85, 32.87) * mm, "end": v(-136.3, 33.65) * mm});
            skLineSegment(sketch, "E1310", {"start": v(-136.3, 33.65) * mm, "end": v(-136.78, 34.42) * mm});
            skLineSegment(sketch, "E1311", {"start": v(-136.78, 34.42) * mm, "end": v(-137.28, 35.16) * mm});
            skLineSegment(sketch, "E1312", {"start": v(-137.28, 35.16) * mm, "end": v(-137.8, 35.89) * mm});
            skLineSegment(sketch, "E1313", {"start": v(-137.8, 35.89) * mm, "end": v(-138.34, 36.6) * mm});
            skLineSegment(sketch, "E1314", {"start": v(-138.34, 36.6) * mm, "end": v(-138.9, 37.3) * mm});
            skLineSegment(sketch, "E1315", {"start": v(-138.9, 37.3) * mm, "end": v(-139.5, 37.97) * mm});
            skLineSegment(sketch, "E1316", {"start": v(-139.5, 37.97) * mm, "end": v(-140.1, 38.63) * mm});
            skLineSegment(sketch, "E1317", {"start": v(-140.1, 38.63) * mm, "end": v(-140.74, 39.28) * mm});
            skLineSegment(sketch, "E1318", {"start": v(-140.74, 39.28) * mm, "end": v(-141.39, 39.9) * mm});
            skLineSegment(sketch, "E1319", {"start": v(-141.39, 39.9) * mm, "end": v(-142.05, 40.52) * mm});
            skLineSegment(sketch, "E1320", {"start": v(-142.05, 40.52) * mm, "end": v(-142.74, 41.12) * mm});
            skLineSegment(sketch, "E1321", {"start": v(-142.74, 41.12) * mm, "end": v(-143.45, 41.7) * mm});
            skLineSegment(sketch, "E1322", {"start": v(-143.45, 41.7) * mm, "end": v(-144.17, 42.27) * mm});
            skLineSegment(sketch, "E1323", {"start": v(-144.17, 42.27) * mm, "end": v(-144.9, 42.82) * mm});
            skLineSegment(sketch, "E1324", {"start": v(-144.9, 42.82) * mm, "end": v(-145.66, 43.35) * mm});
            skLineSegment(sketch, "E1325", {"start": v(-145.66, 43.35) * mm, "end": v(-146.43, 43.87) * mm});
            skLineSegment(sketch, "E1326", {"start": v(-146.43, 43.87) * mm, "end": v(-147.22, 44.38) * mm});
            skLineSegment(sketch, "E1327", {"start": v(-147.22, 44.38) * mm, "end": v(-148.02, 44.87) * mm});
            skLineSegment(sketch, "E1328", {"start": v(-148.02, 44.87) * mm, "end": v(-148.83, 45.35) * mm});
            skLineSegment(sketch, "E1329", {"start": v(-148.83, 45.35) * mm, "end": v(-149.66, 45.81) * mm});
            skLineSegment(sketch, "E1330", {"start": v(-149.66, 45.81) * mm, "end": v(-150.5, 46.26) * mm});
            skLineSegment(sketch, "E1331", {"start": v(-150.5, 46.26) * mm, "end": v(-151.35, 46.7) * mm});
            skLineSegment(sketch, "E1332", {"start": v(-151.35, 46.7) * mm, "end": v(-152.2, 47.12) * mm});
            skLineSegment(sketch, "E1333", {"start": v(-152.2, 47.12) * mm, "end": v(-153.08, 47.53) * mm});
            skLineSegment(sketch, "E1334", {"start": v(-153.08, 47.53) * mm, "end": v(-153.96, 47.92) * mm});
            skLineSegment(sketch, "E1335", {"start": v(-153.96, 47.92) * mm, "end": v(-154.85, 48.3) * mm});
            skLineSegment(sketch, "E1336", {"start": v(-154.85, 48.3) * mm, "end": v(-155.75, 48.67) * mm});
            skLineSegment(sketch, "E1337", {"start": v(-155.75, 48.67) * mm, "end": v(-156.66, 49.03) * mm});
            skLineSegment(sketch, "E1338", {"start": v(-156.66, 49.03) * mm, "end": v(-157.58, 49.37) * mm});
            skLineSegment(sketch, "E1339", {"start": v(-157.58, 49.37) * mm, "end": v(-158.5, 49.7) * mm});
            skLineSegment(sketch, "E1340", {"start": v(-158.5, 49.7) * mm, "end": v(-159.48, 50.03) * mm});
            skLineSegment(sketch, "E1341", {"start": v(-159.48, 50.03) * mm, "end": v(-160.46, 50.36) * mm});
            skLineSegment(sketch, "E1342", {"start": v(-160.46, 50.36) * mm, "end": v(-161.45, 50.66) * mm});
            skLineSegment(sketch, "E1343", {"start": v(-161.45, 50.66) * mm, "end": v(-162.43, 50.96) * mm});
            skLineSegment(sketch, "E1344", {"start": v(-162.43, 50.96) * mm, "end": v(-163.42, 51.24) * mm});
            skLineSegment(sketch, "E1345", {"start": v(-163.42, 51.24) * mm, "end": v(-164.4, 51.5) * mm});
            skLineSegment(sketch, "E1346", {"start": v(-164.4, 51.5) * mm, "end": v(-165.38, 51.76) * mm});
            skLineSegment(sketch, "E1347", {"start": v(-165.38, 51.76) * mm, "end": v(-166.37, 52) * mm});
            skLineSegment(sketch, "E1348", {"start": v(-166.37, 52) * mm, "end": v(-167.36, 52.24) * mm});
            skLineSegment(sketch, "E1349", {"start": v(-167.36, 52.24) * mm, "end": v(-168.34, 52.46) * mm});
            skLineSegment(sketch, "E1350", {"start": v(-168.34, 52.46) * mm, "end": v(-169.33, 52.66) * mm});
            skLineSegment(sketch, "E1351", {"start": v(-169.33, 52.66) * mm, "end": v(-170.32, 52.86) * mm});
            skLineSegment(sketch, "E1352", {"start": v(-170.32, 52.86) * mm, "end": v(-171.3, 53.05) * mm});
            skLineSegment(sketch, "E1353", {"start": v(-171.3, 53.05) * mm, "end": v(-172.3, 53.22) * mm});
            skLineSegment(sketch, "E1354", {"start": v(-172.3, 53.22) * mm, "end": v(-173.29, 53.38) * mm});
            skLineSegment(sketch, "E1355", {"start": v(-173.29, 53.38) * mm, "end": v(-174.28, 53.54) * mm});
            skLineSegment(sketch, "E1356", {"start": v(-174.28, 53.54) * mm, "end": v(-175.27, 53.68) * mm});
            skLineSegment(sketch, "E1357", {"start": v(-175.27, 53.68) * mm, "end": v(-176.27, 53.82) * mm});
            skLineSegment(sketch, "E1358", {"start": v(-176.27, 53.82) * mm, "end": v(-177.26, 53.95) * mm});
            skLineSegment(sketch, "E1359", {"start": v(-177.26, 53.95) * mm, "end": v(-178.26, 54.06) * mm});
            skLineSegment(sketch, "E1360", {"start": v(-178.26, 54.06) * mm, "end": v(-179.25, 54.17) * mm});
            skLineSegment(sketch, "E1361", {"start": v(-179.25, 54.17) * mm, "end": v(-180.25, 54.27) * mm});
            skLineSegment(sketch, "E1362", {"start": v(-180.25, 54.27) * mm, "end": v(-181.25, 54.37) * mm});
            skLineSegment(sketch, "E1363", {"start": v(-181.25, 54.37) * mm, "end": v(-182.25, 54.45) * mm});
            skLineSegment(sketch, "E1364", {"start": v(-182.25, 54.45) * mm, "end": v(-183.25, 54.53) * mm});
            skLineSegment(sketch, "E1365", {"start": v(-183.25, 54.53) * mm, "end": v(-184.25, 54.6) * mm});
            skLineSegment(sketch, "E1366", {"start": v(-184.25, 54.6) * mm, "end": v(-185.26, 54.67) * mm});
            skLineSegment(sketch, "E1367", {"start": v(-185.26, 54.67) * mm, "end": v(-186.26, 54.73) * mm});
            skLineSegment(sketch, "E1368", {"start": v(-186.26, 54.73) * mm, "end": v(-187.27, 54.78) * mm});
            skLineSegment(sketch, "E1369", {"start": v(-187.27, 54.78) * mm, "end": v(-188.28, 54.82) * mm});
            skLineSegment(sketch, "E1370", {"start": v(-188.28, 54.82) * mm, "end": v(-189.29, 54.87) * mm});
            skLineSegment(sketch, "E1371", {"start": v(-189.29, 54.87) * mm, "end": v(-190.3, 54.9) * mm});
            skLineSegment(sketch, "E1372", {"start": v(-190.3, 54.9) * mm, "end": v(-191.31, 54.93) * mm});
            skLineSegment(sketch, "E1373", {"start": v(-191.31, 54.93) * mm, "end": v(-192.33, 54.96) * mm});
            skLineSegment(sketch, "E1374", {"start": v(-192.33, 54.96) * mm, "end": v(-193.34, 54.98) * mm});
            skLineSegment(sketch, "E1375", {"start": v(-193.34, 54.98) * mm, "end": v(-194.36, 55) * mm});
            skLineSegment(sketch, "E1376", {"start": v(-194.36, 55) * mm, "end": v(-195.38, 55.01) * mm});
            skLineSegment(sketch, "E1377", {"start": v(-195.38, 55.01) * mm, "end": v(-196.4, 55.03) * mm});
            skLineSegment(sketch, "E1378", {"start": v(-196.4, 55.03) * mm, "end": v(-197.42, 55.03) * mm});
            skLineSegment(sketch, "E1379", {"start": v(-197.42, 55.03) * mm, "end": v(-198.45, 55.04) * mm});
            skLineSegment(sketch, "E1380", {"start": v(-198.45, 55.04) * mm, "end": v(-199.47, 55.04) * mm});
            skLineSegment(sketch, "E1381", {"start": v(-199.47, 55.04) * mm, "end": v(-200.5, 55.04) * mm});
            skLineSegment(sketch, "E1382", {"start": v(-200.5, 55.04) * mm, "end": v(-201.51, 55.04) * mm});
            skLineSegment(sketch, "E1383", {"start": v(-201.51, 55.04) * mm, "end": v(-202.53, 55.04) * mm});
            skLineSegment(sketch, "E1384", {"start": v(-202.53, 55.04) * mm, "end": v(-203.54, 55.04) * mm});
            skLineSegment(sketch, "E1385", {"start": v(-203.54, 55.04) * mm, "end": v(-204.55, 55.03) * mm});
            skLineSegment(sketch, "E1386", {"start": v(-204.55, 55.03) * mm, "end": v(-205.56, 55.03) * mm});
            skLineSegment(sketch, "E1387", {"start": v(-205.56, 55.03) * mm, "end": v(-206.57, 55.02) * mm});
            skLineSegment(sketch, "E1388", {"start": v(-206.57, 55.02) * mm, "end": v(-207.57, 55) * mm});
            skLineSegment(sketch, "E1389", {"start": v(-207.57, 55) * mm, "end": v(-208.58, 54.99) * mm});
            skLineSegment(sketch, "E1390", {"start": v(-208.58, 54.99) * mm, "end": v(-209.58, 54.97) * mm});
            skLineSegment(sketch, "E1391", {"start": v(-209.58, 54.97) * mm, "end": v(-210.58, 54.94) * mm});
            skLineSegment(sketch, "E1392", {"start": v(-210.58, 54.94) * mm, "end": v(-211.59, 54.91) * mm});
            skLineSegment(sketch, "E1393", {"start": v(-211.59, 54.91) * mm, "end": v(-212.59, 54.88) * mm});
            skLineSegment(sketch, "E1394", {"start": v(-212.59, 54.88) * mm, "end": v(-213.59, 54.84) * mm});
            skLineSegment(sketch, "E1395", {"start": v(-213.59, 54.84) * mm, "end": v(-214.59, 54.8) * mm});
            skLineSegment(sketch, "E1396", {"start": v(-214.59, 54.8) * mm, "end": v(-215.59, 54.75) * mm});
            skLineSegment(sketch, "E1397", {"start": v(-215.59, 54.75) * mm, "end": v(-216.58, 54.7) * mm});
            skLineSegment(sketch, "E1398", {"start": v(-216.58, 54.7) * mm, "end": v(-217.58, 54.63) * mm});
            skLineSegment(sketch, "E1399", {"start": v(-217.58, 54.63) * mm, "end": v(-218.58, 54.56) * mm});
            skLineSegment(sketch, "E1400", {"start": v(-218.58, 54.56) * mm, "end": v(-219.57, 54.48) * mm});
            skLineSegment(sketch, "E1401", {"start": v(-219.57, 54.48) * mm, "end": v(-220.57, 54.4) * mm});
            skLineSegment(sketch, "E1402", {"start": v(-220.57, 54.4) * mm, "end": v(-221.56, 54.3) * mm});
            skLineSegment(sketch, "E1403", {"start": v(-221.56, 54.3) * mm, "end": v(-222.56, 54.2) * mm});
            skLineSegment(sketch, "E1404", {"start": v(-222.56, 54.2) * mm, "end": v(-223.55, 54.08) * mm});
            skLineSegment(sketch, "E1405", {"start": v(-223.55, 54.08) * mm, "end": v(-224.55, 53.96) * mm});
            skLineSegment(sketch, "E1406", {"start": v(-224.55, 53.96) * mm, "end": v(-225.54, 53.83) * mm});
            skLineSegment(sketch, "E1407", {"start": v(-225.54, 53.83) * mm, "end": v(-226.54, 53.7) * mm});
            skLineSegment(sketch, "E1408", {"start": v(-226.54, 53.7) * mm, "end": v(-227.53, 53.54) * mm});
            skLineSegment(sketch, "E1409", {"start": v(-227.53, 53.54) * mm, "end": v(-228.53, 53.38) * mm});
            skLineSegment(sketch, "E1410", {"start": v(-228.53, 53.38) * mm, "end": v(-229.52, 53.2) * mm});
            skLineSegment(sketch, "E1411", {"start": v(-229.52, 53.2) * mm, "end": v(-230.52, 53.02) * mm});
            skLineSegment(sketch, "E1412", {"start": v(-230.52, 53.02) * mm, "end": v(-231.5, 52.82) * mm});
            skLineSegment(sketch, "E1413", {"start": v(-231.5, 52.82) * mm, "end": v(-232.5, 52.61) * mm});
            skLineSegment(sketch, "E1414", {"start": v(-232.5, 52.61) * mm, "end": v(-233.5, 52.4) * mm});
            skLineSegment(sketch, "E1415", {"start": v(-233.5, 52.4) * mm, "end": v(-234.44, 52.17) * mm});
            skLineSegment(sketch, "E1416", {"start": v(-234.44, 52.17) * mm, "end": v(-235.38, 51.94) * mm});
            skLineSegment(sketch, "E1417", {"start": v(-235.38, 51.94) * mm, "end": v(-236.32, 51.7) * mm});
            skLineSegment(sketch, "E1418", {"start": v(-236.32, 51.7) * mm, "end": v(-237.27, 51.45) * mm});
            skLineSegment(sketch, "E1419", {"start": v(-237.27, 51.45) * mm, "end": v(-238.22, 51.19) * mm});
            skLineSegment(sketch, "E1420", {"start": v(-238.22, 51.19) * mm, "end": v(-239.16, 50.9) * mm});
            skLineSegment(sketch, "E1421", {"start": v(-239.16, 50.9) * mm, "end": v(-240.11, 50.62) * mm});
            skLineSegment(sketch, "E1422", {"start": v(-240.11, 50.62) * mm, "end": v(-241.06, 50.32) * mm});
            skLineSegment(sketch, "E1423", {"start": v(-241.06, 50.32) * mm, "end": v(-242, 50) * mm});
            skLineSegment(sketch, "E1424", {"start": v(-242, 50) * mm, "end": v(-242.93, 49.66) * mm});
            skLineSegment(sketch, "E1425", {"start": v(-242.93, 49.66) * mm, "end": v(-243.87, 49.31) * mm});
            skLineSegment(sketch, "E1426", {"start": v(-243.87, 49.31) * mm, "end": v(-244.8, 48.95) * mm});
            skLineSegment(sketch, "E1427", {"start": v(-244.8, 48.95) * mm, "end": v(-245.71, 48.56) * mm});
            skLineSegment(sketch, "E1428", {"start": v(-245.71, 48.56) * mm, "end": v(-246.62, 48.16) * mm});
            skLineSegment(sketch, "E1429", {"start": v(-246.62, 48.16) * mm, "end": v(-247.52, 47.74) * mm});
            skLineSegment(sketch, "E1430", {"start": v(-247.52, 47.74) * mm, "end": v(-248.4, 47.3) * mm});
            skLineSegment(sketch, "E1431", {"start": v(-248.4, 47.3) * mm, "end": v(-249.29, 46.84) * mm});
            skLineSegment(sketch, "E1432", {"start": v(-249.29, 46.84) * mm, "end": v(-250.15, 46.36) * mm});
            skLineSegment(sketch, "E1433", {"start": v(-250.15, 46.36) * mm, "end": v(-251, 45.87) * mm});
            skLineSegment(sketch, "E1434", {"start": v(-251, 45.87) * mm, "end": v(-251.83, 45.35) * mm});
            skLineSegment(sketch, "E1435", {"start": v(-251.83, 45.35) * mm, "end": v(-252.65, 44.8) * mm});
            skLineSegment(sketch, "E1436", {"start": v(-252.65, 44.8) * mm, "end": v(-253.45, 44.24) * mm});
            skLineSegment(sketch, "E1437", {"start": v(-253.45, 44.24) * mm, "end": v(-254.24, 43.65) * mm});
            skLineSegment(sketch, "E1438", {"start": v(-254.24, 43.65) * mm, "end": v(-255, 43.04) * mm});
            skLineSegment(sketch, "E1439", {"start": v(-255, 43.04) * mm, "end": v(-255.74, 42.4) * mm});
            skLineSegment(sketch, "E1440", {"start": v(-255.74, 42.4) * mm, "end": v(-256.46, 41.74) * mm});
            skLineSegment(sketch, "E1441", {"start": v(-256.46, 41.74) * mm, "end": v(-257.16, 41.05) * mm});
            skLineSegment(sketch, "E1442", {"start": v(-257.16, 41.05) * mm, "end": v(-257.83, 40.34) * mm});
            skLineSegment(sketch, "E1443", {"start": v(-257.83, 40.34) * mm, "end": v(-258.48, 39.6) * mm});
            skLineSegment(sketch, "E1444", {"start": v(-258.48, 39.6) * mm, "end": v(-259.1, 38.83) * mm});
            skLineSegment(sketch, "E1445", {"start": v(-259.1, 38.83) * mm, "end": v(-259.7, 38.03) * mm});
            skLineSegment(sketch, "E1446", {"start": v(-259.7, 38.03) * mm, "end": v(-260.27, 37.2) * mm});
            skLineSegment(sketch, "E1447", {"start": v(-260.27, 37.2) * mm, "end": v(-260.8, 36.36) * mm});
            skLineSegment(sketch, "E1448", {"start": v(-260.8, 36.36) * mm, "end": v(-261.29, 35.49) * mm});
            skLineSegment(sketch, "E1449", {"start": v(-261.29, 35.49) * mm, "end": v(-261.74, 34.6) * mm});
            skLineSegment(sketch, "E1450", {"start": v(-261.74, 34.6) * mm, "end": v(-262.16, 33.7) * mm});
            skLineSegment(sketch, "E1451", {"start": v(-262.16, 33.7) * mm, "end": v(-262.55, 32.78) * mm});
            skLineSegment(sketch, "E1452", {"start": v(-262.55, 32.78) * mm, "end": v(-262.9, 31.84) * mm});
            skLineSegment(sketch, "E1453", {"start": v(-262.9, 31.84) * mm, "end": v(-263.21, 30.9) * mm});
            skLineSegment(sketch, "E1454", {"start": v(-263.21, 30.9) * mm, "end": v(-263.5, 29.94) * mm});
            skLineSegment(sketch, "E1455", {"start": v(-263.5, 29.94) * mm, "end": v(-263.73, 28.97) * mm});
            skLineSegment(sketch, "E1456", {"start": v(-263.73, 28.97) * mm, "end": v(-263.94, 28) * mm});
            skLineSegment(sketch, "E1457", {"start": v(-263.94, 28) * mm, "end": v(-264.12, 27) * mm});
            skLineSegment(sketch, "E1458", {"start": v(-264.12, 27) * mm, "end": v(-264.26, 26.02) * mm});
            skLineSegment(sketch, "E1459", {"start": v(-264.26, 26.02) * mm, "end": v(-264.37, 25.03) * mm});
            skLineSegment(sketch, "E1460", {"start": v(-264.37, 25.03) * mm, "end": v(-264.44, 24.04) * mm});
            skLineSegment(sketch, "E1461", {"start": v(-264.44, 24.04) * mm, "end": v(-264.49, 23.04) * mm});
            skLineSegment(sketch, "E1462", {"start": v(-264.49, 23.04) * mm, "end": v(-264.5, 22.03) * mm});
            skLineSegment(sketch, "E1463", {"start": v(-264.5, 22.03) * mm, "end": v(-264.5, 21.02) * mm});
            skLineSegment(sketch, "E1464", {"start": v(-264.5, 21.02) * mm, "end": v(-264.48, 20) * mm});
            skLineSegment(sketch, "E1465", {"start": v(-264.48, 20) * mm, "end": v(-264.44, 19) * mm});
            skLineSegment(sketch, "E1466", {"start": v(-264.44, 19) * mm, "end": v(-264.37, 18) * mm});
            skLineSegment(sketch, "E1467", {"start": v(-264.37, 18) * mm, "end": v(-264.28, 17) * mm});
            skLineSegment(sketch, "E1468", {"start": v(-264.28, 17) * mm, "end": v(-264.16, 16) * mm});
            skLineSegment(sketch, "E1469", {"start": v(-264.16, 16) * mm, "end": v(-264, 15) * mm});
            skLineSegment(sketch, "E1470", {"start": v(-264, 15) * mm, "end": v(-263.81, 14.02) * mm});
            skLineSegment(sketch, "E1471", {"start": v(-263.81, 14.02) * mm, "end": v(-263.6, 13.03) * mm});
            skLineSegment(sketch, "E1472", {"start": v(-263.6, 13.03) * mm, "end": v(-263.33, 12.04) * mm});
            skLineSegment(sketch, "E1473", {"start": v(-263.33, 12.04) * mm, "end": v(-263.05, 11.12) * mm});
            skLineSegment(sketch, "E1474", {"start": v(-263.05, 11.12) * mm, "end": v(-262.75, 10.22) * mm});
            skLineSegment(sketch, "E1475", {"start": v(-262.75, 10.22) * mm, "end": v(-262.42, 9.35) * mm});
            skLineSegment(sketch, "E1476", {"start": v(-262.42, 9.35) * mm, "end": v(-262.07, 8.5) * mm});
            skLineSegment(sketch, "E1477", {"start": v(-262.07, 8.5) * mm, "end": v(-261.7, 7.67) * mm});
            skLineSegment(sketch, "E1478", {"start": v(-261.7, 7.67) * mm, "end": v(-261.3, 6.86) * mm});
            skLineSegment(sketch, "E1479", {"start": v(-261.3, 6.86) * mm, "end": v(-260.89, 6.07) * mm});
            skLineSegment(sketch, "E1480", {"start": v(-260.89, 6.07) * mm, "end": v(-260.45, 5.3) * mm});
            skLineSegment(sketch, "E1481", {"start": v(-260.45, 5.3) * mm, "end": v(-260, 4.57) * mm});
            skLineSegment(sketch, "E1482", {"start": v(-260, 4.57) * mm, "end": v(-259.51, 3.84) * mm});
            skLineSegment(sketch, "E1483", {"start": v(-259.51, 3.84) * mm, "end": v(-259.02, 3.14) * mm});
            skLineSegment(sketch, "E1484", {"start": v(-259.02, 3.14) * mm, "end": v(-258.5, 2.46) * mm});
            skLineSegment(sketch, "E1485", {"start": v(-258.5, 2.46) * mm, "end": v(-257.96, 1.8) * mm});
            skLineSegment(sketch, "E1486", {"start": v(-257.96, 1.8) * mm, "end": v(-257.4, 1.15) * mm});
            skLineSegment(sketch, "E1487", {"start": v(-257.4, 1.15) * mm, "end": v(-256.83, 0.52) * mm});
            skLineSegment(sketch, "E1488", {"start": v(-256.83, 0.52) * mm, "end": v(-256.24, -0.08) * mm});
            skLineSegment(sketch, "E1489", {"start": v(-256.24, -0.08) * mm, "end": v(-255.64, -0.67) * mm});
            skLineSegment(sketch, "E1490", {"start": v(-255.64, -0.67) * mm, "end": v(-255.01, -1.24) * mm});
            skLineSegment(sketch, "E1491", {"start": v(-255.01, -1.24) * mm, "end": v(-254.37, -1.8) * mm});
            skLineSegment(sketch, "E1492", {"start": v(-254.37, -1.8) * mm, "end": v(-253.71, -2.33) * mm});
            skLineSegment(sketch, "E1493", {"start": v(-253.71, -2.33) * mm, "end": v(-253.04, -2.85) * mm});
            skLineSegment(sketch, "E1494", {"start": v(-253.04, -2.85) * mm, "end": v(-252.36, -3.35) * mm});
            skLineSegment(sketch, "E1495", {"start": v(-252.36, -3.35) * mm, "end": v(-251.65, -3.83) * mm});
            skLineSegment(sketch, "E1496", {"start": v(-251.65, -3.83) * mm, "end": v(-250.94, -4.3) * mm});
            skLineSegment(sketch, "E1497", {"start": v(-250.94, -4.3) * mm, "end": v(-250.21, -4.75) * mm});
            skLineSegment(sketch, "E1498", {"start": v(-250.21, -4.75) * mm, "end": v(-249.47, -5.2) * mm});
            skLineSegment(sketch, "E1499", {"start": v(-249.47, -5.2) * mm, "end": v(-248.71, -5.62) * mm});
            skLineSegment(sketch, "E1500", {"start": v(-248.71, -5.62) * mm, "end": v(-247.95, -6.02) * mm});
            skLineSegment(sketch, "E1501", {"start": v(-247.95, -6.02) * mm, "end": v(-247.17, -6.42) * mm});
            skLineSegment(sketch, "E1502", {"start": v(-247.17, -6.42) * mm, "end": v(-246.38, -6.8) * mm});
            skLineSegment(sketch, "E1503", {"start": v(-246.38, -6.8) * mm, "end": v(-245.58, -7.17) * mm});
            skLineSegment(sketch, "E1504", {"start": v(-245.58, -7.17) * mm, "end": v(-244.77, -7.52) * mm});
            skLineSegment(sketch, "E1505", {"start": v(-244.77, -7.52) * mm, "end": v(-243.94, -7.86) * mm});
            skLineSegment(sketch, "E1506", {"start": v(-243.94, -7.86) * mm, "end": v(-243.11, -8.19) * mm});
            skLineSegment(sketch, "E1507", {"start": v(-243.11, -8.19) * mm, "end": v(-242.27, -8.5) * mm});
            skLineSegment(sketch, "E1508", {"start": v(-242.27, -8.5) * mm, "end": v(-241.42, -8.8) * mm});
            skLineSegment(sketch, "E1509", {"start": v(-241.42, -8.8) * mm, "end": v(-240.57, -9.1) * mm});
            skLineSegment(sketch, "E1510", {"start": v(-240.57, -9.1) * mm, "end": v(-239.7, -9.38) * mm});
            skLineSegment(sketch, "E1511", {"start": v(-239.7, -9.38) * mm, "end": v(-238.83, -9.65) * mm});
            skLineSegment(sketch, "E1512", {"start": v(-238.83, -9.65) * mm, "end": v(-237.95, -9.9) * mm});
            skLineSegment(sketch, "E1513", {"start": v(-237.95, -9.9) * mm, "end": v(-237.07, -10.16) * mm});
            skLineSegment(sketch, "E1514", {"start": v(-237.07, -10.16) * mm, "end": v(-236.18, -10.4) * mm});
            skLineSegment(sketch, "E1515", {"start": v(-236.18, -10.4) * mm, "end": v(-235.28, -10.62) * mm});
            skLineSegment(sketch, "E1516", {"start": v(-235.28, -10.62) * mm, "end": v(-234.38, -10.85) * mm});
            skLineSegment(sketch, "E1517", {"start": v(-234.38, -10.85) * mm, "end": v(-233.47, -11.06) * mm});
            skLineSegment(sketch, "E1518", {"start": v(-233.47, -11.06) * mm, "end": v(-232.56, -11.26) * mm});
            skLineSegment(sketch, "E1519", {"start": v(-232.56, -11.26) * mm, "end": v(-231.64, -11.45) * mm});
            skLineSegment(sketch, "E1520", {"start": v(-231.64, -11.45) * mm, "end": v(-230.73, -11.64) * mm});
            skLineSegment(sketch, "E1521", {"start": v(-230.73, -11.64) * mm, "end": v(-229.8, -11.82) * mm});
            skLineSegment(sketch, "E1522", {"start": v(-229.8, -11.82) * mm, "end": v(-228.88, -11.99) * mm});
            skLineSegment(sketch, "E1523", {"start": v(-228.88, -11.99) * mm, "end": v(-227.96, -12.15) * mm});
            skLineSegment(sketch, "E1524", {"start": v(-227.96, -12.15) * mm, "end": v(-227.03, -12.31) * mm});
            skLineSegment(sketch, "E1525", {"start": v(-227.03, -12.31) * mm, "end": v(-226.1, -12.46) * mm});
            skLineSegment(sketch, "E1526", {"start": v(-226.1, -12.46) * mm, "end": v(-225.17, -12.6) * mm});
            skLineSegment(sketch, "E1527", {"start": v(-225.17, -12.6) * mm, "end": v(-224.25, -12.75) * mm});
            skLineSegment(sketch, "E1528", {"start": v(-224.25, -12.75) * mm, "end": v(-223.32, -12.88) * mm});
            skLineSegment(sketch, "E1529", {"start": v(-223.32, -12.88) * mm, "end": v(-222.39, -13.01) * mm});
            skLineSegment(sketch, "E1530", {"start": v(-222.39, -13.01) * mm, "end": v(-221.46, -13.14) * mm});
            skLineSegment(sketch, "E1531", {"start": v(-221.46, -13.14) * mm, "end": v(-220.54, -13.26) * mm});
            skLineSegment(sketch, "E1532", {"start": v(-220.54, -13.26) * mm, "end": v(-219.61, -13.38) * mm});
            skLineSegment(sketch, "E1533", {"start": v(-219.61, -13.38) * mm, "end": v(-218.7, -13.5) * mm});
            skLineSegment(sketch, "E1534", {"start": v(-218.7, -13.5) * mm, "end": v(-217.78, -13.6) * mm});
            skLineSegment(sketch, "E1535", {"start": v(-217.78, -13.6) * mm, "end": v(-216.86, -13.7) * mm});
            skLineSegment(sketch, "E1536", {"start": v(-216.86, -13.7) * mm, "end": v(-215.95, -13.81) * mm});
            skLineSegment(sketch, "E1537", {"start": v(-215.95, -13.81) * mm, "end": v(-215.05, -13.92) * mm});
            skLineSegment(sketch, "E1538", {"start": v(-215.05, -13.92) * mm, "end": v(-214.15, -14.02) * mm});
            skLineSegment(sketch, "E1539", {"start": v(-214.15, -14.02) * mm, "end": v(-213.25, -14.12) * mm});
            skLineSegment(sketch, "E1540", {"start": v(-213.25, -14.12) * mm, "end": v(-212.36, -14.22) * mm});
            skLineSegment(sketch, "E1541", {"start": v(-212.36, -14.22) * mm, "end": v(-211.48, -14.31) * mm});
            skLineSegment(sketch, "E1542", {"start": v(-211.48, -14.31) * mm, "end": v(-210.6, -14.4) * mm});
            skLineSegment(sketch, "E1543", {"start": v(-210.6, -14.4) * mm, "end": v(-209.73, -14.5) * mm});
            skLineSegment(sketch, "E1544", {"start": v(-209.73, -14.5) * mm, "end": v(-208.86, -14.6) * mm});
            skLineSegment(sketch, "E1545", {"start": v(-208.86, -14.6) * mm, "end": v(-208, -14.7) * mm});
            skLineSegment(sketch, "E1546", {"start": v(-208, -14.7) * mm, "end": v(-207.16, -14.8) * mm});
            skLineSegment(sketch, "E1547", {"start": v(-207.16, -14.8) * mm, "end": v(-206.32, -14.9) * mm});
            skLineSegment(sketch, "E1548", {"start": v(-206.32, -14.9) * mm, "end": v(-205.5, -15) * mm});
            skLineSegment(sketch, "E1549", {"start": v(-205.5, -15) * mm, "end": v(-204.67, -15.1) * mm});
            skLineSegment(sketch, "E1550", {"start": v(-204.67, -15.1) * mm, "end": v(-203.86, -15.2) * mm});
            skLineSegment(sketch, "E1551", {"start": v(-203.86, -15.2) * mm, "end": v(-203.06, -15.3) * mm});
            skLineSegment(sketch, "E1552", {"start": v(-203.06, -15.3) * mm, "end": v(-202.28, -15.42) * mm});
            skLineSegment(sketch, "E1553", {"start": v(-202.28, -15.42) * mm, "end": v(-201.5, -15.53) * mm});
            skLineSegment(sketch, "E1554", {"start": v(-201.5, -15.53) * mm, "end": v(-200.59, -15.66) * mm});
            skLineSegment(sketch, "E1555", {"start": v(-200.59, -15.66) * mm, "end": v(-199.66, -15.77) * mm});
            skLineSegment(sketch, "E1556", {"start": v(-199.66, -15.77) * mm, "end": v(-198.7, -15.88) * mm});
            skLineSegment(sketch, "E1557", {"start": v(-198.7, -15.88) * mm, "end": v(-197.73, -15.98) * mm});
            skLineSegment(sketch, "E1558", {"start": v(-197.73, -15.98) * mm, "end": v(-196.74, -16.07) * mm});
            skLineSegment(sketch, "E1559", {"start": v(-196.74, -16.07) * mm, "end": v(-195.74, -16.17) * mm});
            skLineSegment(sketch, "E1560", {"start": v(-195.74, -16.17) * mm, "end": v(-194.73, -16.27) * mm});
            skLineSegment(sketch, "E1561", {"start": v(-194.73, -16.27) * mm, "end": v(-193.72, -16.38) * mm});
            skLineSegment(sketch, "E1562", {"start": v(-193.72, -16.38) * mm, "end": v(-192.7, -16.5) * mm});
            skLineSegment(sketch, "E1563", {"start": v(-192.7, -16.5) * mm, "end": v(-191.68, -16.62) * mm});
            skLineSegment(sketch, "E1564", {"start": v(-191.68, -16.62) * mm, "end": v(-190.66, -16.76) * mm});
            skLineSegment(sketch, "E1565", {"start": v(-190.66, -16.76) * mm, "end": v(-189.65, -16.92) * mm});
            skLineSegment(sketch, "E1566", {"start": v(-189.65, -16.92) * mm, "end": v(-188.64, -17.1) * mm});
            skLineSegment(sketch, "E1567", {"start": v(-188.64, -17.1) * mm, "end": v(-187.65, -17.3) * mm});
            skLineSegment(sketch, "E1568", {"start": v(-187.65, -17.3) * mm, "end": v(-186.66, -17.53) * mm});
            skLineSegment(sketch, "E1569", {"start": v(-186.66, -17.53) * mm, "end": v(-185.7, -17.8) * mm});
            skLineSegment(sketch, "E1570", {"start": v(-185.7, -17.8) * mm, "end": v(-184.75, -18.08) * mm});
            skLineSegment(sketch, "E1571", {"start": v(-184.75, -18.08) * mm, "end": v(-183.82, -18.4) * mm});
            skLineSegment(sketch, "E1572", {"start": v(-183.82, -18.4) * mm, "end": v(-182.92, -18.77) * mm});
            skLineSegment(sketch, "E1573", {"start": v(-182.92, -18.77) * mm, "end": v(-182.04, -19.17) * mm});
            skLineSegment(sketch, "E1574", {"start": v(-182.04, -19.17) * mm, "end": v(-181.2, -19.62) * mm});
            skLineSegment(sketch, "E1575", {"start": v(-181.2, -19.62) * mm, "end": v(-180.39, -20.12) * mm});
            skLineSegment(sketch, "E1576", {"start": v(-180.39, -20.12) * mm, "end": v(-179.6, -20.66) * mm});
            skLineSegment(sketch, "E1577", {"start": v(-179.6, -20.66) * mm, "end": v(-178.82, -21.32) * mm});
            skLineSegment(sketch, "E1578", {"start": v(-178.82, -21.32) * mm, "end": v(-178.15, -22) * mm});
            skLineSegment(sketch, "E1579", {"start": v(-178.15, -22) * mm, "end": v(-177.6, -22.7) * mm});
            skLineSegment(sketch, "E1580", {"start": v(-177.6, -22.7) * mm, "end": v(-177.18, -23.41) * mm});
            skLineSegment(sketch, "E1581", {"start": v(-177.18, -23.41) * mm, "end": v(-176.88, -24.13) * mm});
            skLineSegment(sketch, "E1582", {"start": v(-176.88, -24.13) * mm, "end": v(-176.69, -24.86) * mm});
            skLineSegment(sketch, "E1583", {"start": v(-176.69, -24.86) * mm, "end": v(-176.6, -25.58) * mm});
            skLineSegment(sketch, "E1584", {"start": v(-176.6, -25.58) * mm, "end": v(-176.64, -26.29) * mm});
            skLineSegment(sketch, "E1585", {"start": v(-176.64, -26.29) * mm, "end": v(-176.78, -26.98) * mm});
            skLineSegment(sketch, "E1586", {"start": v(-176.78, -26.98) * mm, "end": v(-177.03, -27.66) * mm});
            skLineSegment(sketch, "E1587", {"start": v(-177.03, -27.66) * mm, "end": v(-177.38, -28.3) * mm});
            skLineSegment(sketch, "E1588", {"start": v(-177.38, -28.3) * mm, "end": v(-177.83, -28.92) * mm});
            skLineSegment(sketch, "E1589", {"start": v(-177.83, -28.92) * mm, "end": v(-178.38, -29.5) * mm});
            skLineSegment(sketch, "E1590", {"start": v(-178.38, -29.5) * mm, "end": v(-179.02, -30.04) * mm});
            skLineSegment(sketch, "E1591", {"start": v(-179.02, -30.04) * mm, "end": v(-179.76, -30.52) * mm});
            skLineSegment(sketch, "E1592", {"start": v(-179.76, -30.52) * mm, "end": v(-180.6, -30.95) * mm});
            skLineSegment(sketch, "E1593", {"start": v(-180.6, -30.95) * mm, "end": v(-181.52, -31.32) * mm});
            skLineSegment(sketch, "E1594", {"start": v(-181.52, -31.32) * mm, "end": v(-182.45, -31.62) * mm});
            skLineSegment(sketch, "E1595", {"start": v(-182.45, -31.62) * mm, "end": v(-183.4, -31.9) * mm});
            skLineSegment(sketch, "E1596", {"start": v(-183.4, -31.9) * mm, "end": v(-184.38, -32.13) * mm});
            skLineSegment(sketch, "E1597", {"start": v(-184.38, -32.13) * mm, "end": v(-185.38, -32.34) * mm});
            skLineSegment(sketch, "E1598", {"start": v(-185.38, -32.34) * mm, "end": v(-186.39, -32.5) * mm});
            skLineSegment(sketch, "E1599", {"start": v(-186.39, -32.5) * mm, "end": v(-187.4, -32.64) * mm});
            skLineSegment(sketch, "E1600", {"start": v(-187.4, -32.64) * mm, "end": v(-188.43, -32.74) * mm});
            skLineSegment(sketch, "E1601", {"start": v(-188.43, -32.74) * mm, "end": v(-189.47, -32.81) * mm});
            skLineSegment(sketch, "E1602", {"start": v(-189.47, -32.81) * mm, "end": v(-190.51, -32.84) * mm});
            skLineSegment(sketch, "E1603", {"start": v(-190.51, -32.84) * mm, "end": v(-191.56, -32.84) * mm});
            skLineSegment(sketch, "E1604", {"start": v(-191.56, -32.84) * mm, "end": v(-192.6, -32.8) * mm});
            skLineSegment(sketch, "E1605", {"start": v(-192.6, -32.8) * mm, "end": v(-193.64, -32.74) * mm});
            skLineSegment(sketch, "E1606", {"start": v(-193.64, -32.74) * mm, "end": v(-194.68, -32.64) * mm});
            skLineSegment(sketch, "E1607", {"start": v(-194.68, -32.64) * mm, "end": v(-195.7, -32.5) * mm});
            skLineSegment(sketch, "E1608", {"start": v(-195.7, -32.5) * mm, "end": v(-196.72, -32.33) * mm});
            skLineSegment(sketch, "E1609", {"start": v(-196.72, -32.33) * mm, "end": v(-197.73, -32.13) * mm});
            skLineSegment(sketch, "E1610", {"start": v(-197.73, -32.13) * mm, "end": v(-198.72, -31.89) * mm});
            skLineSegment(sketch, "E1611", {"start": v(-198.72, -31.89) * mm, "end": v(-199.7, -31.61) * mm});
            skLineSegment(sketch, "E1612", {"start": v(-199.7, -31.61) * mm, "end": v(-200.66, -31.3) * mm});
            skLineSegment(sketch, "E1613", {"start": v(-200.66, -31.3) * mm, "end": v(-201.59, -30.97) * mm});
            skLineSegment(sketch, "E1614", {"start": v(-201.59, -30.97) * mm, "end": v(-202.5, -30.59) * mm});
            skLineSegment(sketch, "E1615", {"start": v(-202.5, -30.59) * mm, "end": v(-203.4, -30.14) * mm});
            skLineSegment(sketch, "E1616", {"start": v(-203.4, -30.14) * mm, "end": v(-204.24, -29.63) * mm});
            skLineSegment(sketch, "E1617", {"start": v(-204.24, -29.63) * mm, "end": v(-205.03, -29.05) * mm});
            skLineSegment(sketch, "E1618", {"start": v(-205.03, -29.05) * mm, "end": v(-205.78, -28.42) * mm});
            skLineSegment(sketch, "E1619", {"start": v(-205.78, -28.42) * mm, "end": v(-206.5, -27.76) * mm});
            skLineSegment(sketch, "E1620", {"start": v(-206.5, -27.76) * mm, "end": v(-207.2, -27.07) * mm});
            skLineSegment(sketch, "E1621", {"start": v(-207.2, -27.07) * mm, "end": v(-207.88, -26.37) * mm});
            skLineSegment(sketch, "E1622", {"start": v(-207.88, -26.37) * mm, "end": v(-208.55, -25.66) * mm});
            skLineSegment(sketch, "E1623", {"start": v(-208.55, -25.66) * mm, "end": v(-209.22, -24.96) * mm});
            skLineSegment(sketch, "E1624", {"start": v(-209.22, -24.96) * mm, "end": v(-209.9, -24.28) * mm});
            skLineSegment(sketch, "E1625", {"start": v(-209.9, -24.28) * mm, "end": v(-210.6, -23.63) * mm});
            skLineSegment(sketch, "E1626", {"start": v(-210.6, -23.63) * mm, "end": v(-211.32, -23.02) * mm});
            skLineSegment(sketch, "E1627", {"start": v(-211.32, -23.02) * mm, "end": v(-212.07, -22.46) * mm});
            skLineSegment(sketch, "E1628", {"start": v(-212.07, -22.46) * mm, "end": v(-212.87, -21.97) * mm});
            skLineSegment(sketch, "E1629", {"start": v(-212.87, -21.97) * mm, "end": v(-213.7, -21.56) * mm});
            skLineSegment(sketch, "E1630", {"start": v(-213.7, -21.56) * mm, "end": v(-214.55, -21.25) * mm});
            skLineSegment(sketch, "E1631", {"start": v(-214.55, -21.25) * mm, "end": v(-215.44, -21) * mm});
            skLineSegment(sketch, "E1632", {"start": v(-215.44, -21) * mm, "end": v(-216.38, -20.82) * mm});
            skLineSegment(sketch, "E1633", {"start": v(-216.38, -20.82) * mm, "end": v(-217.35, -20.68) * mm});
            skLineSegment(sketch, "E1634", {"start": v(-217.35, -20.68) * mm, "end": v(-218.36, -20.6) * mm});
            skLineSegment(sketch, "E1635", {"start": v(-218.36, -20.6) * mm, "end": v(-219.39, -20.56) * mm});
            skLineSegment(sketch, "E1636", {"start": v(-219.39, -20.56) * mm, "end": v(-220.43, -20.55) * mm});
            skLineSegment(sketch, "E1637", {"start": v(-220.43, -20.55) * mm, "end": v(-221.49, -20.56) * mm});
            skLineSegment(sketch, "E1638", {"start": v(-221.49, -20.56) * mm, "end": v(-222.55, -20.6) * mm});
            skLineSegment(sketch, "E1639", {"start": v(-222.55, -20.6) * mm, "end": v(-223.6, -20.66) * mm});
            skLineSegment(sketch, "E1640", {"start": v(-223.6, -20.66) * mm, "end": v(-224.65, -20.72) * mm});
            skLineSegment(sketch, "E1641", {"start": v(-224.65, -20.72) * mm, "end": v(-225.69, -20.8) * mm});
            skLineSegment(sketch, "E1642", {"start": v(-225.69, -20.8) * mm, "end": v(-226.7, -20.85) * mm});
            skLineSegment(sketch, "E1643", {"start": v(-226.7, -20.85) * mm, "end": v(-227.67, -20.9) * mm});
            skLineSegment(sketch, "E1644", {"start": v(-227.67, -20.9) * mm, "end": v(-228.6, -20.94) * mm});
            skLineSegment(sketch, "E1645", {"start": v(-228.6, -20.94) * mm, "end": v(-229.5, -20.96) * mm});
            skLineSegment(sketch, "E1646", {"start": v(-229.5, -20.96) * mm, "end": v(-265.5, -20.96) * mm});
            skLineSegment(sketch, "E1647", {"start": v(-118.5, 53.04) * mm, "end": v(-118.5, -6.96) * mm});
            skLineSegment(sketch, "E1648", {"start": v(-118.5, -6.96) * mm, "end": v(-118.5, -7.92) * mm});
            skLineSegment(sketch, "E1649", {"start": v(-118.5, -7.92) * mm, "end": v(-118.5, -8.88) * mm});
            skLineSegment(sketch, "E1650", {"start": v(-118.5, -8.88) * mm, "end": v(-118.5, -9.86) * mm});
            skLineSegment(sketch, "E1651", {"start": v(-118.5, -9.86) * mm, "end": v(-118.5, -10.85) * mm});
            skLineSegment(sketch, "E1652", {"start": v(-118.5, -10.85) * mm, "end": v(-118.5, -11.84) * mm});
            skLineSegment(sketch, "E1653", {"start": v(-118.5, -11.84) * mm, "end": v(-118.5, -12.83) * mm});
            skLineSegment(sketch, "E1654", {"start": v(-118.5, -12.83) * mm, "end": v(-118.5, -13.84) * mm});
            skLineSegment(sketch, "E1655", {"start": v(-118.5, -13.84) * mm, "end": v(-118.49, -14.85) * mm});
            skLineSegment(sketch, "E1656", {"start": v(-118.49, -14.85) * mm, "end": v(-118.47, -15.86) * mm});
            skLineSegment(sketch, "E1657", {"start": v(-118.47, -15.86) * mm, "end": v(-118.45, -16.87) * mm});
            skLineSegment(sketch, "E1658", {"start": v(-118.45, -16.87) * mm, "end": v(-118.42, -17.9) * mm});
            skLineSegment(sketch, "E1659", {"start": v(-118.42, -17.9) * mm, "end": v(-118.38, -18.9) * mm});
            skLineSegment(sketch, "E1660", {"start": v(-118.38, -18.9) * mm, "end": v(-118.33, -19.93) * mm});
            skLineSegment(sketch, "E1661", {"start": v(-118.33, -19.93) * mm, "end": v(-118.27, -20.95) * mm});
            skLineSegment(sketch, "E1662", {"start": v(-118.27, -20.95) * mm, "end": v(-118.2, -21.97) * mm});
            skLineSegment(sketch, "E1663", {"start": v(-118.2, -21.97) * mm, "end": v(-118.12, -22.99) * mm});
            skLineSegment(sketch, "E1664", {"start": v(-118.12, -22.99) * mm, "end": v(-118.02, -24) * mm});
            skLineSegment(sketch, "E1665", {"start": v(-118.02, -24) * mm, "end": v(-117.9, -25.02) * mm});
            skLineSegment(sketch, "E1666", {"start": v(-117.9, -25.02) * mm, "end": v(-117.78, -26.03) * mm});
            skLineSegment(sketch, "E1667", {"start": v(-117.78, -26.03) * mm, "end": v(-117.64, -27.04) * mm});
            skLineSegment(sketch, "E1668", {"start": v(-117.64, -27.04) * mm, "end": v(-117.48, -28.04) * mm});
            skLineSegment(sketch, "E1669", {"start": v(-117.48, -28.04) * mm, "end": v(-117.3, -29.03) * mm});
            skLineSegment(sketch, "E1670", {"start": v(-117.3, -29.03) * mm, "end": v(-117.11, -30.02) * mm});
            skLineSegment(sketch, "E1671", {"start": v(-117.11, -30.02) * mm, "end": v(-116.9, -31) * mm});
            skLineSegment(sketch, "E1672", {"start": v(-116.9, -31) * mm, "end": v(-116.66, -31.98) * mm});
            skLineSegment(sketch, "E1673", {"start": v(-116.66, -31.98) * mm, "end": v(-116.4, -32.94) * mm});
            skLineSegment(sketch, "E1674", {"start": v(-116.4, -32.94) * mm, "end": v(-116.12, -33.9) * mm});
            skLineSegment(sketch, "E1675", {"start": v(-116.12, -33.9) * mm, "end": v(-115.81, -34.85) * mm});
            skLineSegment(sketch, "E1676", {"start": v(-115.81, -34.85) * mm, "end": v(-115.48, -35.78) * mm});
            skLineSegment(sketch, "E1677", {"start": v(-115.48, -35.78) * mm, "end": v(-115.13, -36.7) * mm});
            skLineSegment(sketch, "E1678", {"start": v(-115.13, -36.7) * mm, "end": v(-114.74, -37.62) * mm});
            skLineSegment(sketch, "E1679", {"start": v(-114.74, -37.62) * mm, "end": v(-114.33, -38.51) * mm});
            skLineSegment(sketch, "E1680", {"start": v(-114.33, -38.51) * mm, "end": v(-113.9, -39.4) * mm});
            skLineSegment(sketch, "E1681", {"start": v(-113.9, -39.4) * mm, "end": v(-113.42, -40.26) * mm});
            skLineSegment(sketch, "E1682", {"start": v(-113.42, -40.26) * mm, "end": v(-112.92, -41.12) * mm});
            skLineSegment(sketch, "E1683", {"start": v(-112.92, -41.12) * mm, "end": v(-112.4, -41.96) * mm});
            skLineSegment(sketch, "E1684", {"start": v(-112.4, -41.96) * mm, "end": v(-111.82, -42.8) * mm});
            skLineSegment(sketch, "E1685", {"start": v(-111.82, -42.8) * mm, "end": v(-111.22, -43.6) * mm});
            skLineSegment(sketch, "E1686", {"start": v(-111.22, -43.6) * mm, "end": v(-110.59, -44.38) * mm});
            skLineSegment(sketch, "E1687", {"start": v(-110.59, -44.38) * mm, "end": v(-109.94, -45.13) * mm});
            skLineSegment(sketch, "E1688", {"start": v(-109.94, -45.13) * mm, "end": v(-109.26, -45.86) * mm});
            skLineSegment(sketch, "E1689", {"start": v(-109.26, -45.86) * mm, "end": v(-108.56, -46.56) * mm});
            skLineSegment(sketch, "E1690", {"start": v(-108.56, -46.56) * mm, "end": v(-107.84, -47.23) * mm});
            skLineSegment(sketch, "E1691", {"start": v(-107.84, -47.23) * mm, "end": v(-107.1, -47.88) * mm});
            skLineSegment(sketch, "E1692", {"start": v(-107.1, -47.88) * mm, "end": v(-106.34, -48.5) * mm});
            skLineSegment(sketch, "E1693", {"start": v(-106.34, -48.5) * mm, "end": v(-105.56, -49.1) * mm});
            skLineSegment(sketch, "E1694", {"start": v(-105.56, -49.1) * mm, "end": v(-104.77, -49.68) * mm});
            skLineSegment(sketch, "E1695", {"start": v(-104.77, -49.68) * mm, "end": v(-103.95, -50.23) * mm});
            skLineSegment(sketch, "E1696", {"start": v(-103.95, -50.23) * mm, "end": v(-103.12, -50.76) * mm});
            skLineSegment(sketch, "E1697", {"start": v(-103.12, -50.76) * mm, "end": v(-102.27, -51.26) * mm});
            skLineSegment(sketch, "E1698", {"start": v(-102.27, -51.26) * mm, "end": v(-101.41, -51.75) * mm});
            skLineSegment(sketch, "E1699", {"start": v(-101.41, -51.75) * mm, "end": v(-100.54, -52.21) * mm});
            skLineSegment(sketch, "E1700", {"start": v(-100.54, -52.21) * mm, "end": v(-99.65, -52.66) * mm});
            skLineSegment(sketch, "E1701", {"start": v(-99.65, -52.66) * mm, "end": v(-98.75, -53.08) * mm});
            skLineSegment(sketch, "E1702", {"start": v(-98.75, -53.08) * mm, "end": v(-97.84, -53.48) * mm});
            skLineSegment(sketch, "E1703", {"start": v(-97.84, -53.48) * mm, "end": v(-96.92, -53.87) * mm});
            skLineSegment(sketch, "E1704", {"start": v(-96.92, -53.87) * mm, "end": v(-96, -54.23) * mm});
            skLineSegment(sketch, "E1705", {"start": v(-96, -54.23) * mm, "end": v(-95.06, -54.58) * mm});
            skLineSegment(sketch, "E1706", {"start": v(-95.06, -54.58) * mm, "end": v(-94.12, -54.9) * mm});
            skLineSegment(sketch, "E1707", {"start": v(-94.12, -54.9) * mm, "end": v(-93.17, -55.22) * mm});
            skLineSegment(sketch, "E1708", {"start": v(-93.17, -55.22) * mm, "end": v(-92.21, -55.52) * mm});
            skLineSegment(sketch, "E1709", {"start": v(-92.21, -55.52) * mm, "end": v(-91.25, -55.8) * mm});
            skLineSegment(sketch, "E1710", {"start": v(-91.25, -55.8) * mm, "end": v(-90.3, -56.06) * mm});
            skLineSegment(sketch, "E1711", {"start": v(-90.3, -56.06) * mm, "end": v(-89.33, -56.3) * mm});
            skLineSegment(sketch, "E1712", {"start": v(-89.33, -56.3) * mm, "end": v(-88.36, -56.54) * mm});
            skLineSegment(sketch, "E1713", {"start": v(-88.36, -56.54) * mm, "end": v(-87.4, -56.76) * mm});
            skLineSegment(sketch, "E1714", {"start": v(-87.4, -56.76) * mm, "end": v(-86.43, -56.97) * mm});
            skLineSegment(sketch, "E1715", {"start": v(-86.43, -56.97) * mm, "end": v(-85.46, -57.16) * mm});
            skLineSegment(sketch, "E1716", {"start": v(-85.46, -57.16) * mm, "end": v(-84.5, -57.34) * mm});
            skLineSegment(sketch, "E1717", {"start": v(-84.5, -57.34) * mm, "end": v(-83.52, -57.52) * mm});
            skLineSegment(sketch, "E1718", {"start": v(-83.52, -57.52) * mm, "end": v(-82.53, -57.69) * mm});
            skLineSegment(sketch, "E1719", {"start": v(-82.53, -57.69) * mm, "end": v(-81.55, -57.85) * mm});
            skLineSegment(sketch, "E1720", {"start": v(-81.55, -57.85) * mm, "end": v(-80.56, -58) * mm});
            skLineSegment(sketch, "E1721", {"start": v(-80.56, -58) * mm, "end": v(-79.57, -58.16) * mm});
            skLineSegment(sketch, "E1722", {"start": v(-79.57, -58.16) * mm, "end": v(-78.58, -58.3) * mm});
            skLineSegment(sketch, "E1723", {"start": v(-78.58, -58.3) * mm, "end": v(-77.59, -58.45) * mm});
            skLineSegment(sketch, "E1724", {"start": v(-77.59, -58.45) * mm, "end": v(-76.6, -58.58) * mm});
            skLineSegment(sketch, "E1725", {"start": v(-76.6, -58.58) * mm, "end": v(-75.6, -58.7) * mm});
            skLineSegment(sketch, "E1726", {"start": v(-75.6, -58.7) * mm, "end": v(-74.6, -58.83) * mm});
            skLineSegment(sketch, "E1727", {"start": v(-74.6, -58.83) * mm, "end": v(-73.6, -58.95) * mm});
            skLineSegment(sketch, "E1728", {"start": v(-73.6, -58.95) * mm, "end": v(-72.61, -59.06) * mm});
            skLineSegment(sketch, "E1729", {"start": v(-72.61, -59.06) * mm, "end": v(-71.61, -59.16) * mm});
            skLineSegment(sketch, "E1730", {"start": v(-71.61, -59.16) * mm, "end": v(-70.62, -59.26) * mm});
            skLineSegment(sketch, "E1731", {"start": v(-70.62, -59.26) * mm, "end": v(-69.62, -59.36) * mm});
            skLineSegment(sketch, "E1732", {"start": v(-69.62, -59.36) * mm, "end": v(-68.61, -59.45) * mm});
            skLineSegment(sketch, "E1733", {"start": v(-68.61, -59.45) * mm, "end": v(-67.61, -59.53) * mm});
            skLineSegment(sketch, "E1734", {"start": v(-67.61, -59.53) * mm, "end": v(-66.61, -59.6) * mm});
            skLineSegment(sketch, "E1735", {"start": v(-66.61, -59.6) * mm, "end": v(-65.6, -59.68) * mm});
            skLineSegment(sketch, "E1736", {"start": v(-65.6, -59.68) * mm, "end": v(-64.6, -59.75) * mm});
            skLineSegment(sketch, "E1737", {"start": v(-64.6, -59.75) * mm, "end": v(-63.6, -59.81) * mm});
            skLineSegment(sketch, "E1738", {"start": v(-63.6, -59.81) * mm, "end": v(-62.6, -59.87) * mm});
            skLineSegment(sketch, "E1739", {"start": v(-62.6, -59.87) * mm, "end": v(-61.59, -59.92) * mm});
            skLineSegment(sketch, "E1740", {"start": v(-61.59, -59.92) * mm, "end": v(-60.58, -59.96) * mm});
            skLineSegment(sketch, "E1741", {"start": v(-60.58, -59.96) * mm, "end": v(-59.58, -60) * mm});
            skLineSegment(sketch, "E1742", {"start": v(-59.58, -60) * mm, "end": v(-58.57, -60.04) * mm});
            skLineSegment(sketch, "E1743", {"start": v(-58.57, -60.04) * mm, "end": v(-57.56, -60.07) * mm});
            skLineSegment(sketch, "E1744", {"start": v(-57.56, -60.07) * mm, "end": v(-56.56, -60.1) * mm});
            skLineSegment(sketch, "E1745", {"start": v(-56.56, -60.1) * mm, "end": v(-55.55, -60.12) * mm});
            skLineSegment(sketch, "E1746", {"start": v(-55.55, -60.12) * mm, "end": v(-54.54, -60.13) * mm});
            skLineSegment(sketch, "E1747", {"start": v(-54.54, -60.13) * mm, "end": v(-53.53, -60.14) * mm});
            skLineSegment(sketch, "E1748", {"start": v(-53.53, -60.14) * mm, "end": v(-52.52, -60.14) * mm});
            skLineSegment(sketch, "E1749", {"start": v(-52.52, -60.14) * mm, "end": v(-51.52, -60.14) * mm});
            skLineSegment(sketch, "E1750", {"start": v(-51.52, -60.14) * mm, "end": v(-50.5, -60.14) * mm});
            skLineSegment(sketch, "E1751", {"start": v(-50.5, -60.14) * mm, "end": v(-49.5, -60.13) * mm});
            skLineSegment(sketch, "E1752", {"start": v(-49.5, -60.13) * mm, "end": v(-48.5, -60.11) * mm});
            skLineSegment(sketch, "E1753", {"start": v(-48.5, -60.11) * mm, "end": v(-47.49, -60.1) * mm});
            skLineSegment(sketch, "E1754", {"start": v(-47.49, -60.1) * mm, "end": v(-46.48, -60.07) * mm});
            skLineSegment(sketch, "E1755", {"start": v(-46.48, -60.07) * mm, "end": v(-45.47, -60.04) * mm});
            skLineSegment(sketch, "E1756", {"start": v(-45.47, -60.04) * mm, "end": v(-44.46, -60) * mm});
            skLineSegment(sketch, "E1757", {"start": v(-44.46, -60) * mm, "end": v(-43.46, -59.97) * mm});
            skLineSegment(sketch, "E1758", {"start": v(-43.46, -59.97) * mm, "end": v(-42.45, -59.92) * mm});
            skLineSegment(sketch, "E1759", {"start": v(-42.45, -59.92) * mm, "end": v(-41.44, -59.87) * mm});
            skLineSegment(sketch, "E1760", {"start": v(-41.44, -59.87) * mm, "end": v(-40.44, -59.82) * mm});
            skLineSegment(sketch, "E1761", {"start": v(-40.44, -59.82) * mm, "end": v(-39.43, -59.76) * mm});
            skLineSegment(sketch, "E1762", {"start": v(-39.43, -59.76) * mm, "end": v(-38.43, -59.7) * mm});
            skLineSegment(sketch, "E1763", {"start": v(-38.43, -59.7) * mm, "end": v(-37.43, -59.63) * mm});
            skLineSegment(sketch, "E1764", {"start": v(-37.43, -59.63) * mm, "end": v(-36.42, -59.56) * mm});
            skLineSegment(sketch, "E1765", {"start": v(-36.42, -59.56) * mm, "end": v(-35.42, -59.48) * mm});
            skLineSegment(sketch, "E1766", {"start": v(-35.42, -59.48) * mm, "end": v(-34.42, -59.4) * mm});
            skLineSegment(sketch, "E1767", {"start": v(-34.42, -59.4) * mm, "end": v(-33.42, -59.32) * mm});
            skLineSegment(sketch, "E1768", {"start": v(-33.42, -59.32) * mm, "end": v(-32.42, -59.23) * mm});
            skLineSegment(sketch, "E1769", {"start": v(-32.42, -59.23) * mm, "end": v(-31.42, -59.14) * mm});
            skLineSegment(sketch, "E1770", {"start": v(-31.42, -59.14) * mm, "end": v(-30.42, -59.04) * mm});
            skLineSegment(sketch, "E1771", {"start": v(-30.42, -59.04) * mm, "end": v(-29.42, -58.94) * mm});
            skLineSegment(sketch, "E1772", {"start": v(-29.42, -58.94) * mm, "end": v(-28.43, -58.83) * mm});
            skLineSegment(sketch, "E1773", {"start": v(-28.43, -58.83) * mm, "end": v(-27.43, -58.72) * mm});
            skLineSegment(sketch, "E1774", {"start": v(-27.43, -58.72) * mm, "end": v(-26.44, -58.6) * mm});
            skLineSegment(sketch, "E1775", {"start": v(-26.44, -58.6) * mm, "end": v(-25.45, -58.48) * mm});
            skLineSegment(sketch, "E1776", {"start": v(-25.45, -58.48) * mm, "end": v(-24.45, -58.36) * mm});
            skLineSegment(sketch, "E1777", {"start": v(-24.45, -58.36) * mm, "end": v(-23.46, -58.23) * mm});
            skLineSegment(sketch, "E1778", {"start": v(-23.46, -58.23) * mm, "end": v(-22.47, -58.1) * mm});
            skLineSegment(sketch, "E1779", {"start": v(-22.47, -58.1) * mm, "end": v(-21.49, -57.97) * mm});
            skLineSegment(sketch, "E1780", {"start": v(-21.49, -57.97) * mm, "end": v(-20.5, -57.83) * mm});
            skLineSegment(sketch, "E1781", {"start": v(-20.5, -57.83) * mm, "end": v(-19.53, -57.68) * mm});
            skLineSegment(sketch, "E1782", {"start": v(-19.53, -57.68) * mm, "end": v(-18.57, -57.52) * mm});
            skLineSegment(sketch, "E1783", {"start": v(-18.57, -57.52) * mm, "end": v(-17.6, -57.35) * mm});
            skLineSegment(sketch, "E1784", {"start": v(-17.6, -57.35) * mm, "end": v(-16.62, -57.16) * mm});
            skLineSegment(sketch, "E1785", {"start": v(-16.62, -57.16) * mm, "end": v(-15.65, -56.96) * mm});
            skLineSegment(sketch, "E1786", {"start": v(-15.65, -56.96) * mm, "end": v(-14.68, -56.74) * mm});
            skLineSegment(sketch, "E1787", {"start": v(-14.68, -56.74) * mm, "end": v(-13.71, -56.5) * mm});
            skLineSegment(sketch, "E1788", {"start": v(-13.71, -56.5) * mm, "end": v(-12.74, -56.25) * mm});
            skLineSegment(sketch, "E1789", {"start": v(-12.74, -56.25) * mm, "end": v(-11.78, -55.98) * mm});
            skLineSegment(sketch, "E1790", {"start": v(-11.78, -55.98) * mm, "end": v(-10.82, -55.7) * mm});
            skLineSegment(sketch, "E1791", {"start": v(-10.82, -55.7) * mm, "end": v(-9.87, -55.39) * mm});
            skLineSegment(sketch, "E1792", {"start": v(-9.87, -55.39) * mm, "end": v(-8.93, -55.06) * mm});
            skLineSegment(sketch, "E1793", {"start": v(-8.93, -55.06) * mm, "end": v(-8, -54.72) * mm});
            skLineSegment(sketch, "E1794", {"start": v(-8, -54.72) * mm, "end": v(-7.06, -54.35) * mm});
            skLineSegment(sketch, "E1795", {"start": v(-7.06, -54.35) * mm, "end": v(-6.14, -53.97) * mm});
            skLineSegment(sketch, "E1796", {"start": v(-6.14, -53.97) * mm, "end": v(-5.24, -53.56) * mm});
            skLineSegment(sketch, "E1797", {"start": v(-5.24, -53.56) * mm, "end": v(-4.34, -53.14) * mm});
            skLineSegment(sketch, "E1798", {"start": v(-4.34, -53.14) * mm, "end": v(-3.46, -52.69) * mm});
            skLineSegment(sketch, "E1799", {"start": v(-3.46, -52.69) * mm, "end": v(-2.6, -52.22) * mm});
            skLineSegment(sketch, "E1800", {"start": v(-2.6, -52.22) * mm, "end": v(-1.74, -51.72) * mm});
            skLineSegment(sketch, "E1801", {"start": v(-1.74, -51.72) * mm, "end": v(-0.9, -51.2) * mm});
            skLineSegment(sketch, "E1802", {"start": v(-0.9, -51.2) * mm, "end": v(-0.08, -50.66) * mm});
            skLineSegment(sketch, "E1803", {"start": v(-0.08, -50.66) * mm, "end": v(0.72, -50.1) * mm});
            skLineSegment(sketch, "E1804", {"start": v(0.72, -50.1) * mm, "end": v(1.5, -49.5) * mm});
            skLineSegment(sketch, "E1805", {"start": v(1.5, -49.5) * mm, "end": v(2.27, -48.88) * mm});
            skLineSegment(sketch, "E1806", {"start": v(2.27, -48.88) * mm, "end": v(3, -48.24) * mm});
            skLineSegment(sketch, "E1807", {"start": v(3, -48.24) * mm, "end": v(3.73, -47.57) * mm});
            skLineSegment(sketch, "E1808", {"start": v(3.73, -47.57) * mm, "end": v(4.43, -46.87) * mm});
            skLineSegment(sketch, "E1809", {"start": v(4.43, -46.87) * mm, "end": v(5.1, -46.15) * mm});
            skLineSegment(sketch, "E1810", {"start": v(5.1, -46.15) * mm, "end": v(5.75, -45.4) * mm});
            skLineSegment(sketch, "E1811", {"start": v(5.75, -45.4) * mm, "end": v(6.37, -44.6) * mm});
            skLineSegment(sketch, "E1812", {"start": v(6.37, -44.6) * mm, "end": v(6.96, -43.8) * mm});
            skLineSegment(sketch, "E1813", {"start": v(6.96, -43.8) * mm, "end": v(7.53, -42.96) * mm});
            skLineSegment(sketch, "E1814", {"start": v(7.53, -42.96) * mm, "end": v(8.07, -42.1) * mm});
            skLineSegment(sketch, "E1815", {"start": v(8.07, -42.1) * mm, "end": v(8.56, -41.21) * mm});
            skLineSegment(sketch, "E1816", {"start": v(8.56, -41.21) * mm, "end": v(9.02, -40.32) * mm});
            skLineSegment(sketch, "E1817", {"start": v(9.02, -40.32) * mm, "end": v(9.45, -39.42) * mm});
            skLineSegment(sketch, "E1818", {"start": v(9.45, -39.42) * mm, "end": v(9.84, -38.5) * mm});
            skLineSegment(sketch, "E1819", {"start": v(9.84, -38.5) * mm, "end": v(10.2, -37.59) * mm});
            skLineSegment(sketch, "E1820", {"start": v(10.2, -37.59) * mm, "end": v(10.52, -36.66) * mm});
            skLineSegment(sketch, "E1821", {"start": v(10.52, -36.66) * mm, "end": v(10.82, -35.72) * mm});
            skLineSegment(sketch, "E1822", {"start": v(10.82, -35.72) * mm, "end": v(11.09, -34.77) * mm});
            skLineSegment(sketch, "E1823", {"start": v(11.09, -34.77) * mm, "end": v(11.33, -33.8) * mm});
            skLineSegment(sketch, "E1824", {"start": v(11.33, -33.8) * mm, "end": v(11.54, -32.84) * mm});
            skLineSegment(sketch, "E1825", {"start": v(11.54, -32.84) * mm, "end": v(11.74, -31.87) * mm});
            skLineSegment(sketch, "E1826", {"start": v(11.74, -31.87) * mm, "end": v(11.9, -30.9) * mm});
            skLineSegment(sketch, "E1827", {"start": v(11.9, -30.9) * mm, "end": v(12.05, -29.91) * mm});
            skLineSegment(sketch, "E1828", {"start": v(12.05, -29.91) * mm, "end": v(12.17, -28.93) * mm});
            skLineSegment(sketch, "E1829", {"start": v(12.17, -28.93) * mm, "end": v(12.28, -27.93) * mm});
            skLineSegment(sketch, "E1830", {"start": v(12.28, -27.93) * mm, "end": v(12.37, -26.94) * mm});
            skLineSegment(sketch, "E1831", {"start": v(12.37, -26.94) * mm, "end": v(12.44, -25.94) * mm});
            skLineSegment(sketch, "E1832", {"start": v(12.44, -25.94) * mm, "end": v(12.5, -24.94) * mm});
            skLineSegment(sketch, "E1833", {"start": v(12.5, -24.94) * mm, "end": v(12.55, -23.93) * mm});
            skLineSegment(sketch, "E1834", {"start": v(12.55, -23.93) * mm, "end": v(12.58, -22.93) * mm});
            skLineSegment(sketch, "E1835", {"start": v(12.58, -22.93) * mm, "end": v(12.6, -21.92) * mm});
            skLineSegment(sketch, "E1836", {"start": v(12.6, -21.92) * mm, "end": v(12.61, -20.91) * mm});
            skLineSegment(sketch, "E1837", {"start": v(12.61, -20.91) * mm, "end": v(12.61, -19.9) * mm});
            skLineSegment(sketch, "E1838", {"start": v(12.61, -19.9) * mm, "end": v(12.61, -18.9) * mm});
            skLineSegment(sketch, "E1839", {"start": v(12.61, -18.9) * mm, "end": v(12.6, -17.9) * mm});
            skLineSegment(sketch, "E1840", {"start": v(12.6, -17.9) * mm, "end": v(12.59, -16.89) * mm});
            skLineSegment(sketch, "E1841", {"start": v(12.59, -16.89) * mm, "end": v(12.57, -15.89) * mm});
            skLineSegment(sketch, "E1842", {"start": v(12.57, -15.89) * mm, "end": v(12.56, -14.89) * mm});
            skLineSegment(sketch, "E1843", {"start": v(12.56, -14.89) * mm, "end": v(12.54, -13.9) * mm});
            skLineSegment(sketch, "E1844", {"start": v(12.54, -13.9) * mm, "end": v(12.52, -12.9) * mm});
            skLineSegment(sketch, "E1845", {"start": v(12.52, -12.9) * mm, "end": v(12.51, -11.91) * mm});
            skLineSegment(sketch, "E1846", {"start": v(12.51, -11.91) * mm, "end": v(12.5, -10.93) * mm});
            skLineSegment(sketch, "E1847", {"start": v(12.5, -10.93) * mm, "end": v(12.5, -9.96) * mm});
            skLineSegment(sketch, "E1848", {"start": v(12.5, -9.96) * mm, "end": v(12.5, 53.04) * mm});
            skLineSegment(sketch, "E1849", {"start": v(12.5, 53.04) * mm, "end": v(-27.5, 53.04) * mm});
            skLineSegment(sketch, "E1850", {"start": v(-27.5, 53.04) * mm, "end": v(-27.5, 5.04) * mm});
            skLineSegment(sketch, "E1851", {"start": v(-27.5, 5.04) * mm, "end": v(-27.5, 4.08) * mm});
            skLineSegment(sketch, "E1852", {"start": v(-27.5, 4.08) * mm, "end": v(-27.48, 3.1) * mm});
            skLineSegment(sketch, "E1853", {"start": v(-27.48, 3.1) * mm, "end": v(-27.46, 2.12) * mm});
            skLineSegment(sketch, "E1854", {"start": v(-27.46, 2.12) * mm, "end": v(-27.44, 1.12) * mm});
            skLineSegment(sketch, "E1855", {"start": v(-27.44, 1.12) * mm, "end": v(-27.42, 0.1) * mm});
            skLineSegment(sketch, "E1856", {"start": v(-27.42, 0.1) * mm, "end": v(-27.4, -0.91) * mm});
            skLineSegment(sketch, "E1857", {"start": v(-27.4, -0.91) * mm, "end": v(-27.37, -1.94) * mm});
            skLineSegment(sketch, "E1858", {"start": v(-27.37, -1.94) * mm, "end": v(-27.35, -2.97) * mm});
            skLineSegment(sketch, "E1859", {"start": v(-27.35, -2.97) * mm, "end": v(-27.34, -4) * mm});
            skLineSegment(sketch, "E1860", {"start": v(-27.34, -4) * mm, "end": v(-27.34, -5.05) * mm});
            skLineSegment(sketch, "E1861", {"start": v(-27.34, -5.05) * mm, "end": v(-27.34, -6.09) * mm});
            skLineSegment(sketch, "E1862", {"start": v(-27.34, -6.09) * mm, "end": v(-27.36, -7.13) * mm});
            skLineSegment(sketch, "E1863", {"start": v(-27.36, -7.13) * mm, "end": v(-27.4, -8.17) * mm});
            skLineSegment(sketch, "E1864", {"start": v(-27.4, -8.17) * mm, "end": v(-27.45, -9.2) * mm});
            skLineSegment(sketch, "E1865", {"start": v(-27.45, -9.2) * mm, "end": v(-27.52, -10.24) * mm});
            skLineSegment(sketch, "E1866", {"start": v(-27.52, -10.24) * mm, "end": v(-27.6, -11.27) * mm});
            skLineSegment(sketch, "E1867", {"start": v(-27.6, -11.27) * mm, "end": v(-27.72, -12.3) * mm});
            skLineSegment(sketch, "E1868", {"start": v(-27.72, -12.3) * mm, "end": v(-27.85, -13.3) * mm});
            skLineSegment(sketch, "E1869", {"start": v(-27.85, -13.3) * mm, "end": v(-28.02, -14.31) * mm});
            skLineSegment(sketch, "E1870", {"start": v(-28.02, -14.31) * mm, "end": v(-28.2, -15.3) * mm});
            skLineSegment(sketch, "E1871", {"start": v(-28.2, -15.3) * mm, "end": v(-28.43, -16.28) * mm});
            skLineSegment(sketch, "E1872", {"start": v(-28.43, -16.28) * mm, "end": v(-28.68, -17.25) * mm});
            skLineSegment(sketch, "E1873", {"start": v(-28.68, -17.25) * mm, "end": v(-28.97, -18.2) * mm});
            skLineSegment(sketch, "E1874", {"start": v(-28.97, -18.2) * mm, "end": v(-29.3, -19.14) * mm});
            skLineSegment(sketch, "E1875", {"start": v(-29.3, -19.14) * mm, "end": v(-29.67, -20.06) * mm});
            skLineSegment(sketch, "E1876", {"start": v(-29.67, -20.06) * mm, "end": v(-30.07, -20.96) * mm});
            skLineSegment(sketch, "E1877", {"start": v(-30.07, -20.96) * mm, "end": v(-30.44, -21.66) * mm});
            skLineSegment(sketch, "E1878", {"start": v(-30.44, -21.66) * mm, "end": v(-30.83, -22.35) * mm});
            skLineSegment(sketch, "E1879", {"start": v(-30.83, -22.35) * mm, "end": v(-31.27, -23) * mm});
            skLineSegment(sketch, "E1880", {"start": v(-31.27, -23) * mm, "end": v(-31.74, -23.65) * mm});
            skLineSegment(sketch, "E1881", {"start": v(-31.74, -23.65) * mm, "end": v(-32.23, -24.27) * mm});
            skLineSegment(sketch, "E1882", {"start": v(-32.23, -24.27) * mm, "end": v(-32.76, -24.86) * mm});
            skLineSegment(sketch, "E1883", {"start": v(-32.76, -24.86) * mm, "end": v(-33.32, -25.44) * mm});
            skLineSegment(sketch, "E1884", {"start": v(-33.32, -25.44) * mm, "end": v(-33.91, -26) * mm});
            skLineSegment(sketch, "E1885", {"start": v(-33.91, -26) * mm, "end": v(-34.53, -26.52) * mm});
            skLineSegment(sketch, "E1886", {"start": v(-34.53, -26.52) * mm, "end": v(-35.17, -27.03) * mm});
            skLineSegment(sketch, "E1887", {"start": v(-35.17, -27.03) * mm, "end": v(-35.84, -27.51) * mm});
            skLineSegment(sketch, "E1888", {"start": v(-35.84, -27.51) * mm, "end": v(-36.53, -27.98) * mm});
            skLineSegment(sketch, "E1889", {"start": v(-36.53, -27.98) * mm, "end": v(-37.24, -28.42) * mm});
            skLineSegment(sketch, "E1890", {"start": v(-37.24, -28.42) * mm, "end": v(-37.98, -28.84) * mm});
            skLineSegment(sketch, "E1891", {"start": v(-37.98, -28.84) * mm, "end": v(-38.73, -29.23) * mm});
            skLineSegment(sketch, "E1892", {"start": v(-38.73, -29.23) * mm, "end": v(-39.5, -29.6) * mm});
            skLineSegment(sketch, "E1893", {"start": v(-39.5, -29.6) * mm, "end": v(-40.3, -29.96) * mm});
            skLineSegment(sketch, "E1894", {"start": v(-40.3, -29.96) * mm, "end": v(-41.1, -30.29) * mm});
            skLineSegment(sketch, "E1895", {"start": v(-41.1, -30.29) * mm, "end": v(-41.93, -30.6) * mm});
            skLineSegment(sketch, "E1896", {"start": v(-41.93, -30.6) * mm, "end": v(-42.77, -30.87) * mm});
            skLineSegment(sketch, "E1897", {"start": v(-42.77, -30.87) * mm, "end": v(-43.62, -31.13) * mm});
            skLineSegment(sketch, "E1898", {"start": v(-43.62, -31.13) * mm, "end": v(-44.48, -31.37) * mm});
            skLineSegment(sketch, "E1899", {"start": v(-44.48, -31.37) * mm, "end": v(-45.35, -31.59) * mm});
            skLineSegment(sketch, "E1900", {"start": v(-45.35, -31.59) * mm, "end": v(-46.24, -31.78) * mm});
            skLineSegment(sketch, "E1901", {"start": v(-46.24, -31.78) * mm, "end": v(-47.13, -31.95) * mm});
            skLineSegment(sketch, "E1902", {"start": v(-47.13, -31.95) * mm, "end": v(-48.03, -32.1) * mm});
            skLineSegment(sketch, "E1903", {"start": v(-48.03, -32.1) * mm, "end": v(-48.93, -32.21) * mm});
            skLineSegment(sketch, "E1904", {"start": v(-48.93, -32.21) * mm, "end": v(-49.84, -32.31) * mm});
            skLineSegment(sketch, "E1905", {"start": v(-49.84, -32.31) * mm, "end": v(-50.75, -32.39) * mm});
            skLineSegment(sketch, "E1906", {"start": v(-50.75, -32.39) * mm, "end": v(-51.67, -32.44) * mm});
            skLineSegment(sketch, "E1907", {"start": v(-51.67, -32.44) * mm, "end": v(-52.58, -32.47) * mm});
            skLineSegment(sketch, "E1908", {"start": v(-52.58, -32.47) * mm, "end": v(-53.5, -32.47) * mm});
            skLineSegment(sketch, "E1909", {"start": v(-53.5, -32.47) * mm, "end": v(-54.42, -32.46) * mm});
            skLineSegment(sketch, "E1910", {"start": v(-54.42, -32.46) * mm, "end": v(-55.33, -32.42) * mm});
            skLineSegment(sketch, "E1911", {"start": v(-55.33, -32.42) * mm, "end": v(-56.24, -32.35) * mm});
            skLineSegment(sketch, "E1912", {"start": v(-56.24, -32.35) * mm, "end": v(-57.14, -32.26) * mm});
            skLineSegment(sketch, "E1913", {"start": v(-57.14, -32.26) * mm, "end": v(-58.04, -32.15) * mm});
            skLineSegment(sketch, "E1914", {"start": v(-58.04, -32.15) * mm, "end": v(-58.93, -32.02) * mm});
            skLineSegment(sketch, "E1915", {"start": v(-58.93, -32.02) * mm, "end": v(-59.81, -31.86) * mm});
            skLineSegment(sketch, "E1916", {"start": v(-59.81, -31.86) * mm, "end": v(-60.68, -31.67) * mm});
            skLineSegment(sketch, "E1917", {"start": v(-60.68, -31.67) * mm, "end": v(-61.54, -31.47) * mm});
            skLineSegment(sketch, "E1918", {"start": v(-61.54, -31.47) * mm, "end": v(-62.4, -31.24) * mm});
            skLineSegment(sketch, "E1919", {"start": v(-62.4, -31.24) * mm, "end": v(-63.23, -30.98) * mm});
            skLineSegment(sketch, "E1920", {"start": v(-63.23, -30.98) * mm, "end": v(-64.05, -30.7) * mm});
            skLineSegment(sketch, "E1921", {"start": v(-64.05, -30.7) * mm, "end": v(-64.86, -30.4) * mm});
            skLineSegment(sketch, "E1922", {"start": v(-64.86, -30.4) * mm, "end": v(-65.65, -30.07) * mm});
            skLineSegment(sketch, "E1923", {"start": v(-65.65, -30.07) * mm, "end": v(-66.42, -29.72) * mm});
            skLineSegment(sketch, "E1924", {"start": v(-66.42, -29.72) * mm, "end": v(-67.17, -29.35) * mm});
            skLineSegment(sketch, "E1925", {"start": v(-67.17, -29.35) * mm, "end": v(-67.9, -28.95) * mm});
            skLineSegment(sketch, "E1926", {"start": v(-67.9, -28.95) * mm, "end": v(-68.62, -28.52) * mm});
            skLineSegment(sketch, "E1927", {"start": v(-68.62, -28.52) * mm, "end": v(-69.3, -28.08) * mm});
            skLineSegment(sketch, "E1928", {"start": v(-69.3, -28.08) * mm, "end": v(-69.97, -27.6) * mm});
            skLineSegment(sketch, "E1929", {"start": v(-69.97, -27.6) * mm, "end": v(-70.6, -27.1) * mm});
            skLineSegment(sketch, "E1930", {"start": v(-70.6, -27.1) * mm, "end": v(-71.22, -26.59) * mm});
            skLineSegment(sketch, "E1931", {"start": v(-71.22, -26.59) * mm, "end": v(-71.8, -26.04) * mm});
            skLineSegment(sketch, "E1932", {"start": v(-71.8, -26.04) * mm, "end": v(-72.36, -25.47) * mm});
            skLineSegment(sketch, "E1933", {"start": v(-72.36, -25.47) * mm, "end": v(-72.89, -24.87) * mm});
            skLineSegment(sketch, "E1934", {"start": v(-72.89, -24.87) * mm, "end": v(-73.38, -24.25) * mm});
            skLineSegment(sketch, "E1935", {"start": v(-73.38, -24.25) * mm, "end": v(-73.84, -23.61) * mm});
            skLineSegment(sketch, "E1936", {"start": v(-73.84, -23.61) * mm, "end": v(-74.27, -22.94) * mm});
            skLineSegment(sketch, "E1937", {"start": v(-74.27, -22.94) * mm, "end": v(-74.76, -22.09) * mm});
            skLineSegment(sketch, "E1938", {"start": v(-74.76, -22.09) * mm, "end": v(-75.2, -21.21) * mm});
            skLineSegment(sketch, "E1939", {"start": v(-75.2, -21.21) * mm, "end": v(-75.6, -20.33) * mm});
            skLineSegment(sketch, "E1940", {"start": v(-75.6, -20.33) * mm, "end": v(-75.94, -19.42) * mm});
            skLineSegment(sketch, "E1941", {"start": v(-75.94, -19.42) * mm, "end": v(-76.25, -18.5) * mm});
            skLineSegment(sketch, "E1942", {"start": v(-76.25, -18.5) * mm, "end": v(-76.52, -17.57) * mm});
            skLineSegment(sketch, "E1943", {"start": v(-76.52, -17.57) * mm, "end": v(-76.76, -16.62) * mm});
            skLineSegment(sketch, "E1944", {"start": v(-76.76, -16.62) * mm, "end": v(-76.96, -15.67) * mm});
            skLineSegment(sketch, "E1945", {"start": v(-76.96, -15.67) * mm, "end": v(-77.13, -14.7) * mm});
            skLineSegment(sketch, "E1946", {"start": v(-77.13, -14.7) * mm, "end": v(-77.27, -13.73) * mm});
            skLineSegment(sketch, "E1947", {"start": v(-77.27, -13.73) * mm, "end": v(-77.39, -12.74) * mm});
            skLineSegment(sketch, "E1948", {"start": v(-77.39, -12.74) * mm, "end": v(-77.48, -11.76) * mm});
            skLineSegment(sketch, "E1949", {"start": v(-77.48, -11.76) * mm, "end": v(-77.55, -10.76) * mm});
            skLineSegment(sketch, "E1950", {"start": v(-77.55, -10.76) * mm, "end": v(-77.6, -9.77) * mm});
            skLineSegment(sketch, "E1951", {"start": v(-77.6, -9.77) * mm, "end": v(-77.63, -8.77) * mm});
            skLineSegment(sketch, "E1952", {"start": v(-77.63, -8.77) * mm, "end": v(-77.64, -7.77) * mm});
            skLineSegment(sketch, "E1953", {"start": v(-77.64, -7.77) * mm, "end": v(-77.65, -6.77) * mm});
            skLineSegment(sketch, "E1954", {"start": v(-77.65, -6.77) * mm, "end": v(-77.64, -5.77) * mm});
            skLineSegment(sketch, "E1955", {"start": v(-77.64, -5.77) * mm, "end": v(-77.63, -4.77) * mm});
            skLineSegment(sketch, "E1956", {"start": v(-77.63, -4.77) * mm, "end": v(-77.6, -3.78) * mm});
            skLineSegment(sketch, "E1957", {"start": v(-77.6, -3.78) * mm, "end": v(-77.58, -2.79) * mm});
            skLineSegment(sketch, "E1958", {"start": v(-77.58, -2.79) * mm, "end": v(-77.56, -1.8) * mm});
            skLineSegment(sketch, "E1959", {"start": v(-77.56, -1.8) * mm, "end": v(-77.54, -0.83) * mm});
            skLineSegment(sketch, "E1960", {"start": v(-77.54, -0.83) * mm, "end": v(-77.52, 0.14) * mm});
            skLineSegment(sketch, "E1961", {"start": v(-77.52, 0.14) * mm, "end": v(-77.5, 1.1) * mm});
            skLineSegment(sketch, "E1962", {"start": v(-77.5, 1.1) * mm, "end": v(-77.5, 2.04) * mm});
            skLineSegment(sketch, "E1963", {"start": v(-77.5, 2.04) * mm, "end": v(-77.5, 53.04) * mm});
            skLineSegment(sketch, "E1964", {"start": v(-77.5, 53.04) * mm, "end": v(-118.5, 53.04) * mm});
            skLineSegment(sketch, "E1965", {"start": v(20.5, 53.04) * mm, "end": v(20.5, 27.04) * mm});
            skLineSegment(sketch, "E1966", {"start": v(20.5, 27.04) * mm, "end": v(84.5, 27.04) * mm});
            skLineSegment(sketch, "E1967", {"start": v(84.5, 27.04) * mm, "end": v(83.79, 26.33) * mm});
            skLineSegment(sketch, "E1968", {"start": v(83.79, 26.33) * mm, "end": v(83.07, 25.62) * mm});
            skLineSegment(sketch, "E1969", {"start": v(83.07, 25.62) * mm, "end": v(82.35, 24.92) * mm});
            skLineSegment(sketch, "E1970", {"start": v(82.35, 24.92) * mm, "end": v(81.63, 24.2) * mm});
            skLineSegment(sketch, "E1971", {"start": v(81.63, 24.2) * mm, "end": v(80.91, 23.5) * mm});
            skLineSegment(sketch, "E1972", {"start": v(80.91, 23.5) * mm, "end": v(80.2, 22.8) * mm});
            skLineSegment(sketch, "E1973", {"start": v(80.2, 22.8) * mm, "end": v(79.47, 22.1) * mm});
            skLineSegment(sketch, "E1974", {"start": v(79.47, 22.1) * mm, "end": v(78.74, 21.4) * mm});
            skLineSegment(sketch, "E1975", {"start": v(78.74, 21.4) * mm, "end": v(78.02, 20.7) * mm});
            skLineSegment(sketch, "E1976", {"start": v(78.02, 20.7) * mm, "end": v(77.29, 20) * mm});
            skLineSegment(sketch, "E1977", {"start": v(77.29, 20) * mm, "end": v(76.56, 19.3) * mm});
            skLineSegment(sketch, "E1978", {"start": v(76.56, 19.3) * mm, "end": v(75.83, 18.6) * mm});
            skLineSegment(sketch, "E1979", {"start": v(75.83, 18.6) * mm, "end": v(75.1, 17.9) * mm});
            skLineSegment(sketch, "E1980", {"start": v(75.1, 17.9) * mm, "end": v(74.36, 17.2) * mm});
            skLineSegment(sketch, "E1981", {"start": v(74.36, 17.2) * mm, "end": v(73.63, 16.51) * mm});
            skLineSegment(sketch, "E1982", {"start": v(73.63, 16.51) * mm, "end": v(72.9, 15.82) * mm});
            skLineSegment(sketch, "E1983", {"start": v(72.9, 15.82) * mm, "end": v(72.16, 15.12) * mm});
            skLineSegment(sketch, "E1984", {"start": v(72.16, 15.12) * mm, "end": v(71.42, 14.43) * mm});
            skLineSegment(sketch, "E1985", {"start": v(71.42, 14.43) * mm, "end": v(70.68, 13.74) * mm});
            skLineSegment(sketch, "E1986", {"start": v(70.68, 13.74) * mm, "end": v(69.94, 13.05) * mm});
            skLineSegment(sketch, "E1987", {"start": v(69.94, 13.05) * mm, "end": v(69.2, 12.36) * mm});
            skLineSegment(sketch, "E1988", {"start": v(69.2, 12.36) * mm, "end": v(68.46, 11.67) * mm});
            skLineSegment(sketch, "E1989", {"start": v(68.46, 11.67) * mm, "end": v(67.72, 10.98) * mm});
            skLineSegment(sketch, "E1990", {"start": v(67.72, 10.98) * mm, "end": v(66.97, 10.3) * mm});
            skLineSegment(sketch, "E1991", {"start": v(66.97, 10.3) * mm, "end": v(66.23, 9.61) * mm});
            skLineSegment(sketch, "E1992", {"start": v(66.23, 9.61) * mm, "end": v(65.48, 8.93) * mm});
            skLineSegment(sketch, "E1993", {"start": v(65.48, 8.93) * mm, "end": v(64.74, 8.24) * mm});
            skLineSegment(sketch, "E1994", {"start": v(64.74, 8.24) * mm, "end": v(64, 7.56) * mm});
            skLineSegment(sketch, "E1995", {"start": v(64, 7.56) * mm, "end": v(63.24, 6.87) * mm});
            skLineSegment(sketch, "E1996", {"start": v(63.24, 6.87) * mm, "end": v(62.5, 6.19) * mm});
            skLineSegment(sketch, "E1997", {"start": v(62.5, 6.19) * mm, "end": v(61.75, 5.5) * mm});
            skLineSegment(sketch, "E1998", {"start": v(61.75, 5.5) * mm, "end": v(61, 4.82) * mm});
            skLineSegment(sketch, "E1999", {"start": v(61, 4.82) * mm, "end": v(60.25, 4.14) * mm});
            skLineSegment(sketch, "E2000", {"start": v(60.25, 4.14) * mm, "end": v(59.5, 3.46) * mm});
            skLineSegment(sketch, "E2001", {"start": v(59.5, 3.46) * mm, "end": v(58.75, 2.78) * mm});
            skLineSegment(sketch, "E2002", {"start": v(58.75, 2.78) * mm, "end": v(58, 2.1) * mm});
            skLineSegment(sketch, "E2003", {"start": v(58, 2.1) * mm, "end": v(57.25, 1.42) * mm});
            skLineSegment(sketch, "E2004", {"start": v(57.25, 1.42) * mm, "end": v(56.5, 0.74) * mm});
            skLineSegment(sketch, "E2005", {"start": v(56.5, 0.74) * mm, "end": v(55.75, 0.06) * mm});
            skLineSegment(sketch, "E2006", {"start": v(55.75, 0.06) * mm, "end": v(55, -0.61) * mm});
            skLineSegment(sketch, "E2007", {"start": v(55, -0.61) * mm, "end": v(54.25, -1.3) * mm});
            skLineSegment(sketch, "E2008", {"start": v(54.25, -1.3) * mm, "end": v(53.5, -1.97) * mm});
            skLineSegment(sketch, "E2009", {"start": v(53.5, -1.97) * mm, "end": v(52.75, -2.65) * mm});
            skLineSegment(sketch, "E2010", {"start": v(52.75, -2.65) * mm, "end": v(52, -3.32) * mm});
            skLineSegment(sketch, "E2011", {"start": v(52, -3.32) * mm, "end": v(51.24, -4) * mm});
            skLineSegment(sketch, "E2012", {"start": v(51.24, -4) * mm, "end": v(50.5, -4.68) * mm});
            skLineSegment(sketch, "E2013", {"start": v(50.5, -4.68) * mm, "end": v(49.74, -5.35) * mm});
            skLineSegment(sketch, "E2014", {"start": v(49.74, -5.35) * mm, "end": v(49, -6.03) * mm});
            skLineSegment(sketch, "E2015", {"start": v(49, -6.03) * mm, "end": v(48.24, -6.7) * mm});
            skLineSegment(sketch, "E2016", {"start": v(48.24, -6.7) * mm, "end": v(47.49, -7.38) * mm});
            skLineSegment(sketch, "E2017", {"start": v(47.49, -7.38) * mm, "end": v(46.74, -8.06) * mm});
            skLineSegment(sketch, "E2018", {"start": v(46.74, -8.06) * mm, "end": v(45.99, -8.73) * mm});
            skLineSegment(sketch, "E2019", {"start": v(45.99, -8.73) * mm, "end": v(45.24, -9.4) * mm});
            skLineSegment(sketch, "E2020", {"start": v(45.24, -9.4) * mm, "end": v(44.5, -10.08) * mm});
            skLineSegment(sketch, "E2021", {"start": v(44.5, -10.08) * mm, "end": v(43.74, -10.76) * mm});
            skLineSegment(sketch, "E2022", {"start": v(43.74, -10.76) * mm, "end": v(43, -11.44) * mm});
            skLineSegment(sketch, "E2023", {"start": v(43, -11.44) * mm, "end": v(42.25, -12.11) * mm});
            skLineSegment(sketch, "E2024", {"start": v(42.25, -12.11) * mm, "end": v(41.5, -12.79) * mm});
            skLineSegment(sketch, "E2025", {"start": v(41.5, -12.79) * mm, "end": v(40.83, -13.38) * mm});
            skLineSegment(sketch, "E2026", {"start": v(40.83, -13.38) * mm, "end": v(40.14, -13.98) * mm});
            skLineSegment(sketch, "E2027", {"start": v(40.14, -13.98) * mm, "end": v(39.42, -14.58) * mm});
            skLineSegment(sketch, "E2028", {"start": v(39.42, -14.58) * mm, "end": v(38.68, -15.2) * mm});
            skLineSegment(sketch, "E2029", {"start": v(38.68, -15.2) * mm, "end": v(37.92, -15.8) * mm});
            skLineSegment(sketch, "E2030", {"start": v(37.92, -15.8) * mm, "end": v(37.14, -16.43) * mm});
            skLineSegment(sketch, "E2031", {"start": v(37.14, -16.43) * mm, "end": v(36.34, -17.06) * mm});
            skLineSegment(sketch, "E2032", {"start": v(36.34, -17.06) * mm, "end": v(35.54, -17.7) * mm});
            skLineSegment(sketch, "E2033", {"start": v(35.54, -17.7) * mm, "end": v(34.73, -18.34) * mm});
            skLineSegment(sketch, "E2034", {"start": v(34.73, -18.34) * mm, "end": v(33.9, -19) * mm});
            skLineSegment(sketch, "E2035", {"start": v(33.9, -19) * mm, "end": v(33.09, -19.65) * mm});
            skLineSegment(sketch, "E2036", {"start": v(33.09, -19.65) * mm, "end": v(32.27, -20.32) * mm});
            skLineSegment(sketch, "E2037", {"start": v(32.27, -20.32) * mm, "end": v(31.45, -21) * mm});
            skLineSegment(sketch, "E2038", {"start": v(31.45, -21) * mm, "end": v(30.64, -21.67) * mm});
            skLineSegment(sketch, "E2039", {"start": v(30.64, -21.67) * mm, "end": v(29.83, -22.36) * mm});
            skLineSegment(sketch, "E2040", {"start": v(29.83, -22.36) * mm, "end": v(29.04, -23.05) * mm});
            skLineSegment(sketch, "E2041", {"start": v(29.04, -23.05) * mm, "end": v(28.27, -23.75) * mm});
            skLineSegment(sketch, "E2042", {"start": v(28.27, -23.75) * mm, "end": v(27.5, -24.46) * mm});
            skLineSegment(sketch, "E2043", {"start": v(27.5, -24.46) * mm, "end": v(26.77, -25.18) * mm});
            skLineSegment(sketch, "E2044", {"start": v(26.77, -25.18) * mm, "end": v(26.05, -25.9) * mm});
            skLineSegment(sketch, "E2045", {"start": v(26.05, -25.9) * mm, "end": v(25.37, -26.63) * mm});
            skLineSegment(sketch, "E2046", {"start": v(25.37, -26.63) * mm, "end": v(24.7, -27.37) * mm});
            skLineSegment(sketch, "E2047", {"start": v(24.7, -27.37) * mm, "end": v(24.08, -28.11) * mm});
            skLineSegment(sketch, "E2048", {"start": v(24.08, -28.11) * mm, "end": v(23.49, -28.87) * mm});
            skLineSegment(sketch, "E2049", {"start": v(23.49, -28.87) * mm, "end": v(22.93, -29.63) * mm});
            skLineSegment(sketch, "E2050", {"start": v(22.93, -29.63) * mm, "end": v(22.42, -30.4) * mm});
            skLineSegment(sketch, "E2051", {"start": v(22.42, -30.4) * mm, "end": v(21.95, -31.18) * mm});
            skLineSegment(sketch, "E2052", {"start": v(21.95, -31.18) * mm, "end": v(21.53, -31.96) * mm});
            skLineSegment(sketch, "E2053", {"start": v(21.53, -31.96) * mm, "end": v(21.16, -32.77) * mm});
            skLineSegment(sketch, "E2054", {"start": v(21.16, -32.77) * mm, "end": v(20.85, -33.64) * mm});
            skLineSegment(sketch, "E2055", {"start": v(20.85, -33.64) * mm, "end": v(20.6, -34.54) * mm});
            skLineSegment(sketch, "E2056", {"start": v(20.6, -34.54) * mm, "end": v(20.38, -35.49) * mm});
            skLineSegment(sketch, "E2057", {"start": v(20.38, -35.49) * mm, "end": v(20.22, -36.47) * mm});
            skLineSegment(sketch, "E2058", {"start": v(20.22, -36.47) * mm, "end": v(20.1, -37.47) * mm});
            skLineSegment(sketch, "E2059", {"start": v(20.1, -37.47) * mm, "end": v(20.02, -38.5) * mm});
            skLineSegment(sketch, "E2060", {"start": v(20.02, -38.5) * mm, "end": v(19.97, -39.56) * mm});
            skLineSegment(sketch, "E2061", {"start": v(19.97, -39.56) * mm, "end": v(19.95, -40.63) * mm});
            skLineSegment(sketch, "E2062", {"start": v(19.95, -40.63) * mm, "end": v(19.96, -41.7) * mm});
            skLineSegment(sketch, "E2063", {"start": v(19.96, -41.7) * mm, "end": v(19.98, -42.8) * mm});
            skLineSegment(sketch, "E2064", {"start": v(19.98, -42.8) * mm, "end": v(20.02, -43.88) * mm});
            skLineSegment(sketch, "E2065", {"start": v(20.02, -43.88) * mm, "end": v(20.08, -44.96) * mm});
            skLineSegment(sketch, "E2066", {"start": v(20.08, -44.96) * mm, "end": v(20.15, -46.04) * mm});
            skLineSegment(sketch, "E2067", {"start": v(20.15, -46.04) * mm, "end": v(20.21, -47.1) * mm});
            skLineSegment(sketch, "E2068", {"start": v(20.21, -47.1) * mm, "end": v(20.28, -48.15) * mm});
            skLineSegment(sketch, "E2069", {"start": v(20.28, -48.15) * mm, "end": v(20.35, -49.17) * mm});
            skLineSegment(sketch, "E2070", {"start": v(20.35, -49.17) * mm, "end": v(20.41, -50.17) * mm});
            skLineSegment(sketch, "E2071", {"start": v(20.41, -50.17) * mm, "end": v(20.46, -51.14) * mm});
            skLineSegment(sketch, "E2072", {"start": v(20.46, -51.14) * mm, "end": v(20.49, -52.07) * mm});
            skLineSegment(sketch, "E2073", {"start": v(20.49, -52.07) * mm, "end": v(20.5, -52.96) * mm});
            skLineSegment(sketch, "E2074", {"start": v(20.5, -52.96) * mm, "end": v(151.5, -52.96) * mm});
            skLineSegment(sketch, "E2075", {"start": v(151.5, -52.96) * mm, "end": v(151.5, -26.96) * mm});
            skLineSegment(sketch, "E2076", {"start": v(151.5, -26.96) * mm, "end": v(88.5, -26.96) * mm});
            skLineSegment(sketch, "E2077", {"start": v(88.5, -26.96) * mm, "end": v(89.21, -26.24) * mm});
            skLineSegment(sketch, "E2078", {"start": v(89.21, -26.24) * mm, "end": v(89.93, -25.53) * mm});
            skLineSegment(sketch, "E2079", {"start": v(89.93, -25.53) * mm, "end": v(90.65, -24.83) * mm});
            skLineSegment(sketch, "E2080", {"start": v(90.65, -24.83) * mm, "end": v(91.37, -24.12) * mm});
            skLineSegment(sketch, "E2081", {"start": v(91.37, -24.12) * mm, "end": v(92.09, -23.41) * mm});
            skLineSegment(sketch, "E2082", {"start": v(92.09, -23.41) * mm, "end": v(92.81, -22.71) * mm});
            skLineSegment(sketch, "E2083", {"start": v(92.81, -22.71) * mm, "end": v(93.53, -22) * mm});
            skLineSegment(sketch, "E2084", {"start": v(93.53, -22) * mm, "end": v(94.26, -21.3) * mm});
            skLineSegment(sketch, "E2085", {"start": v(94.26, -21.3) * mm, "end": v(94.99, -20.61) * mm});
            skLineSegment(sketch, "E2086", {"start": v(94.99, -20.61) * mm, "end": v(95.72, -19.91) * mm});
            skLineSegment(sketch, "E2087", {"start": v(95.72, -19.91) * mm, "end": v(96.45, -19.22) * mm});
            skLineSegment(sketch, "E2088", {"start": v(96.45, -19.22) * mm, "end": v(97.18, -18.52) * mm});
            skLineSegment(sketch, "E2089", {"start": v(97.18, -18.52) * mm, "end": v(97.91, -17.83) * mm});
            skLineSegment(sketch, "E2090", {"start": v(97.91, -17.83) * mm, "end": v(98.64, -17.14) * mm});
            skLineSegment(sketch, "E2091", {"start": v(98.64, -17.14) * mm, "end": v(99.38, -16.45) * mm});
            skLineSegment(sketch, "E2092", {"start": v(99.38, -16.45) * mm, "end": v(100.11, -15.76) * mm});
            skLineSegment(sketch, "E2093", {"start": v(100.11, -15.76) * mm, "end": v(100.85, -15.07) * mm});
            skLineSegment(sketch, "E2094", {"start": v(100.85, -15.07) * mm, "end": v(101.59, -14.38) * mm});
            skLineSegment(sketch, "E2095", {"start": v(101.59, -14.38) * mm, "end": v(102.33, -13.7) * mm});
            skLineSegment(sketch, "E2096", {"start": v(102.33, -13.7) * mm, "end": v(103.07, -13) * mm});
            skLineSegment(sketch, "E2097", {"start": v(103.07, -13) * mm, "end": v(103.8, -12.32) * mm});
            skLineSegment(sketch, "E2098", {"start": v(103.8, -12.32) * mm, "end": v(104.55, -11.64) * mm});
            skLineSegment(sketch, "E2099", {"start": v(104.55, -11.64) * mm, "end": v(105.3, -10.96) * mm});
            skLineSegment(sketch, "E2100", {"start": v(105.3, -10.96) * mm, "end": v(106.04, -10.27) * mm});
            skLineSegment(sketch, "E2101", {"start": v(106.04, -10.27) * mm, "end": v(106.78, -9.6) * mm});
            skLineSegment(sketch, "E2102", {"start": v(106.78, -9.6) * mm, "end": v(107.52, -8.9) * mm});
            skLineSegment(sketch, "E2103", {"start": v(107.52, -8.9) * mm, "end": v(108.27, -8.23) * mm});
            skLineSegment(sketch, "E2104", {"start": v(108.27, -8.23) * mm, "end": v(109.01, -7.55) * mm});
            skLineSegment(sketch, "E2105", {"start": v(109.01, -7.55) * mm, "end": v(109.76, -6.87) * mm});
            skLineSegment(sketch, "E2106", {"start": v(109.76, -6.87) * mm, "end": v(110.5, -6.19) * mm});
            skLineSegment(sketch, "E2107", {"start": v(110.5, -6.19) * mm, "end": v(111.25, -5.5) * mm});
            skLineSegment(sketch, "E2108", {"start": v(111.25, -5.5) * mm, "end": v(112, -4.83) * mm});
            skLineSegment(sketch, "E2109", {"start": v(112, -4.83) * mm, "end": v(112.74, -4.15) * mm});
            skLineSegment(sketch, "E2110", {"start": v(112.74, -4.15) * mm, "end": v(113.49, -3.47) * mm});
            skLineSegment(sketch, "E2111", {"start": v(113.49, -3.47) * mm, "end": v(114.23, -2.8) * mm});
            skLineSegment(sketch, "E2112", {"start": v(114.23, -2.8) * mm, "end": v(114.98, -2.11) * mm});
            skLineSegment(sketch, "E2113", {"start": v(114.98, -2.11) * mm, "end": v(115.73, -1.43) * mm});
            skLineSegment(sketch, "E2114", {"start": v(115.73, -1.43) * mm, "end": v(116.47, -0.76) * mm});
            skLineSegment(sketch, "E2115", {"start": v(116.47, -0.76) * mm, "end": v(117.22, -0.08) * mm});
            skLineSegment(sketch, "E2116", {"start": v(117.22, -0.08) * mm, "end": v(117.97, 0.6) * mm});
            skLineSegment(sketch, "E2117", {"start": v(117.97, 0.6) * mm, "end": v(118.71, 1.28) * mm});
            skLineSegment(sketch, "E2118", {"start": v(118.71, 1.28) * mm, "end": v(119.46, 1.96) * mm});
            skLineSegment(sketch, "E2119", {"start": v(119.46, 1.96) * mm, "end": v(120.2, 2.64) * mm});
            skLineSegment(sketch, "E2120", {"start": v(120.2, 2.64) * mm, "end": v(120.95, 3.32) * mm});
            skLineSegment(sketch, "E2121", {"start": v(120.95, 3.32) * mm, "end": v(121.7, 4) * mm});
            skLineSegment(sketch, "E2122", {"start": v(121.7, 4) * mm, "end": v(122.44, 4.68) * mm});
            skLineSegment(sketch, "E2123", {"start": v(122.44, 4.68) * mm, "end": v(123.18, 5.37) * mm});
            skLineSegment(sketch, "E2124", {"start": v(123.18, 5.37) * mm, "end": v(123.92, 6.05) * mm});
            skLineSegment(sketch, "E2125", {"start": v(123.92, 6.05) * mm, "end": v(124.67, 6.73) * mm});
            skLineSegment(sketch, "E2126", {"start": v(124.67, 6.73) * mm, "end": v(125.4, 7.42) * mm});
            skLineSegment(sketch, "E2127", {"start": v(125.4, 7.42) * mm, "end": v(126.15, 8.1) * mm});
            skLineSegment(sketch, "E2128", {"start": v(126.15, 8.1) * mm, "end": v(126.89, 8.79) * mm});
            skLineSegment(sketch, "E2129", {"start": v(126.89, 8.79) * mm, "end": v(127.63, 9.47) * mm});
            skLineSegment(sketch, "E2130", {"start": v(127.63, 9.47) * mm, "end": v(128.36, 10.16) * mm});
            skLineSegment(sketch, "E2131", {"start": v(128.36, 10.16) * mm, "end": v(129.1, 10.85) * mm});
            skLineSegment(sketch, "E2132", {"start": v(129.1, 10.85) * mm, "end": v(129.84, 11.54) * mm});
            skLineSegment(sketch, "E2133", {"start": v(129.84, 11.54) * mm, "end": v(130.57, 12.23) * mm});
            skLineSegment(sketch, "E2134", {"start": v(130.57, 12.23) * mm, "end": v(131.3, 12.92) * mm});
            skLineSegment(sketch, "E2135", {"start": v(131.3, 12.92) * mm, "end": v(132.04, 13.61) * mm});
            skLineSegment(sketch, "E2136", {"start": v(132.04, 13.61) * mm, "end": v(132.77, 14.3) * mm});
            skLineSegment(sketch, "E2137", {"start": v(132.77, 14.3) * mm, "end": v(133.5, 15) * mm});
            skLineSegment(sketch, "E2138", {"start": v(133.5, 15) * mm, "end": v(134.15, 15.6) * mm});
            skLineSegment(sketch, "E2139", {"start": v(134.15, 15.6) * mm, "end": v(134.83, 16.22) * mm});
            skLineSegment(sketch, "E2140", {"start": v(134.83, 16.22) * mm, "end": v(135.55, 16.83) * mm});
            skLineSegment(sketch, "E2141", {"start": v(135.55, 16.83) * mm, "end": v(136.29, 17.45) * mm});
            skLineSegment(sketch, "E2142", {"start": v(136.29, 17.45) * mm, "end": v(137.05, 18.07) * mm});
            skLineSegment(sketch, "E2143", {"start": v(137.05, 18.07) * mm, "end": v(137.83, 18.7) * mm});
            skLineSegment(sketch, "E2144", {"start": v(137.83, 18.7) * mm, "end": v(138.63, 19.34) * mm});
            skLineSegment(sketch, "E2145", {"start": v(138.63, 19.34) * mm, "end": v(139.44, 19.98) * mm});
            skLineSegment(sketch, "E2146", {"start": v(139.44, 19.98) * mm, "end": v(140.25, 20.63) * mm});
            skLineSegment(sketch, "E2147", {"start": v(140.25, 20.63) * mm, "end": v(141.07, 21.3) * mm});
            skLineSegment(sketch, "E2148", {"start": v(141.07, 21.3) * mm, "end": v(141.88, 21.96) * mm});
            skLineSegment(sketch, "E2149", {"start": v(141.88, 21.96) * mm, "end": v(142.7, 22.63) * mm});
            skLineSegment(sketch, "E2150", {"start": v(142.7, 22.63) * mm, "end": v(143.5, 23.32) * mm});
            skLineSegment(sketch, "E2151", {"start": v(143.5, 23.32) * mm, "end": v(144.28, 24) * mm});
            skLineSegment(sketch, "E2152", {"start": v(144.28, 24) * mm, "end": v(145.05, 24.7) * mm});
            skLineSegment(sketch, "E2153", {"start": v(145.05, 24.7) * mm, "end": v(145.8, 25.42) * mm});
            skLineSegment(sketch, "E2154", {"start": v(145.8, 25.42) * mm, "end": v(146.52, 26.14) * mm});
            skLineSegment(sketch, "E2155", {"start": v(146.52, 26.14) * mm, "end": v(147.2, 26.88) * mm});
            skLineSegment(sketch, "E2156", {"start": v(147.2, 26.88) * mm, "end": v(147.87, 27.62) * mm});
            skLineSegment(sketch, "E2157", {"start": v(147.87, 27.62) * mm, "end": v(148.49, 28.37) * mm});
            skLineSegment(sketch, "E2158", {"start": v(148.49, 28.37) * mm, "end": v(149.07, 29.14) * mm});
            skLineSegment(sketch, "E2159", {"start": v(149.07, 29.14) * mm, "end": v(149.6, 29.92) * mm});
            skLineSegment(sketch, "E2160", {"start": v(149.6, 29.92) * mm, "end": v(150.1, 30.7) * mm});
            skLineSegment(sketch, "E2161", {"start": v(150.1, 30.7) * mm, "end": v(150.52, 31.51) * mm});
            skLineSegment(sketch, "E2162", {"start": v(150.52, 31.51) * mm, "end": v(150.9, 32.33) * mm});
            skLineSegment(sketch, "E2163", {"start": v(150.9, 32.33) * mm, "end": v(151.2, 33.15) * mm});
            skLineSegment(sketch, "E2164", {"start": v(151.2, 33.15) * mm, "end": v(151.46, 34.01) * mm});
            skLineSegment(sketch, "E2165", {"start": v(151.46, 34.01) * mm, "end": v(151.66, 34.92) * mm});
            skLineSegment(sketch, "E2166", {"start": v(151.66, 34.92) * mm, "end": v(151.83, 35.86) * mm});
            skLineSegment(sketch, "E2167", {"start": v(151.83, 35.86) * mm, "end": v(151.95, 36.83) * mm});
            skLineSegment(sketch, "E2168", {"start": v(151.95, 36.83) * mm, "end": v(152.04, 37.83) * mm});
            skLineSegment(sketch, "E2169", {"start": v(152.04, 37.83) * mm, "end": v(152.09, 38.85) * mm});
            skLineSegment(sketch, "E2170", {"start": v(152.09, 38.85) * mm, "end": v(152.11, 39.88) * mm});
            skLineSegment(sketch, "E2171", {"start": v(152.11, 39.88) * mm, "end": v(152.11, 40.93) * mm});
            skLineSegment(sketch, "E2172", {"start": v(152.11, 40.93) * mm, "end": v(152.1, 42) * mm});
            skLineSegment(sketch, "E2173", {"start": v(152.1, 42) * mm, "end": v(152.05, 43.06) * mm});
            skLineSegment(sketch, "E2174", {"start": v(152.05, 43.06) * mm, "end": v(152, 44.13) * mm});
            skLineSegment(sketch, "E2175", {"start": v(152, 44.13) * mm, "end": v(151.93, 45.2) * mm});
            skLineSegment(sketch, "E2176", {"start": v(151.93, 45.2) * mm, "end": v(151.86, 46.25) * mm});
            skLineSegment(sketch, "E2177", {"start": v(151.86, 46.25) * mm, "end": v(151.79, 47.29) * mm});
            skLineSegment(sketch, "E2178", {"start": v(151.79, 47.29) * mm, "end": v(151.72, 48.31) * mm});
            skLineSegment(sketch, "E2179", {"start": v(151.72, 48.31) * mm, "end": v(151.65, 49.32) * mm});
            skLineSegment(sketch, "E2180", {"start": v(151.65, 49.32) * mm, "end": v(151.59, 50.3) * mm});
            skLineSegment(sketch, "E2181", {"start": v(151.59, 50.3) * mm, "end": v(151.54, 51.25) * mm});
            skLineSegment(sketch, "E2182", {"start": v(151.54, 51.25) * mm, "end": v(151.51, 52.17) * mm});
            skLineSegment(sketch, "E2183", {"start": v(151.51, 52.17) * mm, "end": v(151.5, 53.04) * mm});
            skLineSegment(sketch, "E2184", {"start": v(151.5, 53.04) * mm, "end": v(20.5, 53.04) * mm});
            skLineSegment(sketch, "E2185", {"start": v(159.5, 53.04) * mm, "end": v(159.5, -8.96) * mm});
            skLineSegment(sketch, "E2186", {"start": v(159.5, -8.96) * mm, "end": v(159.5, -9.9) * mm});
            skLineSegment(sketch, "E2187", {"start": v(159.5, -9.9) * mm, "end": v(159.5, -10.84) * mm});
            skLineSegment(sketch, "E2188", {"start": v(159.5, -10.84) * mm, "end": v(159.5, -11.79) * mm});
            skLineSegment(sketch, "E2189", {"start": v(159.5, -11.79) * mm, "end": v(159.5, -12.75) * mm});
            skLineSegment(sketch, "E2190", {"start": v(159.5, -12.75) * mm, "end": v(159.49, -13.71) * mm});
            skLineSegment(sketch, "E2191", {"start": v(159.49, -13.71) * mm, "end": v(159.5, -14.68) * mm});
            skLineSegment(sketch, "E2192", {"start": v(159.5, -14.68) * mm, "end": v(159.5, -15.66) * mm});
            skLineSegment(sketch, "E2193", {"start": v(159.5, -15.66) * mm, "end": v(159.5, -16.64) * mm});
            skLineSegment(sketch, "E2194", {"start": v(159.5, -16.64) * mm, "end": v(159.52, -17.62) * mm});
            skLineSegment(sketch, "E2195", {"start": v(159.52, -17.62) * mm, "end": v(159.53, -18.6) * mm});
            skLineSegment(sketch, "E2196", {"start": v(159.53, -18.6) * mm, "end": v(159.56, -19.6) * mm});
            skLineSegment(sketch, "E2197", {"start": v(159.56, -19.6) * mm, "end": v(159.6, -20.59) * mm});
            skLineSegment(sketch, "E2198", {"start": v(159.6, -20.59) * mm, "end": v(159.64, -21.58) * mm});
            skLineSegment(sketch, "E2199", {"start": v(159.64, -21.58) * mm, "end": v(159.69, -22.57) * mm});
            skLineSegment(sketch, "E2200", {"start": v(159.69, -22.57) * mm, "end": v(159.75, -23.56) * mm});
            skLineSegment(sketch, "E2201", {"start": v(159.75, -23.56) * mm, "end": v(159.82, -24.55) * mm});
            skLineSegment(sketch, "E2202", {"start": v(159.82, -24.55) * mm, "end": v(159.9, -25.54) * mm});
            skLineSegment(sketch, "E2203", {"start": v(159.9, -25.54) * mm, "end": v(160, -26.53) * mm});
            skLineSegment(sketch, "E2204", {"start": v(160, -26.53) * mm, "end": v(160.12, -27.51) * mm});
            skLineSegment(sketch, "E2205", {"start": v(160.12, -27.51) * mm, "end": v(160.25, -28.49) * mm});
            skLineSegment(sketch, "E2206", {"start": v(160.25, -28.49) * mm, "end": v(160.4, -29.47) * mm});
            skLineSegment(sketch, "E2207", {"start": v(160.4, -29.47) * mm, "end": v(160.55, -30.44) * mm});
            skLineSegment(sketch, "E2208", {"start": v(160.55, -30.44) * mm, "end": v(160.73, -31.4) * mm});
            skLineSegment(sketch, "E2209", {"start": v(160.73, -31.4) * mm, "end": v(160.93, -32.36) * mm});
            skLineSegment(sketch, "E2210", {"start": v(160.93, -32.36) * mm, "end": v(161.15, -33.31) * mm});
            skLineSegment(sketch, "E2211", {"start": v(161.15, -33.31) * mm, "end": v(161.38, -34.26) * mm});
            skLineSegment(sketch, "E2212", {"start": v(161.38, -34.26) * mm, "end": v(161.64, -35.2) * mm});
            skLineSegment(sketch, "E2213", {"start": v(161.64, -35.2) * mm, "end": v(161.92, -36.12) * mm});
            skLineSegment(sketch, "E2214", {"start": v(161.92, -36.12) * mm, "end": v(162.23, -37.04) * mm});
            skLineSegment(sketch, "E2215", {"start": v(162.23, -37.04) * mm, "end": v(162.56, -37.94) * mm});
            skLineSegment(sketch, "E2216", {"start": v(162.56, -37.94) * mm, "end": v(162.9, -38.84) * mm});
            skLineSegment(sketch, "E2217", {"start": v(162.9, -38.84) * mm, "end": v(163.29, -39.72) * mm});
            skLineSegment(sketch, "E2218", {"start": v(163.29, -39.72) * mm, "end": v(163.7, -40.6) * mm});
            skLineSegment(sketch, "E2219", {"start": v(163.7, -40.6) * mm, "end": v(164.13, -41.46) * mm});
            skLineSegment(sketch, "E2220", {"start": v(164.13, -41.46) * mm, "end": v(164.6, -42.3) * mm});
            skLineSegment(sketch, "E2221", {"start": v(164.6, -42.3) * mm, "end": v(165.08, -43.14) * mm});
            skLineSegment(sketch, "E2222", {"start": v(165.08, -43.14) * mm, "end": v(165.6, -43.95) * mm});
            skLineSegment(sketch, "E2223", {"start": v(165.6, -43.95) * mm, "end": v(166.2, -44.8) * mm});
            skLineSegment(sketch, "E2224", {"start": v(166.2, -44.8) * mm, "end": v(166.8, -45.6) * mm});
            skLineSegment(sketch, "E2225", {"start": v(166.8, -45.6) * mm, "end": v(167.45, -46.37) * mm});
            skLineSegment(sketch, "E2226", {"start": v(167.45, -46.37) * mm, "end": v(168.1, -47.1) * mm});
            skLineSegment(sketch, "E2227", {"start": v(168.1, -47.1) * mm, "end": v(168.8, -47.8) * mm});
            skLineSegment(sketch, "E2228", {"start": v(168.8, -47.8) * mm, "end": v(169.5, -48.48) * mm});
            skLineSegment(sketch, "E2229", {"start": v(169.5, -48.48) * mm, "end": v(170.22, -49.11) * mm});
            skLineSegment(sketch, "E2230", {"start": v(170.22, -49.11) * mm, "end": v(170.97, -49.72) * mm});
            skLineSegment(sketch, "E2231", {"start": v(170.97, -49.72) * mm, "end": v(171.74, -50.29) * mm});
            skLineSegment(sketch, "E2232", {"start": v(171.74, -50.29) * mm, "end": v(172.52, -50.83) * mm});
            skLineSegment(sketch, "E2233", {"start": v(172.52, -50.83) * mm, "end": v(173.32, -51.35) * mm});
            skLineSegment(sketch, "E2234", {"start": v(173.32, -51.35) * mm, "end": v(174.14, -51.84) * mm});
            skLineSegment(sketch, "E2235", {"start": v(174.14, -51.84) * mm, "end": v(174.97, -52.3) * mm});
            skLineSegment(sketch, "E2236", {"start": v(174.97, -52.3) * mm, "end": v(175.82, -52.75) * mm});
            skLineSegment(sketch, "E2237", {"start": v(175.82, -52.75) * mm, "end": v(176.68, -53.17) * mm});
            skLineSegment(sketch, "E2238", {"start": v(176.68, -53.17) * mm, "end": v(177.56, -53.56) * mm});
            skLineSegment(sketch, "E2239", {"start": v(177.56, -53.56) * mm, "end": v(178.44, -53.94) * mm});
            skLineSegment(sketch, "E2240", {"start": v(178.44, -53.94) * mm, "end": v(179.34, -54.29) * mm});
            skLineSegment(sketch, "E2241", {"start": v(179.34, -54.29) * mm, "end": v(180.25, -54.63) * mm});
            skLineSegment(sketch, "E2242", {"start": v(180.25, -54.63) * mm, "end": v(181.16, -54.94) * mm});
            skLineSegment(sketch, "E2243", {"start": v(181.16, -54.94) * mm, "end": v(182.09, -55.24) * mm});
            skLineSegment(sketch, "E2244", {"start": v(182.09, -55.24) * mm, "end": v(183.02, -55.53) * mm});
            skLineSegment(sketch, "E2245", {"start": v(183.02, -55.53) * mm, "end": v(183.96, -55.8) * mm});
            skLineSegment(sketch, "E2246", {"start": v(183.96, -55.8) * mm, "end": v(184.9, -56.06) * mm});
            skLineSegment(sketch, "E2247", {"start": v(184.9, -56.06) * mm, "end": v(185.85, -56.3) * mm});
            skLineSegment(sketch, "E2248", {"start": v(185.85, -56.3) * mm, "end": v(186.8, -56.54) * mm});
            skLineSegment(sketch, "E2249", {"start": v(186.8, -56.54) * mm, "end": v(187.76, -56.76) * mm});
            skLineSegment(sketch, "E2250", {"start": v(187.76, -56.76) * mm, "end": v(188.72, -56.98) * mm});
            skLineSegment(sketch, "E2251", {"start": v(188.72, -56.98) * mm, "end": v(189.67, -57.18) * mm});
            skLineSegment(sketch, "E2252", {"start": v(189.67, -57.18) * mm, "end": v(190.63, -57.38) * mm});
            skLineSegment(sketch, "E2253", {"start": v(190.63, -57.38) * mm, "end": v(191.6, -57.58) * mm});
            skLineSegment(sketch, "E2254", {"start": v(191.6, -57.58) * mm, "end": v(192.55, -57.77) * mm});
            skLineSegment(sketch, "E2255", {"start": v(192.55, -57.77) * mm, "end": v(193.5, -57.96) * mm});
            skLineSegment(sketch, "E2256", {"start": v(193.5, -57.96) * mm, "end": v(194.45, -58.14) * mm});
            skLineSegment(sketch, "E2257", {"start": v(194.45, -58.14) * mm, "end": v(195.4, -58.31) * mm});
            skLineSegment(sketch, "E2258", {"start": v(195.4, -58.31) * mm, "end": v(196.36, -58.48) * mm});
            skLineSegment(sketch, "E2259", {"start": v(196.36, -58.48) * mm, "end": v(197.32, -58.64) * mm});
            skLineSegment(sketch, "E2260", {"start": v(197.32, -58.64) * mm, "end": v(198.28, -58.8) * mm});
            skLineSegment(sketch, "E2261", {"start": v(198.28, -58.8) * mm, "end": v(199.25, -58.94) * mm});
            skLineSegment(sketch, "E2262", {"start": v(199.25, -58.94) * mm, "end": v(200.23, -59.08) * mm});
            skLineSegment(sketch, "E2263", {"start": v(200.23, -59.08) * mm, "end": v(201.2, -59.21) * mm});
            skLineSegment(sketch, "E2264", {"start": v(201.2, -59.21) * mm, "end": v(202.2, -59.34) * mm});
            skLineSegment(sketch, "E2265", {"start": v(202.2, -59.34) * mm, "end": v(203.18, -59.46) * mm});
            skLineSegment(sketch, "E2266", {"start": v(203.18, -59.46) * mm, "end": v(204.17, -59.57) * mm});
            skLineSegment(sketch, "E2267", {"start": v(204.17, -59.57) * mm, "end": v(205.16, -59.68) * mm});
            skLineSegment(sketch, "E2268", {"start": v(205.16, -59.68) * mm, "end": v(206.16, -59.78) * mm});
            skLineSegment(sketch, "E2269", {"start": v(206.16, -59.78) * mm, "end": v(207.16, -59.88) * mm});
            skLineSegment(sketch, "E2270", {"start": v(207.16, -59.88) * mm, "end": v(208.16, -59.96) * mm});
            skLineSegment(sketch, "E2271", {"start": v(208.16, -59.96) * mm, "end": v(209.17, -60.05) * mm});
            skLineSegment(sketch, "E2272", {"start": v(209.17, -60.05) * mm, "end": v(210.18, -60.12) * mm});
            skLineSegment(sketch, "E2273", {"start": v(210.18, -60.12) * mm, "end": v(211.19, -60.2) * mm});
            skLineSegment(sketch, "E2274", {"start": v(211.19, -60.2) * mm, "end": v(212.2, -60.25) * mm});
            skLineSegment(sketch, "E2275", {"start": v(212.2, -60.25) * mm, "end": v(213.22, -60.3) * mm});
            skLineSegment(sketch, "E2276", {"start": v(213.22, -60.3) * mm, "end": v(214.24, -60.36) * mm});
            skLineSegment(sketch, "E2277", {"start": v(214.24, -60.36) * mm, "end": v(215.25, -60.4) * mm});
            skLineSegment(sketch, "E2278", {"start": v(215.25, -60.4) * mm, "end": v(216.28, -60.44) * mm});
            skLineSegment(sketch, "E2279", {"start": v(216.28, -60.44) * mm, "end": v(217.3, -60.47) * mm});
            skLineSegment(sketch, "E2280", {"start": v(217.3, -60.47) * mm, "end": v(218.32, -60.5) * mm});
            skLineSegment(sketch, "E2281", {"start": v(218.32, -60.5) * mm, "end": v(219.35, -60.52) * mm});
            skLineSegment(sketch, "E2282", {"start": v(219.35, -60.52) * mm, "end": v(220.37, -60.53) * mm});
            skLineSegment(sketch, "E2283", {"start": v(220.37, -60.53) * mm, "end": v(221.4, -60.54) * mm});
            skLineSegment(sketch, "E2284", {"start": v(221.4, -60.54) * mm, "end": v(222.43, -60.54) * mm});
            skLineSegment(sketch, "E2285", {"start": v(222.43, -60.54) * mm, "end": v(223.46, -60.54) * mm});
            skLineSegment(sketch, "E2286", {"start": v(223.46, -60.54) * mm, "end": v(224.48, -60.53) * mm});
            skLineSegment(sketch, "E2287", {"start": v(224.48, -60.53) * mm, "end": v(225.51, -60.51) * mm});
            skLineSegment(sketch, "E2288", {"start": v(225.51, -60.51) * mm, "end": v(226.54, -60.5) * mm});
            skLineSegment(sketch, "E2289", {"start": v(226.54, -60.5) * mm, "end": v(227.57, -60.46) * mm});
            skLineSegment(sketch, "E2290", {"start": v(227.57, -60.46) * mm, "end": v(228.6, -60.43) * mm});
            skLineSegment(sketch, "E2291", {"start": v(228.6, -60.43) * mm, "end": v(229.63, -60.4) * mm});
            skLineSegment(sketch, "E2292", {"start": v(229.63, -60.4) * mm, "end": v(230.65, -60.35) * mm});
            skLineSegment(sketch, "E2293", {"start": v(230.65, -60.35) * mm, "end": v(231.68, -60.3) * mm});
            skLineSegment(sketch, "E2294", {"start": v(231.68, -60.3) * mm, "end": v(232.7, -60.24) * mm});
            skLineSegment(sketch, "E2295", {"start": v(232.7, -60.24) * mm, "end": v(233.73, -60.18) * mm});
            skLineSegment(sketch, "E2296", {"start": v(233.73, -60.18) * mm, "end": v(234.75, -60.12) * mm});
            skLineSegment(sketch, "E2297", {"start": v(234.75, -60.12) * mm, "end": v(235.78, -60.04) * mm});
            skLineSegment(sketch, "E2298", {"start": v(235.78, -60.04) * mm, "end": v(236.8, -59.97) * mm});
            skLineSegment(sketch, "E2299", {"start": v(236.8, -59.97) * mm, "end": v(237.81, -59.88) * mm});
            skLineSegment(sketch, "E2300", {"start": v(237.81, -59.88) * mm, "end": v(238.83, -59.8) * mm});
            skLineSegment(sketch, "E2301", {"start": v(238.83, -59.8) * mm, "end": v(239.84, -59.7) * mm});
            skLineSegment(sketch, "E2302", {"start": v(239.84, -59.7) * mm, "end": v(240.86, -59.6) * mm});
            skLineSegment(sketch, "E2303", {"start": v(240.86, -59.6) * mm, "end": v(241.87, -59.5) * mm});
            skLineSegment(sketch, "E2304", {"start": v(241.87, -59.5) * mm, "end": v(242.87, -59.39) * mm});
            skLineSegment(sketch, "E2305", {"start": v(242.87, -59.39) * mm, "end": v(243.88, -59.27) * mm});
            skLineSegment(sketch, "E2306", {"start": v(243.88, -59.27) * mm, "end": v(244.88, -59.15) * mm});
            skLineSegment(sketch, "E2307", {"start": v(244.88, -59.15) * mm, "end": v(245.88, -59.03) * mm});
            skLineSegment(sketch, "E2308", {"start": v(245.88, -59.03) * mm, "end": v(246.87, -58.9) * mm});
            skLineSegment(sketch, "E2309", {"start": v(246.87, -58.9) * mm, "end": v(247.86, -58.76) * mm});
            skLineSegment(sketch, "E2310", {"start": v(247.86, -58.76) * mm, "end": v(248.85, -58.62) * mm});
            skLineSegment(sketch, "E2311", {"start": v(248.85, -58.62) * mm, "end": v(249.84, -58.48) * mm});
            skLineSegment(sketch, "E2312", {"start": v(249.84, -58.48) * mm, "end": v(250.82, -58.33) * mm});
            skLineSegment(sketch, "E2313", {"start": v(250.82, -58.33) * mm, "end": v(251.8, -58.17) * mm});
            skLineSegment(sketch, "E2314", {"start": v(251.8, -58.17) * mm, "end": v(252.76, -58.01) * mm});
            skLineSegment(sketch, "E2315", {"start": v(252.76, -58.01) * mm, "end": v(253.73, -57.85) * mm});
            skLineSegment(sketch, "E2316", {"start": v(253.73, -57.85) * mm, "end": v(254.7, -57.68) * mm});
            skLineSegment(sketch, "E2317", {"start": v(254.7, -57.68) * mm, "end": v(255.65, -57.5) * mm});
            skLineSegment(sketch, "E2318", {"start": v(255.65, -57.5) * mm, "end": v(256.6, -57.33) * mm});
            skLineSegment(sketch, "E2319", {"start": v(256.6, -57.33) * mm, "end": v(257.56, -57.14) * mm});
            skLineSegment(sketch, "E2320", {"start": v(257.56, -57.14) * mm, "end": v(258.5, -56.95) * mm});
            skLineSegment(sketch, "E2321", {"start": v(258.5, -56.95) * mm, "end": v(259.47, -56.75) * mm});
            skLineSegment(sketch, "E2322", {"start": v(259.47, -56.75) * mm, "end": v(260.43, -56.54) * mm});
            skLineSegment(sketch, "E2323", {"start": v(260.43, -56.54) * mm, "end": v(261.39, -56.3) * mm});
            skLineSegment(sketch, "E2324", {"start": v(261.39, -56.3) * mm, "end": v(262.34, -56.07) * mm});
            skLineSegment(sketch, "E2325", {"start": v(262.34, -56.07) * mm, "end": v(263.3, -55.81) * mm});
            skLineSegment(sketch, "E2326", {"start": v(263.3, -55.81) * mm, "end": v(264.23, -55.54) * mm});
            skLineSegment(sketch, "E2327", {"start": v(264.23, -55.54) * mm, "end": v(265.17, -55.26) * mm});
            skLineSegment(sketch, "E2328", {"start": v(265.17, -55.26) * mm, "end": v(266.1, -54.96) * mm});
            skLineSegment(sketch, "E2329", {"start": v(266.1, -54.96) * mm, "end": v(267.03, -54.64) * mm});
            skLineSegment(sketch, "E2330", {"start": v(267.03, -54.64) * mm, "end": v(267.94, -54.31) * mm});
            skLineSegment(sketch, "E2331", {"start": v(267.94, -54.31) * mm, "end": v(268.85, -53.96) * mm});
            skLineSegment(sketch, "E2332", {"start": v(268.85, -53.96) * mm, "end": v(269.75, -53.6) * mm});
            skLineSegment(sketch, "E2333", {"start": v(269.75, -53.6) * mm, "end": v(270.63, -53.21) * mm});
            skLineSegment(sketch, "E2334", {"start": v(270.63, -53.21) * mm, "end": v(271.51, -52.8) * mm});
            skLineSegment(sketch, "E2335", {"start": v(271.51, -52.8) * mm, "end": v(272.38, -52.39) * mm});
            skLineSegment(sketch, "E2336", {"start": v(272.38, -52.39) * mm, "end": v(273.23, -51.94) * mm});
            skLineSegment(sketch, "E2337", {"start": v(273.23, -51.94) * mm, "end": v(274.07, -51.48) * mm});
            skLineSegment(sketch, "E2338", {"start": v(274.07, -51.48) * mm, "end": v(274.9, -51) * mm});
            skLineSegment(sketch, "E2339", {"start": v(274.9, -51) * mm, "end": v(275.72, -50.5) * mm});
            skLineSegment(sketch, "E2340", {"start": v(275.72, -50.5) * mm, "end": v(276.52, -49.97) * mm});
            skLineSegment(sketch, "E2341", {"start": v(276.52, -49.97) * mm, "end": v(277.3, -49.43) * mm});
            skLineSegment(sketch, "E2342", {"start": v(277.3, -49.43) * mm, "end": v(278.08, -48.86) * mm});
            skLineSegment(sketch, "E2343", {"start": v(278.08, -48.86) * mm, "end": v(278.83, -48.26) * mm});
            skLineSegment(sketch, "E2344", {"start": v(278.83, -48.26) * mm, "end": v(279.57, -47.65) * mm});
            skLineSegment(sketch, "E2345", {"start": v(279.57, -47.65) * mm, "end": v(280.3, -47) * mm});
            skLineSegment(sketch, "E2346", {"start": v(280.3, -47) * mm, "end": v(281, -46.34) * mm});
            skLineSegment(sketch, "E2347", {"start": v(281, -46.34) * mm, "end": v(281.68, -45.65) * mm});
            skLineSegment(sketch, "E2348", {"start": v(281.68, -45.65) * mm, "end": v(282.35, -44.94) * mm});
            skLineSegment(sketch, "E2349", {"start": v(282.35, -44.94) * mm, "end": v(283, -44.2) * mm});
            skLineSegment(sketch, "E2350", {"start": v(283, -44.2) * mm, "end": v(283.62, -43.43) * mm});
            skLineSegment(sketch, "E2351", {"start": v(283.62, -43.43) * mm, "end": v(284.22, -42.63) * mm});
            skLineSegment(sketch, "E2352", {"start": v(284.22, -42.63) * mm, "end": v(284.8, -41.8) * mm});
            skLineSegment(sketch, "E2353", {"start": v(284.8, -41.8) * mm, "end": v(285.37, -40.96) * mm});
            skLineSegment(sketch, "E2354", {"start": v(285.37, -40.96) * mm, "end": v(285.9, -40.09) * mm});
            skLineSegment(sketch, "E2355", {"start": v(285.9, -40.09) * mm, "end": v(286.39, -39.2) * mm});
            skLineSegment(sketch, "E2356", {"start": v(286.39, -39.2) * mm, "end": v(286.84, -38.32) * mm});
            skLineSegment(sketch, "E2357", {"start": v(286.84, -38.32) * mm, "end": v(287.27, -37.41) * mm});
            skLineSegment(sketch, "E2358", {"start": v(287.27, -37.41) * mm, "end": v(287.66, -36.5) * mm});
            skLineSegment(sketch, "E2359", {"start": v(287.66, -36.5) * mm, "end": v(288.02, -35.58) * mm});
            skLineSegment(sketch, "E2360", {"start": v(288.02, -35.58) * mm, "end": v(288.34, -34.64) * mm});
            skLineSegment(sketch, "E2361", {"start": v(288.34, -34.64) * mm, "end": v(288.64, -33.7) * mm});
            skLineSegment(sketch, "E2362", {"start": v(288.64, -33.7) * mm, "end": v(288.92, -32.75) * mm});
            skLineSegment(sketch, "E2363", {"start": v(288.92, -32.75) * mm, "end": v(289.16, -31.8) * mm});
            skLineSegment(sketch, "E2364", {"start": v(289.16, -31.8) * mm, "end": v(289.38, -30.83) * mm});
            skLineSegment(sketch, "E2365", {"start": v(289.38, -30.83) * mm, "end": v(289.58, -29.86) * mm});
            skLineSegment(sketch, "E2366", {"start": v(289.58, -29.86) * mm, "end": v(289.76, -28.88) * mm});
            skLineSegment(sketch, "E2367", {"start": v(289.76, -28.88) * mm, "end": v(289.91, -27.9) * mm});
            skLineSegment(sketch, "E2368", {"start": v(289.91, -27.9) * mm, "end": v(290.05, -26.91) * mm});
            skLineSegment(sketch, "E2369", {"start": v(290.05, -26.91) * mm, "end": v(290.16, -25.92) * mm});
            skLineSegment(sketch, "E2370", {"start": v(290.16, -25.92) * mm, "end": v(290.26, -24.93) * mm});
            skLineSegment(sketch, "E2371", {"start": v(290.26, -24.93) * mm, "end": v(290.34, -23.93) * mm});
            skLineSegment(sketch, "E2372", {"start": v(290.34, -23.93) * mm, "end": v(290.4, -22.93) * mm});
            skLineSegment(sketch, "E2373", {"start": v(290.4, -22.93) * mm, "end": v(290.46, -21.92) * mm});
            skLineSegment(sketch, "E2374", {"start": v(290.46, -21.92) * mm, "end": v(290.5, -20.92) * mm});
            skLineSegment(sketch, "E2375", {"start": v(290.5, -20.92) * mm, "end": v(290.53, -19.91) * mm});
            skLineSegment(sketch, "E2376", {"start": v(290.53, -19.91) * mm, "end": v(290.55, -18.9) * mm});
            skLineSegment(sketch, "E2377", {"start": v(290.55, -18.9) * mm, "end": v(290.56, -17.9) * mm});
            skLineSegment(sketch, "E2378", {"start": v(290.56, -17.9) * mm, "end": v(290.57, -16.9) * mm});
            skLineSegment(sketch, "E2379", {"start": v(290.57, -16.9) * mm, "end": v(290.57, -15.89) * mm});
            skLineSegment(sketch, "E2380", {"start": v(290.57, -15.89) * mm, "end": v(290.56, -14.88) * mm});
            skLineSegment(sketch, "E2381", {"start": v(290.56, -14.88) * mm, "end": v(290.55, -13.88) * mm});
            skLineSegment(sketch, "E2382", {"start": v(290.55, -13.88) * mm, "end": v(290.54, -12.88) * mm});
            skLineSegment(sketch, "E2383", {"start": v(290.54, -12.88) * mm, "end": v(290.53, -11.9) * mm});
            skLineSegment(sketch, "E2384", {"start": v(290.53, -11.9) * mm, "end": v(290.52, -10.9) * mm});
            skLineSegment(sketch, "E2385", {"start": v(290.52, -10.9) * mm, "end": v(290.5, -9.91) * mm});
            skLineSegment(sketch, "E2386", {"start": v(290.5, -9.91) * mm, "end": v(290.5, -8.93) * mm});
            skLineSegment(sketch, "E2387", {"start": v(290.5, -8.93) * mm, "end": v(290.5, -7.96) * mm});
            skLineSegment(sketch, "E2388", {"start": v(290.5, -7.96) * mm, "end": v(290.5, 53.04) * mm});
            skLineSegment(sketch, "E2389", {"start": v(290.5, 53.04) * mm, "end": v(249.5, 53.04) * mm});
            skLineSegment(sketch, "E2390", {"start": v(249.5, 53.04) * mm, "end": v(249.5, 2.04) * mm});
            skLineSegment(sketch, "E2391", {"start": v(249.5, 2.04) * mm, "end": v(249.5, 1.12) * mm});
            skLineSegment(sketch, "E2392", {"start": v(249.5, 1.12) * mm, "end": v(249.53, 0.18) * mm});
            skLineSegment(sketch, "E2393", {"start": v(249.53, 0.18) * mm, "end": v(249.56, -0.78) * mm});
            skLineSegment(sketch, "E2394", {"start": v(249.56, -0.78) * mm, "end": v(249.6, -1.74) * mm});
            skLineSegment(sketch, "E2395", {"start": v(249.6, -1.74) * mm, "end": v(249.63, -2.72) * mm});
            skLineSegment(sketch, "E2396", {"start": v(249.63, -2.72) * mm, "end": v(249.68, -3.71) * mm});
            skLineSegment(sketch, "E2397", {"start": v(249.68, -3.71) * mm, "end": v(249.72, -4.7) * mm});
            skLineSegment(sketch, "E2398", {"start": v(249.72, -4.7) * mm, "end": v(249.75, -5.7) * mm});
            skLineSegment(sketch, "E2399", {"start": v(249.75, -5.7) * mm, "end": v(249.78, -6.71) * mm});
            skLineSegment(sketch, "E2400", {"start": v(249.78, -6.71) * mm, "end": v(249.8, -7.72) * mm});
            skLineSegment(sketch, "E2401", {"start": v(249.8, -7.72) * mm, "end": v(249.81, -8.73) * mm});
            skLineSegment(sketch, "E2402", {"start": v(249.81, -8.73) * mm, "end": v(249.8, -9.74) * mm});
            skLineSegment(sketch, "E2403", {"start": v(249.8, -9.74) * mm, "end": v(249.79, -10.74) * mm});
            skLineSegment(sketch, "E2404", {"start": v(249.79, -10.74) * mm, "end": v(249.74, -11.74) * mm});
            skLineSegment(sketch, "E2405", {"start": v(249.74, -11.74) * mm, "end": v(249.67, -12.74) * mm});
            skLineSegment(sketch, "E2406", {"start": v(249.67, -12.74) * mm, "end": v(249.58, -13.72) * mm});
            skLineSegment(sketch, "E2407", {"start": v(249.58, -13.72) * mm, "end": v(249.46, -14.7) * mm});
            skLineSegment(sketch, "E2408", {"start": v(249.46, -14.7) * mm, "end": v(249.3, -15.67) * mm});
            skLineSegment(sketch, "E2409", {"start": v(249.3, -15.67) * mm, "end": v(249.12, -16.62) * mm});
            skLineSegment(sketch, "E2410", {"start": v(249.12, -16.62) * mm, "end": v(248.9, -17.55) * mm});
            skLineSegment(sketch, "E2411", {"start": v(248.9, -17.55) * mm, "end": v(248.63, -18.47) * mm});
            skLineSegment(sketch, "E2412", {"start": v(248.63, -18.47) * mm, "end": v(248.33, -19.38) * mm});
            skLineSegment(sketch, "E2413", {"start": v(248.33, -19.38) * mm, "end": v(247.98, -20.26) * mm});
            skLineSegment(sketch, "E2414", {"start": v(247.98, -20.26) * mm, "end": v(247.58, -21.12) * mm});
            skLineSegment(sketch, "E2415", {"start": v(247.58, -21.12) * mm, "end": v(247.13, -21.95) * mm});
            skLineSegment(sketch, "E2416", {"start": v(247.13, -21.95) * mm, "end": v(246.72, -22.63) * mm});
            skLineSegment(sketch, "E2417", {"start": v(246.72, -22.63) * mm, "end": v(246.28, -23.28) * mm});
            skLineSegment(sketch, "E2418", {"start": v(246.28, -23.28) * mm, "end": v(245.8, -23.91) * mm});
            skLineSegment(sketch, "E2419", {"start": v(245.8, -23.91) * mm, "end": v(245.3, -24.52) * mm});
            skLineSegment(sketch, "E2420", {"start": v(245.3, -24.52) * mm, "end": v(244.76, -25.1) * mm});
            skLineSegment(sketch, "E2421", {"start": v(244.76, -25.1) * mm, "end": v(244.2, -25.67) * mm});
            skLineSegment(sketch, "E2422", {"start": v(244.2, -25.67) * mm, "end": v(243.61, -26.22) * mm});
            skLineSegment(sketch, "E2423", {"start": v(243.61, -26.22) * mm, "end": v(243, -26.74) * mm});
            skLineSegment(sketch, "E2424", {"start": v(243, -26.74) * mm, "end": v(242.36, -27.23) * mm});
            skLineSegment(sketch, "E2425", {"start": v(242.36, -27.23) * mm, "end": v(241.7, -27.7) * mm});
            skLineSegment(sketch, "E2426", {"start": v(241.7, -27.7) * mm, "end": v(241.02, -28.16) * mm});
            skLineSegment(sketch, "E2427", {"start": v(241.02, -28.16) * mm, "end": v(240.32, -28.59) * mm});
            skLineSegment(sketch, "E2428", {"start": v(240.32, -28.59) * mm, "end": v(239.6, -29) * mm});
            skLineSegment(sketch, "E2429", {"start": v(239.6, -29) * mm, "end": v(238.85, -29.38) * mm});
            skLineSegment(sketch, "E2430", {"start": v(238.85, -29.38) * mm, "end": v(238.1, -29.74) * mm});
            skLineSegment(sketch, "E2431", {"start": v(238.1, -29.74) * mm, "end": v(237.31, -30.08) * mm});
            skLineSegment(sketch, "E2432", {"start": v(237.31, -30.08) * mm, "end": v(236.52, -30.4) * mm});
            skLineSegment(sketch, "E2433", {"start": v(236.52, -30.4) * mm, "end": v(235.72, -30.7) * mm});
            skLineSegment(sketch, "E2434", {"start": v(235.72, -30.7) * mm, "end": v(234.9, -30.97) * mm});
            skLineSegment(sketch, "E2435", {"start": v(234.9, -30.97) * mm, "end": v(234.06, -31.21) * mm});
            skLineSegment(sketch, "E2436", {"start": v(234.06, -31.21) * mm, "end": v(233.22, -31.44) * mm});
            skLineSegment(sketch, "E2437", {"start": v(233.22, -31.44) * mm, "end": v(232.37, -31.64) * mm});
            skLineSegment(sketch, "E2438", {"start": v(232.37, -31.64) * mm, "end": v(231.5, -31.83) * mm});
            skLineSegment(sketch, "E2439", {"start": v(231.5, -31.83) * mm, "end": v(230.63, -31.98) * mm});
            skLineSegment(sketch, "E2440", {"start": v(230.63, -31.98) * mm, "end": v(229.75, -32.12) * mm});
            skLineSegment(sketch, "E2441", {"start": v(229.75, -32.12) * mm, "end": v(228.87, -32.23) * mm});
            skLineSegment(sketch, "E2442", {"start": v(228.87, -32.23) * mm, "end": v(227.98, -32.32) * mm});
            skLineSegment(sketch, "E2443", {"start": v(227.98, -32.32) * mm, "end": v(227.1, -32.39) * mm});
            skLineSegment(sketch, "E2444", {"start": v(227.1, -32.39) * mm, "end": v(226.2, -32.43) * mm});
            skLineSegment(sketch, "E2445", {"start": v(226.2, -32.43) * mm, "end": v(225.3, -32.45) * mm});
            skLineSegment(sketch, "E2446", {"start": v(225.3, -32.45) * mm, "end": v(224.4, -32.45) * mm});
            skLineSegment(sketch, "E2447", {"start": v(224.4, -32.45) * mm, "end": v(223.5, -32.43) * mm});
            skLineSegment(sketch, "E2448", {"start": v(223.5, -32.43) * mm, "end": v(222.62, -32.38) * mm});
            skLineSegment(sketch, "E2449", {"start": v(222.62, -32.38) * mm, "end": v(221.73, -32.31) * mm});
            skLineSegment(sketch, "E2450", {"start": v(221.73, -32.31) * mm, "end": v(220.84, -32.22) * mm});
            skLineSegment(sketch, "E2451", {"start": v(220.84, -32.22) * mm, "end": v(219.96, -32.1) * mm});
            skLineSegment(sketch, "E2452", {"start": v(219.96, -32.1) * mm, "end": v(219.08, -31.96) * mm});
            skLineSegment(sketch, "E2453", {"start": v(219.08, -31.96) * mm, "end": v(218.22, -31.8) * mm});
            skLineSegment(sketch, "E2454", {"start": v(218.22, -31.8) * mm, "end": v(217.36, -31.61) * mm});
            skLineSegment(sketch, "E2455", {"start": v(217.36, -31.61) * mm, "end": v(216.5, -31.4) * mm});
            skLineSegment(sketch, "E2456", {"start": v(216.5, -31.4) * mm, "end": v(215.67, -31.18) * mm});
            skLineSegment(sketch, "E2457", {"start": v(215.67, -31.18) * mm, "end": v(214.84, -30.92) * mm});
            skLineSegment(sketch, "E2458", {"start": v(214.84, -30.92) * mm, "end": v(214.03, -30.64) * mm});
            skLineSegment(sketch, "E2459", {"start": v(214.03, -30.64) * mm, "end": v(213.22, -30.34) * mm});
            skLineSegment(sketch, "E2460", {"start": v(213.22, -30.34) * mm, "end": v(212.44, -30.02) * mm});
            skLineSegment(sketch, "E2461", {"start": v(212.44, -30.02) * mm, "end": v(211.67, -29.67) * mm});
            skLineSegment(sketch, "E2462", {"start": v(211.67, -29.67) * mm, "end": v(210.92, -29.3) * mm});
            skLineSegment(sketch, "E2463", {"start": v(210.92, -29.3) * mm, "end": v(210.18, -28.9) * mm});
            skLineSegment(sketch, "E2464", {"start": v(210.18, -28.9) * mm, "end": v(209.47, -28.5) * mm});
            skLineSegment(sketch, "E2465", {"start": v(209.47, -28.5) * mm, "end": v(208.77, -28.05) * mm});
            skLineSegment(sketch, "E2466", {"start": v(208.77, -28.05) * mm, "end": v(208.1, -27.59) * mm});
            skLineSegment(sketch, "E2467", {"start": v(208.1, -27.59) * mm, "end": v(207.45, -27.1) * mm});
            skLineSegment(sketch, "E2468", {"start": v(207.45, -27.1) * mm, "end": v(206.82, -26.6) * mm});
            skLineSegment(sketch, "E2469", {"start": v(206.82, -26.6) * mm, "end": v(206.22, -26.06) * mm});
            skLineSegment(sketch, "E2470", {"start": v(206.22, -26.06) * mm, "end": v(205.64, -25.5) * mm});
            skLineSegment(sketch, "E2471", {"start": v(205.64, -25.5) * mm, "end": v(205.1, -24.93) * mm});
            skLineSegment(sketch, "E2472", {"start": v(205.1, -24.93) * mm, "end": v(204.57, -24.32) * mm});
            skLineSegment(sketch, "E2473", {"start": v(204.57, -24.32) * mm, "end": v(204.08, -23.7) * mm});
            skLineSegment(sketch, "E2474", {"start": v(204.08, -23.7) * mm, "end": v(203.61, -23.05) * mm});
            skLineSegment(sketch, "E2475", {"start": v(203.61, -23.05) * mm, "end": v(203.18, -22.37) * mm});
            skLineSegment(sketch, "E2476", {"start": v(203.18, -22.37) * mm, "end": v(202.78, -21.68) * mm});
            skLineSegment(sketch, "E2477", {"start": v(202.78, -21.68) * mm, "end": v(202.42, -20.96) * mm});
            skLineSegment(sketch, "E2478", {"start": v(202.42, -20.96) * mm, "end": v(202.02, -20.06) * mm});
            skLineSegment(sketch, "E2479", {"start": v(202.02, -20.06) * mm, "end": v(201.67, -19.14) * mm});
            skLineSegment(sketch, "E2480", {"start": v(201.67, -19.14) * mm, "end": v(201.37, -18.2) * mm});
            skLineSegment(sketch, "E2481", {"start": v(201.37, -18.2) * mm, "end": v(201.1, -17.25) * mm});
            skLineSegment(sketch, "E2482", {"start": v(201.1, -17.25) * mm, "end": v(200.89, -16.28) * mm});
            skLineSegment(sketch, "E2483", {"start": v(200.89, -16.28) * mm, "end": v(200.7, -15.3) * mm});
            skLineSegment(sketch, "E2484", {"start": v(200.7, -15.3) * mm, "end": v(200.55, -14.3) * mm});
            skLineSegment(sketch, "E2485", {"start": v(200.55, -14.3) * mm, "end": v(200.43, -13.28) * mm});
            skLineSegment(sketch, "E2486", {"start": v(200.43, -13.28) * mm, "end": v(200.33, -12.26) * mm});
            skLineSegment(sketch, "E2487", {"start": v(200.33, -12.26) * mm, "end": v(200.27, -11.23) * mm});
            skLineSegment(sketch, "E2488", {"start": v(200.27, -11.23) * mm, "end": v(200.22, -10.2) * mm});
            skLineSegment(sketch, "E2489", {"start": v(200.22, -10.2) * mm, "end": v(200.2, -9.16) * mm});
            skLineSegment(sketch, "E2490", {"start": v(200.2, -9.16) * mm, "end": v(200.2, -8.12) * mm});
            skLineSegment(sketch, "E2491", {"start": v(200.2, -8.12) * mm, "end": v(200.2, -7.08) * mm});
            skLineSegment(sketch, "E2492", {"start": v(200.2, -7.08) * mm, "end": v(200.22, -6.04) * mm});
            skLineSegment(sketch, "E2493", {"start": v(200.22, -6.04) * mm, "end": v(200.25, -5) * mm});
            skLineSegment(sketch, "E2494", {"start": v(200.25, -5) * mm, "end": v(200.29, -3.96) * mm});
            skLineSegment(sketch, "E2495", {"start": v(200.29, -3.96) * mm, "end": v(200.33, -2.93) * mm});
            skLineSegment(sketch, "E2496", {"start": v(200.33, -2.93) * mm, "end": v(200.37, -1.9) * mm});
            skLineSegment(sketch, "E2497", {"start": v(200.37, -1.9) * mm, "end": v(200.4, -0.9) * mm});
            skLineSegment(sketch, "E2498", {"start": v(200.4, -0.9) * mm, "end": v(200.44, 0.11) * mm});
            skLineSegment(sketch, "E2499", {"start": v(200.44, 0.11) * mm, "end": v(200.47, 1.1) * mm});
            skLineSegment(sketch, "E2500", {"start": v(200.47, 1.1) * mm, "end": v(200.5, 2.08) * mm});
            skLineSegment(sketch, "E2501", {"start": v(200.5, 2.08) * mm, "end": v(200.5, 3.04) * mm});
            skLineSegment(sketch, "E2502", {"start": v(200.5, 3.04) * mm, "end": v(200.5, 53.04) * mm});
            skLineSegment(sketch, "E2503", {"start": v(200.5, 53.04) * mm, "end": v(159.5, 53.04) * mm});
            skLineSegment(sketch, "E2504", {"start": v(305.5, 53.04) * mm, "end": v(305.5, -52.96) * mm});
            skLineSegment(sketch, "E2505", {"start": v(305.5, -52.96) * mm, "end": v(346.5, -52.96) * mm});
            skLineSegment(sketch, "E2506", {"start": v(346.5, -52.96) * mm, "end": v(346.5, -11.96) * mm});
            skLineSegment(sketch, "E2507", {"start": v(346.5, -11.96) * mm, "end": v(347.3, -12.53) * mm});
            skLineSegment(sketch, "E2508", {"start": v(347.3, -12.53) * mm, "end": v(348.1, -13.12) * mm});
            skLineSegment(sketch, "E2509", {"start": v(348.1, -13.12) * mm, "end": v(348.9, -13.72) * mm});
            skLineSegment(sketch, "E2510", {"start": v(348.9, -13.72) * mm, "end": v(349.68, -14.32) * mm});
            skLineSegment(sketch, "E2511", {"start": v(349.68, -14.32) * mm, "end": v(350.46, -14.95) * mm});
            skLineSegment(sketch, "E2512", {"start": v(350.46, -14.95) * mm, "end": v(351.24, -15.58) * mm});
            skLineSegment(sketch, "E2513", {"start": v(351.24, -15.58) * mm, "end": v(352.01, -16.22) * mm});
            skLineSegment(sketch, "E2514", {"start": v(352.01, -16.22) * mm, "end": v(352.78, -16.87) * mm});
            skLineSegment(sketch, "E2515", {"start": v(352.78, -16.87) * mm, "end": v(353.54, -17.53) * mm});
            skLineSegment(sketch, "E2516", {"start": v(353.54, -17.53) * mm, "end": v(354.3, -18.2) * mm});
            skLineSegment(sketch, "E2517", {"start": v(354.3, -18.2) * mm, "end": v(355.06, -18.87) * mm});
            skLineSegment(sketch, "E2518", {"start": v(355.06, -18.87) * mm, "end": v(355.8, -19.55) * mm});
            skLineSegment(sketch, "E2519", {"start": v(355.8, -19.55) * mm, "end": v(356.56, -20.24) * mm});
            skLineSegment(sketch, "E2520", {"start": v(356.56, -20.24) * mm, "end": v(357.3, -20.94) * mm});
            skLineSegment(sketch, "E2521", {"start": v(357.3, -20.94) * mm, "end": v(358.04, -21.64) * mm});
            skLineSegment(sketch, "E2522", {"start": v(358.04, -21.64) * mm, "end": v(358.78, -22.34) * mm});
            skLineSegment(sketch, "E2523", {"start": v(358.78, -22.34) * mm, "end": v(359.52, -23.06) * mm});
            skLineSegment(sketch, "E2524", {"start": v(359.52, -23.06) * mm, "end": v(360.25, -23.77) * mm});
            skLineSegment(sketch, "E2525", {"start": v(360.25, -23.77) * mm, "end": v(360.98, -24.5) * mm});
            skLineSegment(sketch, "E2526", {"start": v(360.98, -24.5) * mm, "end": v(361.7, -25.22) * mm});
            skLineSegment(sketch, "E2527", {"start": v(361.7, -25.22) * mm, "end": v(362.43, -25.94) * mm});
            skLineSegment(sketch, "E2528", {"start": v(362.43, -25.94) * mm, "end": v(363.16, -26.67) * mm});
            skLineSegment(sketch, "E2529", {"start": v(363.16, -26.67) * mm, "end": v(363.88, -27.4) * mm});
            skLineSegment(sketch, "E2530", {"start": v(363.88, -27.4) * mm, "end": v(364.6, -28.14) * mm});
            skLineSegment(sketch, "E2531", {"start": v(364.6, -28.14) * mm, "end": v(365.32, -28.87) * mm});
            skLineSegment(sketch, "E2532", {"start": v(365.32, -28.87) * mm, "end": v(366.04, -29.6) * mm});
            skLineSegment(sketch, "E2533", {"start": v(366.04, -29.6) * mm, "end": v(366.75, -30.34) * mm});
            skLineSegment(sketch, "E2534", {"start": v(366.75, -30.34) * mm, "end": v(367.47, -31.08) * mm});
            skLineSegment(sketch, "E2535", {"start": v(367.47, -31.08) * mm, "end": v(368.18, -31.81) * mm});
            skLineSegment(sketch, "E2536", {"start": v(368.18, -31.81) * mm, "end": v(368.9, -32.54) * mm});
            skLineSegment(sketch, "E2537", {"start": v(368.9, -32.54) * mm, "end": v(369.61, -33.27) * mm});
            skLineSegment(sketch, "E2538", {"start": v(369.61, -33.27) * mm, "end": v(370.33, -34) * mm});
            skLineSegment(sketch, "E2539", {"start": v(370.33, -34) * mm, "end": v(371.04, -34.73) * mm});
            skLineSegment(sketch, "E2540", {"start": v(371.04, -34.73) * mm, "end": v(371.76, -35.45) * mm});
            skLineSegment(sketch, "E2541", {"start": v(371.76, -35.45) * mm, "end": v(372.47, -36.17) * mm});
            skLineSegment(sketch, "E2542", {"start": v(372.47, -36.17) * mm, "end": v(373.19, -36.88) * mm});
            skLineSegment(sketch, "E2543", {"start": v(373.19, -36.88) * mm, "end": v(373.9, -37.6) * mm});
            skLineSegment(sketch, "E2544", {"start": v(373.9, -37.6) * mm, "end": v(374.62, -38.3) * mm});
            skLineSegment(sketch, "E2545", {"start": v(374.62, -38.3) * mm, "end": v(375.34, -39) * mm});
            skLineSegment(sketch, "E2546", {"start": v(375.34, -39) * mm, "end": v(376.06, -39.68) * mm});
            skLineSegment(sketch, "E2547", {"start": v(376.06, -39.68) * mm, "end": v(376.78, -40.37) * mm});
            skLineSegment(sketch, "E2548", {"start": v(376.78, -40.37) * mm, "end": v(377.5, -41.05) * mm});
            skLineSegment(sketch, "E2549", {"start": v(377.5, -41.05) * mm, "end": v(378.2, -41.72) * mm});
            skLineSegment(sketch, "E2550", {"start": v(378.2, -41.72) * mm, "end": v(378.9, -42.43) * mm});
            skLineSegment(sketch, "E2551", {"start": v(378.9, -42.43) * mm, "end": v(379.6, -43.16) * mm});
            skLineSegment(sketch, "E2552", {"start": v(379.6, -43.16) * mm, "end": v(380.3, -43.9) * mm});
            skLineSegment(sketch, "E2553", {"start": v(380.3, -43.9) * mm, "end": v(381.01, -44.66) * mm});
            skLineSegment(sketch, "E2554", {"start": v(381.01, -44.66) * mm, "end": v(381.72, -45.42) * mm});
            skLineSegment(sketch, "E2555", {"start": v(381.72, -45.42) * mm, "end": v(382.44, -46.18) * mm});
            skLineSegment(sketch, "E2556", {"start": v(382.44, -46.18) * mm, "end": v(383.16, -46.93) * mm});
            skLineSegment(sketch, "E2557", {"start": v(383.16, -46.93) * mm, "end": v(383.9, -47.67) * mm});
            skLineSegment(sketch, "E2558", {"start": v(383.9, -47.67) * mm, "end": v(384.64, -48.38) * mm});
            skLineSegment(sketch, "E2559", {"start": v(384.64, -48.38) * mm, "end": v(385.4, -49.08) * mm});
            skLineSegment(sketch, "E2560", {"start": v(385.4, -49.08) * mm, "end": v(386.18, -49.74) * mm});
            skLineSegment(sketch, "E2561", {"start": v(386.18, -49.74) * mm, "end": v(386.98, -50.36) * mm});
            skLineSegment(sketch, "E2562", {"start": v(386.98, -50.36) * mm, "end": v(387.8, -50.93) * mm});
            skLineSegment(sketch, "E2563", {"start": v(387.8, -50.93) * mm, "end": v(388.64, -51.46) * mm});
            skLineSegment(sketch, "E2564", {"start": v(388.64, -51.46) * mm, "end": v(389.5, -51.93) * mm});
            skLineSegment(sketch, "E2565", {"start": v(389.5, -51.93) * mm, "end": v(390.35, -52.3) * mm});
            skLineSegment(sketch, "E2566", {"start": v(390.35, -52.3) * mm, "end": v(391.24, -52.6) * mm});
            skLineSegment(sketch, "E2567", {"start": v(391.24, -52.6) * mm, "end": v(392.18, -52.85) * mm});
            skLineSegment(sketch, "E2568", {"start": v(392.18, -52.85) * mm, "end": v(393.16, -53.03) * mm});
            skLineSegment(sketch, "E2569", {"start": v(393.16, -53.03) * mm, "end": v(394.16, -53.17) * mm});
            skLineSegment(sketch, "E2570", {"start": v(394.16, -53.17) * mm, "end": v(395.2, -53.25) * mm});
            skLineSegment(sketch, "E2571", {"start": v(395.2, -53.25) * mm, "end": v(396.24, -53.3) * mm});
            skLineSegment(sketch, "E2572", {"start": v(396.24, -53.3) * mm, "end": v(397.3, -53.32) * mm});
            skLineSegment(sketch, "E2573", {"start": v(397.3, -53.32) * mm, "end": v(398.38, -53.3) * mm});
            skLineSegment(sketch, "E2574", {"start": v(398.38, -53.3) * mm, "end": v(399.45, -53.27) * mm});
            skLineSegment(sketch, "E2575", {"start": v(399.45, -53.27) * mm, "end": v(400.52, -53.23) * mm});
            skLineSegment(sketch, "E2576", {"start": v(400.52, -53.23) * mm, "end": v(401.57, -53.17) * mm});
            skLineSegment(sketch, "E2577", {"start": v(401.57, -53.17) * mm, "end": v(402.62, -53.1) * mm});
            skLineSegment(sketch, "E2578", {"start": v(402.62, -53.1) * mm, "end": v(403.63, -53.05) * mm});
            skLineSegment(sketch, "E2579", {"start": v(403.63, -53.05) * mm, "end": v(404.62, -53) * mm});
            skLineSegment(sketch, "E2580", {"start": v(404.62, -53) * mm, "end": v(405.58, -52.97) * mm});
            skLineSegment(sketch, "E2581", {"start": v(405.58, -52.97) * mm, "end": v(406.5, -52.96) * mm});
            skLineSegment(sketch, "E2582", {"start": v(406.5, -52.96) * mm, "end": v(445.5, -52.96) * mm});
            skLineSegment(sketch, "E2583", {"start": v(445.5, -52.96) * mm, "end": v(444.93, -52.19) * mm});
            skLineSegment(sketch, "E2584", {"start": v(444.93, -52.19) * mm, "end": v(444.34, -51.43) * mm});
            skLineSegment(sketch, "E2585", {"start": v(444.34, -51.43) * mm, "end": v(443.73, -50.67) * mm});
            skLineSegment(sketch, "E2586", {"start": v(443.73, -50.67) * mm, "end": v(443.12, -49.92) * mm});
            skLineSegment(sketch, "E2587", {"start": v(443.12, -49.92) * mm, "end": v(442.5, -49.18) * mm});
            skLineSegment(sketch, "E2588", {"start": v(442.5, -49.18) * mm, "end": v(441.85, -48.44) * mm});
            skLineSegment(sketch, "E2589", {"start": v(441.85, -48.44) * mm, "end": v(441.2, -47.71) * mm});
            skLineSegment(sketch, "E2590", {"start": v(441.2, -47.71) * mm, "end": v(440.53, -46.99) * mm});
            skLineSegment(sketch, "E2591", {"start": v(440.53, -46.99) * mm, "end": v(439.86, -46.27) * mm});
            skLineSegment(sketch, "E2592", {"start": v(439.86, -46.27) * mm, "end": v(439.17, -45.55) * mm});
            skLineSegment(sketch, "E2593", {"start": v(439.17, -45.55) * mm, "end": v(438.48, -44.84) * mm});
            skLineSegment(sketch, "E2594", {"start": v(438.48, -44.84) * mm, "end": v(437.77, -44.13) * mm});
            skLineSegment(sketch, "E2595", {"start": v(437.77, -44.13) * mm, "end": v(437.06, -43.43) * mm});
            skLineSegment(sketch, "E2596", {"start": v(437.06, -43.43) * mm, "end": v(436.34, -42.73) * mm});
            skLineSegment(sketch, "E2597", {"start": v(436.34, -42.73) * mm, "end": v(435.6, -42.04) * mm});
            skLineSegment(sketch, "E2598", {"start": v(435.6, -42.04) * mm, "end": v(434.87, -41.35) * mm});
            skLineSegment(sketch, "E2599", {"start": v(434.87, -41.35) * mm, "end": v(434.13, -40.67) * mm});
            skLineSegment(sketch, "E2600", {"start": v(434.13, -40.67) * mm, "end": v(433.38, -39.99) * mm});
            skLineSegment(sketch, "E2601", {"start": v(433.38, -39.99) * mm, "end": v(432.62, -39.3) * mm});
            skLineSegment(sketch, "E2602", {"start": v(432.62, -39.3) * mm, "end": v(431.86, -38.63) * mm});
            skLineSegment(sketch, "E2603", {"start": v(431.86, -38.63) * mm, "end": v(431.09, -37.96) * mm});
            skLineSegment(sketch, "E2604", {"start": v(431.09, -37.96) * mm, "end": v(430.32, -37.3) * mm});
            skLineSegment(sketch, "E2605", {"start": v(430.32, -37.3) * mm, "end": v(429.54, -36.63) * mm});
            skLineSegment(sketch, "E2606", {"start": v(429.54, -36.63) * mm, "end": v(428.76, -35.97) * mm});
            skLineSegment(sketch, "E2607", {"start": v(428.76, -35.97) * mm, "end": v(427.98, -35.3) * mm});
            skLineSegment(sketch, "E2608", {"start": v(427.98, -35.3) * mm, "end": v(427.2, -34.65) * mm});
            skLineSegment(sketch, "E2609", {"start": v(427.2, -34.65) * mm, "end": v(426.4, -34) * mm});
            skLineSegment(sketch, "E2610", {"start": v(426.4, -34) * mm, "end": v(425.62, -33.35) * mm});
            skLineSegment(sketch, "E2611", {"start": v(425.62, -33.35) * mm, "end": v(424.82, -32.7) * mm});
            skLineSegment(sketch, "E2612", {"start": v(424.82, -32.7) * mm, "end": v(424.03, -32.05) * mm});
            skLineSegment(sketch, "E2613", {"start": v(424.03, -32.05) * mm, "end": v(423.24, -31.4) * mm});
            skLineSegment(sketch, "E2614", {"start": v(423.24, -31.4) * mm, "end": v(422.45, -30.76) * mm});
            skLineSegment(sketch, "E2615", {"start": v(422.45, -30.76) * mm, "end": v(421.66, -30.11) * mm});
            skLineSegment(sketch, "E2616", {"start": v(421.66, -30.11) * mm, "end": v(420.87, -29.47) * mm});
            skLineSegment(sketch, "E2617", {"start": v(420.87, -29.47) * mm, "end": v(420.08, -28.83) * mm});
            skLineSegment(sketch, "E2618", {"start": v(420.08, -28.83) * mm, "end": v(419.3, -28.2) * mm});
            skLineSegment(sketch, "E2619", {"start": v(419.3, -28.2) * mm, "end": v(418.51, -27.55) * mm});
            skLineSegment(sketch, "E2620", {"start": v(418.51, -27.55) * mm, "end": v(417.73, -26.91) * mm});
            skLineSegment(sketch, "E2621", {"start": v(417.73, -26.91) * mm, "end": v(416.96, -26.28) * mm});
            skLineSegment(sketch, "E2622", {"start": v(416.96, -26.28) * mm, "end": v(416.19, -25.64) * mm});
            skLineSegment(sketch, "E2623", {"start": v(416.19, -25.64) * mm, "end": v(415.42, -25) * mm});
            skLineSegment(sketch, "E2624", {"start": v(415.42, -25) * mm, "end": v(414.66, -24.36) * mm});
            skLineSegment(sketch, "E2625", {"start": v(414.66, -24.36) * mm, "end": v(413.9, -23.72) * mm});
            skLineSegment(sketch, "E2626", {"start": v(413.9, -23.72) * mm, "end": v(413.15, -23.08) * mm});
            skLineSegment(sketch, "E2627", {"start": v(413.15, -23.08) * mm, "end": v(412.4, -22.45) * mm});
            skLineSegment(sketch, "E2628", {"start": v(412.4, -22.45) * mm, "end": v(411.67, -21.8) * mm});
            skLineSegment(sketch, "E2629", {"start": v(411.67, -21.8) * mm, "end": v(410.94, -21.17) * mm});
            skLineSegment(sketch, "E2630", {"start": v(410.94, -21.17) * mm, "end": v(410.21, -20.52) * mm});
            skLineSegment(sketch, "E2631", {"start": v(410.21, -20.52) * mm, "end": v(409.5, -19.88) * mm});
            skLineSegment(sketch, "E2632", {"start": v(409.5, -19.88) * mm, "end": v(408.81, -19.25) * mm});
            skLineSegment(sketch, "E2633", {"start": v(408.81, -19.25) * mm, "end": v(408.12, -18.6) * mm});
            skLineSegment(sketch, "E2634", {"start": v(408.12, -18.6) * mm, "end": v(407.42, -17.95) * mm});
            skLineSegment(sketch, "E2635", {"start": v(407.42, -17.95) * mm, "end": v(406.73, -17.28) * mm});
            skLineSegment(sketch, "E2636", {"start": v(406.73, -17.28) * mm, "end": v(406.02, -16.6) * mm});
            skLineSegment(sketch, "E2637", {"start": v(406.02, -16.6) * mm, "end": v(405.32, -15.9) * mm});
            skLineSegment(sketch, "E2638", {"start": v(405.32, -15.9) * mm, "end": v(404.6, -15.21) * mm});
            skLineSegment(sketch, "E2639", {"start": v(404.6, -15.21) * mm, "end": v(403.89, -14.5) * mm});
            skLineSegment(sketch, "E2640", {"start": v(403.89, -14.5) * mm, "end": v(403.17, -13.8) * mm});
            skLineSegment(sketch, "E2641", {"start": v(403.17, -13.8) * mm, "end": v(402.45, -13.09) * mm});
            skLineSegment(sketch, "E2642", {"start": v(402.45, -13.09) * mm, "end": v(401.72, -12.37) * mm});
            skLineSegment(sketch, "E2643", {"start": v(401.72, -12.37) * mm, "end": v(400.99, -11.66) * mm});
            skLineSegment(sketch, "E2644", {"start": v(400.99, -11.66) * mm, "end": v(400.25, -10.94) * mm});
            skLineSegment(sketch, "E2645", {"start": v(400.25, -10.94) * mm, "end": v(399.5, -10.23) * mm});
            skLineSegment(sketch, "E2646", {"start": v(399.5, -10.23) * mm, "end": v(398.76, -9.52) * mm});
            skLineSegment(sketch, "E2647", {"start": v(398.76, -9.52) * mm, "end": v(398.01, -8.82) * mm});
            skLineSegment(sketch, "E2648", {"start": v(398.01, -8.82) * mm, "end": v(397.26, -8.12) * mm});
            skLineSegment(sketch, "E2649", {"start": v(397.26, -8.12) * mm, "end": v(396.5, -7.43) * mm});
            skLineSegment(sketch, "E2650", {"start": v(396.5, -7.43) * mm, "end": v(395.74, -6.75) * mm});
            skLineSegment(sketch, "E2651", {"start": v(395.74, -6.75) * mm, "end": v(394.97, -6.08) * mm});
            skLineSegment(sketch, "E2652", {"start": v(394.97, -6.08) * mm, "end": v(394.2, -5.42) * mm});
            skLineSegment(sketch, "E2653", {"start": v(394.2, -5.42) * mm, "end": v(393.41, -4.78) * mm});
            skLineSegment(sketch, "E2654", {"start": v(393.41, -4.78) * mm, "end": v(392.63, -4.15) * mm});
            skLineSegment(sketch, "E2655", {"start": v(392.63, -4.15) * mm, "end": v(391.84, -3.53) * mm});
            skLineSegment(sketch, "E2656", {"start": v(391.84, -3.53) * mm, "end": v(391.05, -2.93) * mm});
            skLineSegment(sketch, "E2657", {"start": v(391.05, -2.93) * mm, "end": v(390.25, -2.36) * mm});
            skLineSegment(sketch, "E2658", {"start": v(390.25, -2.36) * mm, "end": v(389.44, -1.8) * mm});
            skLineSegment(sketch, "E2659", {"start": v(389.44, -1.8) * mm, "end": v(388.63, -1.26) * mm});
            skLineSegment(sketch, "E2660", {"start": v(388.63, -1.26) * mm, "end": v(387.82, -0.75) * mm});
            skLineSegment(sketch, "E2661", {"start": v(387.82, -0.75) * mm, "end": v(387, -0.26) * mm});
            skLineSegment(sketch, "E2662", {"start": v(387, -0.26) * mm, "end": v(386.17, 0.2) * mm});
            skLineSegment(sketch, "E2663", {"start": v(386.17, 0.2) * mm, "end": v(385.34, 0.64) * mm});
            skLineSegment(sketch, "E2664", {"start": v(385.34, 0.64) * mm, "end": v(384.5, 1.04) * mm});
            skLineSegment(sketch, "E2665", {"start": v(384.5, 1.04) * mm, "end": v(384.5, 4.04) * mm});
            skLineSegment(sketch, "E2666", {"start": v(384.5, 4.04) * mm, "end": v(385.36, 4.44) * mm});
            skLineSegment(sketch, "E2667", {"start": v(385.36, 4.44) * mm, "end": v(386.2, 4.85) * mm});
            skLineSegment(sketch, "E2668", {"start": v(386.2, 4.85) * mm, "end": v(387.06, 5.3) * mm});
            skLineSegment(sketch, "E2669", {"start": v(387.06, 5.3) * mm, "end": v(387.9, 5.75) * mm});
            skLineSegment(sketch, "E2670", {"start": v(387.9, 5.75) * mm, "end": v(388.74, 6.22) * mm});
            skLineSegment(sketch, "E2671", {"start": v(388.74, 6.22) * mm, "end": v(389.58, 6.72) * mm});
            skLineSegment(sketch, "E2672", {"start": v(389.58, 6.72) * mm, "end": v(390.4, 7.23) * mm});
            skLineSegment(sketch, "E2673", {"start": v(390.4, 7.23) * mm, "end": v(391.24, 7.76) * mm});
            skLineSegment(sketch, "E2674", {"start": v(391.24, 7.76) * mm, "end": v(392.06, 8.3) * mm});
            skLineSegment(sketch, "E2675", {"start": v(392.06, 8.3) * mm, "end": v(392.88, 8.86) * mm});
            skLineSegment(sketch, "E2676", {"start": v(392.88, 8.86) * mm, "end": v(393.7, 9.43) * mm});
            skLineSegment(sketch, "E2677", {"start": v(393.7, 9.43) * mm, "end": v(394.5, 10.01) * mm});
            skLineSegment(sketch, "E2678", {"start": v(394.5, 10.01) * mm, "end": v(395.32, 10.6) * mm});
            skLineSegment(sketch, "E2679", {"start": v(395.32, 10.6) * mm, "end": v(396.12, 11.21) * mm});
            skLineSegment(sketch, "E2680", {"start": v(396.12, 11.21) * mm, "end": v(396.92, 11.83) * mm});
            skLineSegment(sketch, "E2681", {"start": v(396.92, 11.83) * mm, "end": v(397.72, 12.45) * mm});
            skLineSegment(sketch, "E2682", {"start": v(397.72, 12.45) * mm, "end": v(398.52, 13.09) * mm});
            skLineSegment(sketch, "E2683", {"start": v(398.52, 13.09) * mm, "end": v(399.3, 13.73) * mm});
            skLineSegment(sketch, "E2684", {"start": v(399.3, 13.73) * mm, "end": v(400.1, 14.38) * mm});
            skLineSegment(sketch, "E2685", {"start": v(400.1, 14.38) * mm, "end": v(400.88, 15.03) * mm});
            skLineSegment(sketch, "E2686", {"start": v(400.88, 15.03) * mm, "end": v(401.66, 15.69) * mm});
            skLineSegment(sketch, "E2687", {"start": v(401.66, 15.69) * mm, "end": v(402.44, 16.35) * mm});
            skLineSegment(sketch, "E2688", {"start": v(402.44, 16.35) * mm, "end": v(403.22, 17) * mm});
            skLineSegment(sketch, "E2689", {"start": v(403.22, 17) * mm, "end": v(403.99, 17.67) * mm});
            skLineSegment(sketch, "E2690", {"start": v(403.99, 17.67) * mm, "end": v(404.76, 18.34) * mm});
            skLineSegment(sketch, "E2691", {"start": v(404.76, 18.34) * mm, "end": v(405.52, 19) * mm});
            skLineSegment(sketch, "E2692", {"start": v(405.52, 19) * mm, "end": v(406.29, 19.67) * mm});
            skLineSegment(sketch, "E2693", {"start": v(406.29, 19.67) * mm, "end": v(407.05, 20.33) * mm});
            skLineSegment(sketch, "E2694", {"start": v(407.05, 20.33) * mm, "end": v(407.8, 20.99) * mm});
            skLineSegment(sketch, "E2695", {"start": v(407.8, 20.99) * mm, "end": v(408.56, 21.65) * mm});
            skLineSegment(sketch, "E2696", {"start": v(408.56, 21.65) * mm, "end": v(409.3, 22.3) * mm});
            skLineSegment(sketch, "E2697", {"start": v(409.3, 22.3) * mm, "end": v(410.06, 22.94) * mm});
            skLineSegment(sketch, "E2698", {"start": v(410.06, 22.94) * mm, "end": v(410.8, 23.58) * mm});
            skLineSegment(sketch, "E2699", {"start": v(410.8, 23.58) * mm, "end": v(411.55, 24.21) * mm});
            skLineSegment(sketch, "E2700", {"start": v(411.55, 24.21) * mm, "end": v(412.29, 24.83) * mm});
            skLineSegment(sketch, "E2701", {"start": v(412.29, 24.83) * mm, "end": v(413.03, 25.45) * mm});
            skLineSegment(sketch, "E2702", {"start": v(413.03, 25.45) * mm, "end": v(413.77, 26.05) * mm});
            skLineSegment(sketch, "E2703", {"start": v(413.77, 26.05) * mm, "end": v(414.5, 26.64) * mm});
            skLineSegment(sketch, "E2704", {"start": v(414.5, 26.64) * mm, "end": v(415.26, 27.25) * mm});
            skLineSegment(sketch, "E2705", {"start": v(415.26, 27.25) * mm, "end": v(416.04, 27.86) * mm});
            skLineSegment(sketch, "E2706", {"start": v(416.04, 27.86) * mm, "end": v(416.82, 28.46) * mm});
            skLineSegment(sketch, "E2707", {"start": v(416.82, 28.46) * mm, "end": v(417.61, 29.06) * mm});
            skLineSegment(sketch, "E2708", {"start": v(417.61, 29.06) * mm, "end": v(418.41, 29.66) * mm});
            skLineSegment(sketch, "E2709", {"start": v(418.41, 29.66) * mm, "end": v(419.22, 30.26) * mm});
            skLineSegment(sketch, "E2710", {"start": v(419.22, 30.26) * mm, "end": v(420.03, 30.86) * mm});
            skLineSegment(sketch, "E2711", {"start": v(420.03, 30.86) * mm, "end": v(420.85, 31.47) * mm});
            skLineSegment(sketch, "E2712", {"start": v(420.85, 31.47) * mm, "end": v(421.67, 32.07) * mm});
            skLineSegment(sketch, "E2713", {"start": v(421.67, 32.07) * mm, "end": v(422.5, 32.67) * mm});
            skLineSegment(sketch, "E2714", {"start": v(422.5, 32.67) * mm, "end": v(423.33, 33.27) * mm});
            skLineSegment(sketch, "E2715", {"start": v(423.33, 33.27) * mm, "end": v(424.16, 33.87) * mm});
            skLineSegment(sketch, "E2716", {"start": v(424.16, 33.87) * mm, "end": v(425, 34.48) * mm});
            skLineSegment(sketch, "E2717", {"start": v(425, 34.48) * mm, "end": v(425.83, 35.08) * mm});
            skLineSegment(sketch, "E2718", {"start": v(425.83, 35.08) * mm, "end": v(426.67, 35.7) * mm});
            skLineSegment(sketch, "E2719", {"start": v(426.67, 35.7) * mm, "end": v(427.5, 36.3) * mm});
            skLineSegment(sketch, "E2720", {"start": v(427.5, 36.3) * mm, "end": v(428.34, 36.91) * mm});
            skLineSegment(sketch, "E2721", {"start": v(428.34, 36.91) * mm, "end": v(429.18, 37.53) * mm});
            skLineSegment(sketch, "E2722", {"start": v(429.18, 37.53) * mm, "end": v(430, 38.15) * mm});
            skLineSegment(sketch, "E2723", {"start": v(430, 38.15) * mm, "end": v(430.84, 38.77) * mm});
            skLineSegment(sketch, "E2724", {"start": v(430.84, 38.77) * mm, "end": v(431.67, 39.4) * mm});
            skLineSegment(sketch, "E2725", {"start": v(431.67, 39.4) * mm, "end": v(432.5, 40.02) * mm});
            skLineSegment(sketch, "E2726", {"start": v(432.5, 40.02) * mm, "end": v(433.31, 40.65) * mm});
            skLineSegment(sketch, "E2727", {"start": v(433.31, 40.65) * mm, "end": v(434.13, 41.29) * mm});
            skLineSegment(sketch, "E2728", {"start": v(434.13, 41.29) * mm, "end": v(434.93, 41.93) * mm});
            skLineSegment(sketch, "E2729", {"start": v(434.93, 41.93) * mm, "end": v(435.73, 42.58) * mm});
            skLineSegment(sketch, "E2730", {"start": v(435.73, 42.58) * mm, "end": v(436.53, 43.23) * mm});
            skLineSegment(sketch, "E2731", {"start": v(436.53, 43.23) * mm, "end": v(437.31, 43.89) * mm});
            skLineSegment(sketch, "E2732", {"start": v(437.31, 43.89) * mm, "end": v(438.1, 44.55) * mm});
            skLineSegment(sketch, "E2733", {"start": v(438.1, 44.55) * mm, "end": v(438.86, 45.22) * mm});
            skLineSegment(sketch, "E2734", {"start": v(438.86, 45.22) * mm, "end": v(439.62, 45.9) * mm});
            skLineSegment(sketch, "E2735", {"start": v(439.62, 45.9) * mm, "end": v(440.37, 46.57) * mm});
            skLineSegment(sketch, "E2736", {"start": v(440.37, 46.57) * mm, "end": v(441.1, 47.26) * mm});
            skLineSegment(sketch, "E2737", {"start": v(441.1, 47.26) * mm, "end": v(441.83, 47.96) * mm});
            skLineSegment(sketch, "E2738", {"start": v(441.83, 47.96) * mm, "end": v(442.54, 48.66) * mm});
            skLineSegment(sketch, "E2739", {"start": v(442.54, 48.66) * mm, "end": v(443.23, 49.37) * mm});
            skLineSegment(sketch, "E2740", {"start": v(443.23, 49.37) * mm, "end": v(443.92, 50.09) * mm});
            skLineSegment(sketch, "E2741", {"start": v(443.92, 50.09) * mm, "end": v(444.59, 50.81) * mm});
            skLineSegment(sketch, "E2742", {"start": v(444.59, 50.81) * mm, "end": v(445.24, 51.55) * mm});
            skLineSegment(sketch, "E2743", {"start": v(445.24, 51.55) * mm, "end": v(445.88, 52.3) * mm});
            skLineSegment(sketch, "E2744", {"start": v(445.88, 52.3) * mm, "end": v(446.5, 53.04) * mm});
            skLineSegment(sketch, "E2745", {"start": v(446.5, 53.04) * mm, "end": v(409.5, 53.04) * mm});
            skLineSegment(sketch, "E2746", {"start": v(409.5, 53.04) * mm, "end": v(408.57, 53.05) * mm});
            skLineSegment(sketch, "E2747", {"start": v(408.57, 53.05) * mm, "end": v(407.6, 53.08) * mm});
            skLineSegment(sketch, "E2748", {"start": v(407.6, 53.08) * mm, "end": v(406.62, 53.13) * mm});
            skLineSegment(sketch, "E2749", {"start": v(406.62, 53.13) * mm, "end": v(405.61, 53.18) * mm});
            skLineSegment(sketch, "E2750", {"start": v(405.61, 53.18) * mm, "end": v(404.59, 53.23) * mm});
            skLineSegment(sketch, "E2751", {"start": v(404.59, 53.23) * mm, "end": v(403.55, 53.29) * mm});
            skLineSegment(sketch, "E2752", {"start": v(403.55, 53.29) * mm, "end": v(402.5, 53.34) * mm});
            skLineSegment(sketch, "E2753", {"start": v(402.5, 53.34) * mm, "end": v(401.45, 53.38) * mm});
            skLineSegment(sketch, "E2754", {"start": v(401.45, 53.38) * mm, "end": v(400.4, 53.41) * mm});
            skLineSegment(sketch, "E2755", {"start": v(400.4, 53.41) * mm, "end": v(399.34, 53.42) * mm});
            skLineSegment(sketch, "E2756", {"start": v(399.34, 53.42) * mm, "end": v(398.3, 53.4) * mm});
            skLineSegment(sketch, "E2757", {"start": v(398.3, 53.4) * mm, "end": v(397.26, 53.37) * mm});
            skLineSegment(sketch, "E2758", {"start": v(397.26, 53.37) * mm, "end": v(396.24, 53.3) * mm});
            skLineSegment(sketch, "E2759", {"start": v(396.24, 53.3) * mm, "end": v(395.24, 53.19) * mm});
            skLineSegment(sketch, "E2760", {"start": v(395.24, 53.19) * mm, "end": v(394.26, 53.04) * mm});
            skLineSegment(sketch, "E2761", {"start": v(394.26, 53.04) * mm, "end": v(393.31, 52.85) * mm});
            skLineSegment(sketch, "E2762", {"start": v(393.31, 52.85) * mm, "end": v(392.39, 52.6) * mm});
            skLineSegment(sketch, "E2763", {"start": v(392.39, 52.6) * mm, "end": v(391.5, 52.3) * mm});
            skLineSegment(sketch, "E2764", {"start": v(391.5, 52.3) * mm, "end": v(390.63, 51.94) * mm});
            skLineSegment(sketch, "E2765", {"start": v(390.63, 51.94) * mm, "end": v(389.77, 51.52) * mm});
            skLineSegment(sketch, "E2766", {"start": v(389.77, 51.52) * mm, "end": v(388.92, 51.06) * mm});
            skLineSegment(sketch, "E2767", {"start": v(388.92, 51.06) * mm, "end": v(388.1, 50.54) * mm});
            skLineSegment(sketch, "E2768", {"start": v(388.1, 50.54) * mm, "end": v(387.27, 50) * mm});
            skLineSegment(sketch, "E2769", {"start": v(387.27, 50) * mm, "end": v(386.47, 49.4) * mm});
            skLineSegment(sketch, "E2770", {"start": v(386.47, 49.4) * mm, "end": v(385.67, 48.79) * mm});
            skLineSegment(sketch, "E2771", {"start": v(385.67, 48.79) * mm, "end": v(384.88, 48.14) * mm});
            skLineSegment(sketch, "E2772", {"start": v(384.88, 48.14) * mm, "end": v(384.1, 47.48) * mm});
            skLineSegment(sketch, "E2773", {"start": v(384.1, 47.48) * mm, "end": v(383.34, 46.8) * mm});
            skLineSegment(sketch, "E2774", {"start": v(383.34, 46.8) * mm, "end": v(382.59, 46.12) * mm});
            skLineSegment(sketch, "E2775", {"start": v(382.59, 46.12) * mm, "end": v(381.84, 45.43) * mm});
            skLineSegment(sketch, "E2776", {"start": v(381.84, 45.43) * mm, "end": v(381.1, 44.74) * mm});
            skLineSegment(sketch, "E2777", {"start": v(381.1, 44.74) * mm, "end": v(380.37, 44.05) * mm});
            skLineSegment(sketch, "E2778", {"start": v(380.37, 44.05) * mm, "end": v(379.64, 43.38) * mm});
            skLineSegment(sketch, "E2779", {"start": v(379.64, 43.38) * mm, "end": v(378.92, 42.72) * mm});
            skLineSegment(sketch, "E2780", {"start": v(378.92, 42.72) * mm, "end": v(378.2, 42.08) * mm});
            skLineSegment(sketch, "E2781", {"start": v(378.2, 42.08) * mm, "end": v(377.5, 41.47) * mm});
            skLineSegment(sketch, "E2782", {"start": v(377.5, 41.47) * mm, "end": v(376.74, 40.83) * mm});
            skLineSegment(sketch, "E2783", {"start": v(376.74, 40.83) * mm, "end": v(375.99, 40.18) * mm});
            skLineSegment(sketch, "E2784", {"start": v(375.99, 40.18) * mm, "end": v(375.23, 39.53) * mm});
            skLineSegment(sketch, "E2785", {"start": v(375.23, 39.53) * mm, "end": v(374.47, 38.88) * mm});
            skLineSegment(sketch, "E2786", {"start": v(374.47, 38.88) * mm, "end": v(373.71, 38.23) * mm});
            skLineSegment(sketch, "E2787", {"start": v(373.71, 38.23) * mm, "end": v(372.96, 37.58) * mm});
            skLineSegment(sketch, "E2788", {"start": v(372.96, 37.58) * mm, "end": v(372.2, 36.92) * mm});
            skLineSegment(sketch, "E2789", {"start": v(372.2, 36.92) * mm, "end": v(371.44, 36.26) * mm});
            skLineSegment(sketch, "E2790", {"start": v(371.44, 36.26) * mm, "end": v(370.69, 35.6) * mm});
            skLineSegment(sketch, "E2791", {"start": v(370.69, 35.6) * mm, "end": v(369.93, 34.94) * mm});
            skLineSegment(sketch, "E2792", {"start": v(369.93, 34.94) * mm, "end": v(369.17, 34.28) * mm});
            skLineSegment(sketch, "E2793", {"start": v(369.17, 34.28) * mm, "end": v(368.41, 33.62) * mm});
            skLineSegment(sketch, "E2794", {"start": v(368.41, 33.62) * mm, "end": v(367.65, 32.96) * mm});
            skLineSegment(sketch, "E2795", {"start": v(367.65, 32.96) * mm, "end": v(366.9, 32.3) * mm});
            skLineSegment(sketch, "E2796", {"start": v(366.9, 32.3) * mm, "end": v(366.13, 31.64) * mm});
            skLineSegment(sketch, "E2797", {"start": v(366.13, 31.64) * mm, "end": v(365.37, 30.98) * mm});
            skLineSegment(sketch, "E2798", {"start": v(365.37, 30.98) * mm, "end": v(364.6, 30.32) * mm});
            skLineSegment(sketch, "E2799", {"start": v(364.6, 30.32) * mm, "end": v(363.84, 29.66) * mm});
            skLineSegment(sketch, "E2800", {"start": v(363.84, 29.66) * mm, "end": v(363.07, 29) * mm});
            skLineSegment(sketch, "E2801", {"start": v(363.07, 29) * mm, "end": v(362.3, 28.35) * mm});
            skLineSegment(sketch, "E2802", {"start": v(362.3, 28.35) * mm, "end": v(361.53, 27.7) * mm});
            skLineSegment(sketch, "E2803", {"start": v(361.53, 27.7) * mm, "end": v(360.76, 27.05) * mm});
            skLineSegment(sketch, "E2804", {"start": v(360.76, 27.05) * mm, "end": v(360, 26.4) * mm});
            skLineSegment(sketch, "E2805", {"start": v(360, 26.4) * mm, "end": v(359.22, 25.76) * mm});
            skLineSegment(sketch, "E2806", {"start": v(359.22, 25.76) * mm, "end": v(358.44, 25.12) * mm});
            skLineSegment(sketch, "E2807", {"start": v(358.44, 25.12) * mm, "end": v(357.66, 24.48) * mm});
            skLineSegment(sketch, "E2808", {"start": v(357.66, 24.48) * mm, "end": v(356.88, 23.84) * mm});
            skLineSegment(sketch, "E2809", {"start": v(356.88, 23.84) * mm, "end": v(356.1, 23.21) * mm});
            skLineSegment(sketch, "E2810", {"start": v(356.1, 23.21) * mm, "end": v(355.31, 22.59) * mm});
            skLineSegment(sketch, "E2811", {"start": v(355.31, 22.59) * mm, "end": v(354.53, 21.96) * mm});
            skLineSegment(sketch, "E2812", {"start": v(354.53, 21.96) * mm, "end": v(353.74, 21.35) * mm});
            skLineSegment(sketch, "E2813", {"start": v(353.74, 21.35) * mm, "end": v(352.95, 20.73) * mm});
            skLineSegment(sketch, "E2814", {"start": v(352.95, 20.73) * mm, "end": v(352.15, 20.13) * mm});
            skLineSegment(sketch, "E2815", {"start": v(352.15, 20.13) * mm, "end": v(351.35, 19.52) * mm});
            skLineSegment(sketch, "E2816", {"start": v(351.35, 19.52) * mm, "end": v(350.55, 18.93) * mm});
            skLineSegment(sketch, "E2817", {"start": v(350.55, 18.93) * mm, "end": v(349.75, 18.34) * mm});
            skLineSegment(sketch, "E2818", {"start": v(349.75, 18.34) * mm, "end": v(348.94, 17.75) * mm});
            skLineSegment(sketch, "E2819", {"start": v(348.94, 17.75) * mm, "end": v(348.13, 17.18) * mm});
            skLineSegment(sketch, "E2820", {"start": v(348.13, 17.18) * mm, "end": v(347.32, 16.6) * mm});
            skLineSegment(sketch, "E2821", {"start": v(347.32, 16.6) * mm, "end": v(346.5, 16.04) * mm});
            skLineSegment(sketch, "E2822", {"start": v(346.5, 16.04) * mm, "end": v(346.5, 53.04) * mm});
            skLineSegment(sketch, "E2823", {"start": v(346.5, 53.04) * mm, "end": v(305.5, 53.04) * mm});
            skLineSegment(sketch, "E2824", {"start": v(458.5, 53.04) * mm, "end": v(458.5, -52.96) * mm});
            skLineSegment(sketch, "E2825", {"start": v(458.5, -52.96) * mm, "end": v(499.5, -52.96) * mm});
            skLineSegment(sketch, "E2826", {"start": v(499.5, -52.96) * mm, "end": v(499.5, 53.04) * mm});
            skLineSegment(sketch, "E2827", {"start": v(499.5, 53.04) * mm, "end": v(458.5, 53.04) * mm});
            skSolve(sketch);
        }
        {
            var Q0;
            Q0=makeQuery(id+"F0.imprint","IMPRINT",FACE,{"disambiguationData":[TD([[makeQuery(id+"F0.imprint","IMPRINT",EDGE,{"derivedFrom":sQuery(id+"F0.wireOp",EDGE,"E0")}),1.0]])]});
            var Q1;
            Q1=makeQuery(id+"F0.imprint","IMPRINT",FACE,{"disambiguationData":[TD([[makeQuery(id+"F0.imprint","IMPRINT",EDGE,{"derivedFrom":sQuery(id+"F0.wireOp",EDGE,"E936")}),1.0]])]});
            var Q2;
            Q2=makeQuery(id+"F0.imprint","IMPRINT",FACE,{"disambiguationData":[TD([[makeQuery(id+"F0.imprint","IMPRINT",EDGE,{"derivedFrom":sQuery(id+"F0.wireOp",EDGE,"E1647")}),1.0]])]});
            var Q3;
            Q3=makeQuery(id+"F0.imprint","IMPRINT",FACE,{"disambiguationData":[TD([[makeQuery(id+"F0.imprint","IMPRINT",EDGE,{"derivedFrom":sQuery(id+"F0.wireOp",EDGE,"E1965")}),1.0]])]});
            var Q4;
            Q4=makeQuery(id+"F0.imprint","IMPRINT",FACE,{"disambiguationData":[TD([[makeQuery(id+"F0.imprint","IMPRINT",EDGE,{"derivedFrom":sQuery(id+"F0.wireOp",EDGE,"E2185")}),1.0]])]});
            var Q5;
            Q5=makeQuery(id+"F0.imprint","IMPRINT",FACE,{"disambiguationData":[TD([[makeQuery(id+"F0.imprint","IMPRINT",EDGE,{"derivedFrom":sQuery(id+"F0.wireOp",EDGE,"E2504")}),1.0]])]});
            var Q6;
            Q6=makeQuery(id+"F0.imprint","IMPRINT",FACE,{"disambiguationData":[TD([[makeQuery(id+"F0.imprint","IMPRINT",EDGE,{"derivedFrom":sQuery(id+"F0.wireOp",EDGE,"E2824")}),1.0]])]});
            extrude(context, id + "F1", {"entities" : qUnion([Q0, Q1, Q2, Q3, Q4, Q5, Q6]), "depth" : 25 * mm, "offsetDistance" : 25 * mm});
        }
    });
